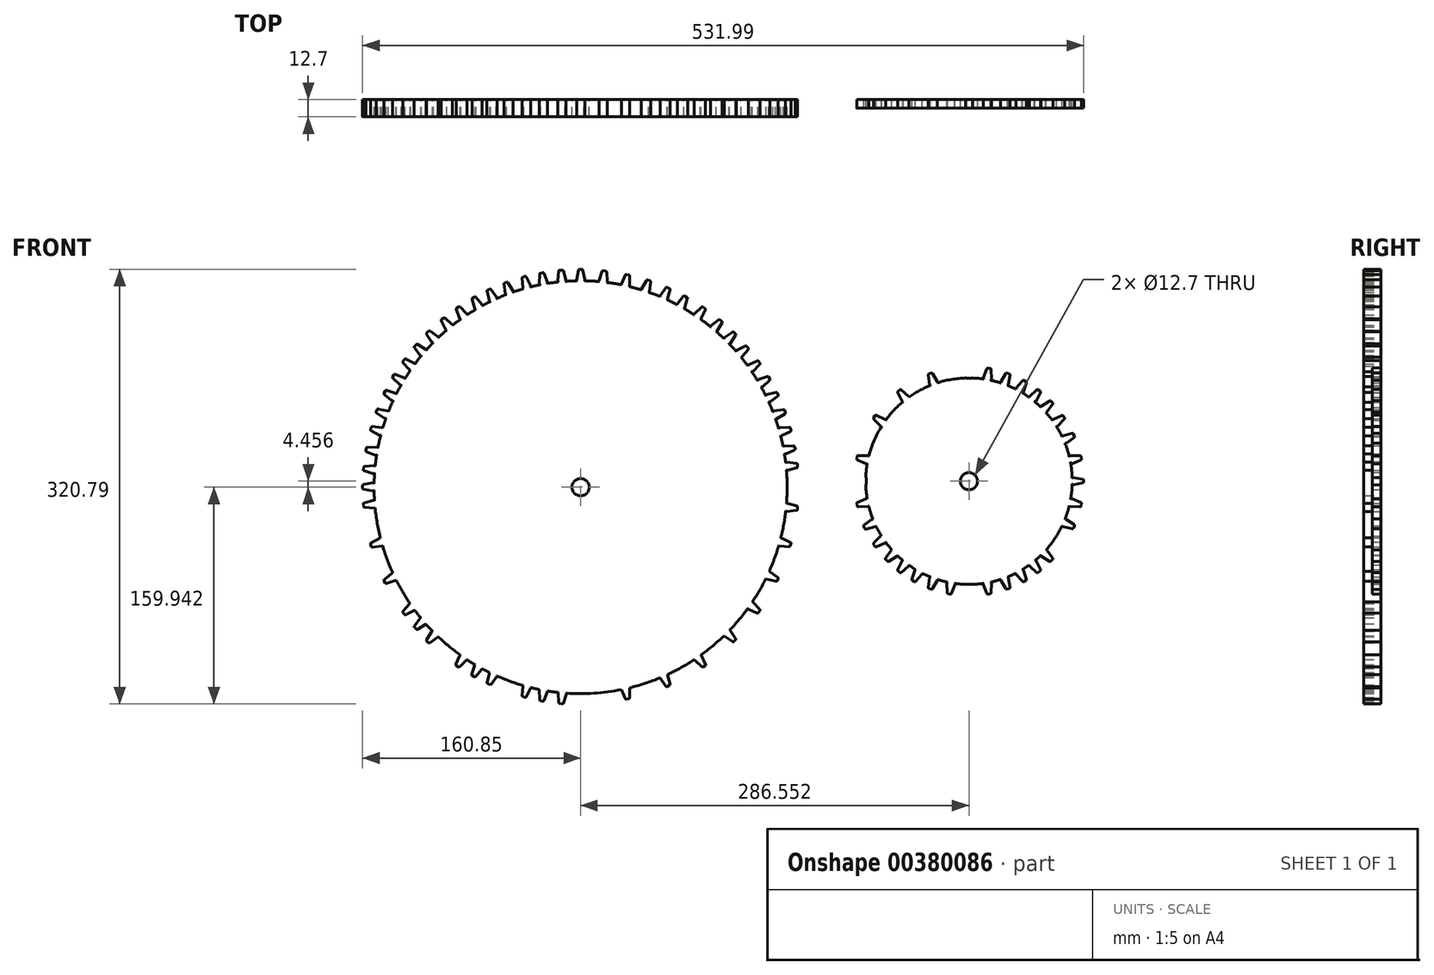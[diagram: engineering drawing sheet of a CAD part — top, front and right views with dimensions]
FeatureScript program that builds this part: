
annotation { "Feature Type Name" : "Feature", "Feature Type Description" : "" }
export const myFeature = defineFeature(function(context is Context, id is Id, definition is map)
    precondition{}
    {
        {
            var Q0;
            Q0=qCreatedBy(makeId("Front.planeOp"),FACE);
            var sketch = newSketch(context, id + "F0", { "sketchPlane" : qUnion([Q0])});
            skCircle(sketch, "E0", {"center": v(-69.44, 32.26) * mm, "radius": 152.4 * mm});
            skCircle(sketch, "E1", {"center": v(217.11, 36.72) * mm, "radius": 76.2 * mm});
            skCircle(sketch, "E2", {"center": v(-69.44, 32.26) * mm, "radius": 6.35 * mm});
            skCircle(sketch, "E3", {"center": v(217.11, 36.72) * mm, "radius": 6.35 * mm});
            skLineSegment(sketch, "E4", {"start": v(-71.67, 184.63) * mm, "end": v(-67.16, 184.63) * mm});
            skLineSegment(sketch, "E5", {"start": v(-66.42, 185.54) * mm, "end": v(-67.77, 192.49) * mm});
            skLineSegment(sketch, "E6", {"start": v(-68.52, 193.1) * mm, "end": v(-70.31, 193.1) * mm});
            skLineSegment(sketch, "E7", {"start": v(-71.06, 192.49) * mm, "end": v(-72.41, 185.54) * mm});
            skPoint(sketch, "E8.visualSharp", {"position": v(-70.94, 193.1) * mm});
            skArc(sketch, "E8.filletArc", {"start": v(-70.31, 193.1) * mm, "mid": v(-70.8, 192.93) * mm, "end": v(-71.06, 192.49) * mm});
            skPoint(sketch, "E9.visualSharp", {"position": v(-67.9, 193.1) * mm});
            skArc(sketch, "E9.filletArc", {"start": v(-67.77, 192.49) * mm, "mid": v(-68.03, 192.93) * mm, "end": v(-68.52, 193.1) * mm});
            skPoint(sketch, "E10.visualSharp", {"position": v(-72.6, 184.63) * mm});
            skArc(sketch, "E10.filletArc", {"start": v(-72.41, 185.54) * mm, "mid": v(-72.25, 184.9) * mm, "end": v(-71.67, 184.63) * mm});
            skPoint(sketch, "E11.visualSharp", {"position": v(-66.24, 184.63) * mm});
            skArc(sketch, "E11.filletArc", {"start": v(-67.16, 184.63) * mm, "mid": v(-66.58, 184.9) * mm, "end": v(-66.42, 185.54) * mm});
            skLineSegment(sketch, "E12", {"start": v(-55.07, 183.9) * mm, "end": v(-50.6, 183.35) * mm});
            skLineSegment(sketch, "E13", {"start": v(-49.75, 184.16) * mm, "end": v(-50.26, 191.23) * mm});
            skLineSegment(sketch, "E14", {"start": v(-50.92, 191.93) * mm, "end": v(-52.7, 192.14) * mm});
            skLineSegment(sketch, "E15", {"start": v(-53.52, 191.62) * mm, "end": v(-55.7, 184.88) * mm});
            skPoint(sketch, "E16.visualSharp", {"position": v(-53.33, 192.22) * mm});
            skArc(sketch, "E16.filletArc", {"start": v(-52.7, 192.14) * mm, "mid": v(-53.2, 192.03) * mm, "end": v(-53.52, 191.62) * mm});
            skPoint(sketch, "E17.visualSharp", {"position": v(-50.3, 191.85) * mm});
            skArc(sketch, "E17.filletArc", {"start": v(-50.26, 191.23) * mm, "mid": v(-50.46, 191.7) * mm, "end": v(-50.92, 191.93) * mm});
            skPoint(sketch, "E18.visualSharp", {"position": v(-55.98, 184) * mm});
            skArc(sketch, "E18.filletArc", {"start": v(-55.7, 184.88) * mm, "mid": v(-55.62, 184.24) * mm, "end": v(-55.07, 183.9) * mm});
            skPoint(sketch, "E19.visualSharp", {"position": v(-49.68, 183.24) * mm});
            skArc(sketch, "E19.filletArc", {"start": v(-50.6, 183.35) * mm, "mid": v(-49.98, 183.55) * mm, "end": v(-49.75, 184.16) * mm});
            skLineSegment(sketch, "E20", {"start": v(-38.66, 181.2) * mm, "end": v(-34.24, 180.34) * mm});
            skLineSegment(sketch, "E21", {"start": v(-33.34, 181.08) * mm, "end": v(-33.33, 188.17) * mm});
            skLineSegment(sketch, "E22", {"start": v(-33.94, 188.92) * mm, "end": v(-35.7, 189.26) * mm});
            skLineSegment(sketch, "E23", {"start": v(-36.55, 188.8) * mm, "end": v(-39.22, 182.24) * mm});
            skPoint(sketch, "E24.visualSharp", {"position": v(-36.32, 189.38) * mm});
            skArc(sketch, "E24.filletArc", {"start": v(-35.7, 189.26) * mm, "mid": v(-36.2, 189.18) * mm, "end": v(-36.55, 188.8) * mm});
            skPoint(sketch, "E25.visualSharp", {"position": v(-33.33, 188.8) * mm});
            skArc(sketch, "E25.filletArc", {"start": v(-33.33, 188.17) * mm, "mid": v(-33.5, 188.65) * mm, "end": v(-33.94, 188.92) * mm});
            skPoint(sketch, "E26.visualSharp", {"position": v(-39.57, 181.38) * mm});
            skArc(sketch, "E26.filletArc", {"start": v(-39.22, 182.24) * mm, "mid": v(-39.18, 181.59) * mm, "end": v(-38.66, 181.2) * mm});
            skPoint(sketch, "E27.visualSharp", {"position": v(-33.34, 180.16) * mm});
            skArc(sketch, "E27.filletArc", {"start": v(-34.24, 180.34) * mm, "mid": v(-33.61, 180.5) * mm, "end": v(-33.34, 181.08) * mm});
            skLineSegment(sketch, "E28", {"start": v(-24.04, 177.66) * mm, "end": v(-19.78, 176.2) * mm});
            skLineSegment(sketch, "E29", {"start": v(-18.78, 176.81) * mm, "end": v(-17.8, 183.83) * mm});
            skLineSegment(sketch, "E30", {"start": v(-18.3, 184.65) * mm, "end": v(-20, 185.24) * mm});
            skLineSegment(sketch, "E31", {"start": v(-20.9, 184.9) * mm, "end": v(-24.45, 178.76) * mm});
            skPoint(sketch, "E32.visualSharp", {"position": v(-20.6, 185.44) * mm});
            skArc(sketch, "E32.filletArc", {"start": v(-20, 185.24) * mm, "mid": v(-20.51, 185.23) * mm, "end": v(-20.9, 184.9) * mm});
            skPoint(sketch, "E33.visualSharp", {"position": v(-17.7, 184.45) * mm});
            skArc(sketch, "E33.filletArc", {"start": v(-17.8, 183.83) * mm, "mid": v(-17.9, 184.33) * mm, "end": v(-18.3, 184.65) * mm});
            skPoint(sketch, "E34.visualSharp", {"position": v(-24.91, 177.96) * mm});
            skArc(sketch, "E34.filletArc", {"start": v(-24.45, 178.76) * mm, "mid": v(-24.5, 178.12) * mm, "end": v(-24.04, 177.66) * mm});
            skPoint(sketch, "E35.visualSharp", {"position": v(-18.9, 175.9) * mm});
            skArc(sketch, "E35.filletArc", {"start": v(-19.78, 176.2) * mm, "mid": v(-19.13, 176.27) * mm, "end": v(-18.78, 176.81) * mm});
            skLineSegment(sketch, "E36", {"start": v(-10.35, 172.62) * mm, "end": v(-6.24, 170.78) * mm});
            skLineSegment(sketch, "E37", {"start": v(-5.2, 171.3) * mm, "end": v(-3.58, 178.2) * mm});
            skLineSegment(sketch, "E38", {"start": v(-4, 179.07) * mm, "end": v(-5.64, 179.8) * mm});
            skLineSegment(sketch, "E39", {"start": v(-6.58, 179.55) * mm, "end": v(-10.66, 173.76) * mm});
            skPoint(sketch, "E40.visualSharp", {"position": v(-6.22, 180.06) * mm});
            skArc(sketch, "E40.filletArc", {"start": v(-5.64, 179.8) * mm, "mid": v(-6.16, 179.84) * mm, "end": v(-6.58, 179.55) * mm});
            skPoint(sketch, "E41.visualSharp", {"position": v(-3.43, 178.8) * mm});
            skArc(sketch, "E41.filletArc", {"start": v(-3.58, 178.2) * mm, "mid": v(-3.64, 178.7) * mm, "end": v(-4, 179.07) * mm});
            skPoint(sketch, "E42.visualSharp", {"position": v(-11.2, 173) * mm});
            skArc(sketch, "E42.filletArc", {"start": v(-10.66, 173.76) * mm, "mid": v(-10.77, 173.12) * mm, "end": v(-10.35, 172.62) * mm});
            skPoint(sketch, "E43.visualSharp", {"position": v(-5.4, 170.4) * mm});
            skArc(sketch, "E43.filletArc", {"start": v(-6.24, 170.78) * mm, "mid": v(-5.6, 170.8) * mm, "end": v(-5.2, 171.3) * mm});
            skLineSegment(sketch, "E44", {"start": v(2.22, 166.6) * mm, "end": v(6.17, 164.44) * mm});
            skLineSegment(sketch, "E45", {"start": v(7.26, 164.87) * mm, "end": v(9.41, 171.62) * mm});
            skLineSegment(sketch, "E46", {"start": v(9.05, 172.52) * mm, "end": v(7.48, 173.38) * mm});
            skLineSegment(sketch, "E47", {"start": v(6.53, 173.2) * mm, "end": v(2, 167.75) * mm});
            skPoint(sketch, "E48.visualSharp", {"position": v(6.93, 173.68) * mm});
            skArc(sketch, "E48.filletArc", {"start": v(7.48, 173.38) * mm, "mid": v(6.97, 173.46) * mm, "end": v(6.53, 173.2) * mm});
            skPoint(sketch, "E49.visualSharp", {"position": v(9.6, 172.22) * mm});
            skArc(sketch, "E49.filletArc", {"start": v(9.41, 171.62) * mm, "mid": v(9.4, 172.14) * mm, "end": v(9.05, 172.52) * mm});
            skPoint(sketch, "E50.visualSharp", {"position": v(1.41, 167.04) * mm});
            skArc(sketch, "E50.filletArc", {"start": v(2, 167.75) * mm, "mid": v(1.84, 167.12) * mm, "end": v(2.22, 166.6) * mm});
            skPoint(sketch, "E51.visualSharp", {"position": v(6.98, 164) * mm});
            skArc(sketch, "E51.filletArc", {"start": v(6.17, 164.44) * mm, "mid": v(6.82, 164.4) * mm, "end": v(7.26, 164.87) * mm});
            skLineSegment(sketch, "E52", {"start": v(14.73, 159.25) * mm, "end": v(18.37, 156.6) * mm});
            skLineSegment(sketch, "E53", {"start": v(19.51, 156.9) * mm, "end": v(22.51, 163.32) * mm});
            skLineSegment(sketch, "E54", {"start": v(22.27, 164.25) * mm, "end": v(20.82, 165.3) * mm});
            skLineSegment(sketch, "E55", {"start": v(19.85, 165.25) * mm, "end": v(14.66, 160.43) * mm});
            skPoint(sketch, "E56.visualSharp", {"position": v(20.31, 165.68) * mm});
            skArc(sketch, "E56.filletArc", {"start": v(20.82, 165.3) * mm, "mid": v(20.33, 165.45) * mm, "end": v(19.85, 165.25) * mm});
            skPoint(sketch, "E57.visualSharp", {"position": v(22.78, 163.88) * mm});
            skArc(sketch, "E57.filletArc", {"start": v(22.51, 163.32) * mm, "mid": v(22.56, 163.83) * mm, "end": v(22.27, 164.25) * mm});
            skPoint(sketch, "E58.visualSharp", {"position": v(13.99, 159.8) * mm});
            skArc(sketch, "E58.filletArc", {"start": v(14.66, 160.43) * mm, "mid": v(14.42, 159.82) * mm, "end": v(14.73, 159.25) * mm});
            skPoint(sketch, "E59.visualSharp", {"position": v(19.12, 156.06) * mm});
            skArc(sketch, "E59.filletArc", {"start": v(18.37, 156.6) * mm, "mid": v(19.01, 156.48) * mm, "end": v(19.51, 156.9) * mm});
            skLineSegment(sketch, "E60", {"start": v(26.76, 150.4) * mm, "end": v(30.12, 147.41) * mm});
            skLineSegment(sketch, "E61", {"start": v(31.28, 147.6) * mm, "end": v(34.9, 153.69) * mm});
            skLineSegment(sketch, "E62", {"start": v(34.75, 154.65) * mm, "end": v(33.4, 155.84) * mm});
            skLineSegment(sketch, "E63", {"start": v(32.44, 155.88) * mm, "end": v(26.8, 151.58) * mm});
            skPoint(sketch, "E64.visualSharp", {"position": v(32.94, 156.26) * mm});
            skArc(sketch, "E64.filletArc", {"start": v(33.4, 155.84) * mm, "mid": v(32.93, 156.03) * mm, "end": v(32.44, 155.88) * mm});
            skPoint(sketch, "E65.visualSharp", {"position": v(35.21, 154.23) * mm});
            skArc(sketch, "E65.filletArc", {"start": v(34.9, 153.69) * mm, "mid": v(35, 154.2) * mm, "end": v(34.75, 154.65) * mm});
            skPoint(sketch, "E66.visualSharp", {"position": v(26.07, 151.02) * mm});
            skArc(sketch, "E66.filletArc", {"start": v(26.8, 151.58) * mm, "mid": v(26.5, 151) * mm, "end": v(26.76, 150.4) * mm});
            skPoint(sketch, "E67.visualSharp", {"position": v(30.81, 146.8) * mm});
            skArc(sketch, "E67.filletArc", {"start": v(30.12, 147.41) * mm, "mid": v(30.75, 147.23) * mm, "end": v(31.28, 147.6) * mm});
            skLineSegment(sketch, "E68", {"start": v(36.65, 141.64) * mm, "end": v(39.84, 138.46) * mm});
            skLineSegment(sketch, "E69", {"start": v(41, 138.58) * mm, "end": v(44.97, 144.45) * mm});
            skLineSegment(sketch, "E70", {"start": v(44.87, 145.41) * mm, "end": v(43.6, 146.68) * mm});
            skLineSegment(sketch, "E71", {"start": v(42.64, 146.77) * mm, "end": v(36.77, 142.82) * mm});
            skPoint(sketch, "E72.visualSharp", {"position": v(43.16, 147.13) * mm});
            skArc(sketch, "E72.filletArc", {"start": v(43.6, 146.68) * mm, "mid": v(43.14, 146.9) * mm, "end": v(42.64, 146.77) * mm});
            skPoint(sketch, "E73.visualSharp", {"position": v(45.32, 144.97) * mm});
            skArc(sketch, "E73.filletArc", {"start": v(44.97, 144.45) * mm, "mid": v(45.1, 144.95) * mm, "end": v(44.87, 145.41) * mm});
            skPoint(sketch, "E74.visualSharp", {"position": v(36, 142.3) * mm});
            skArc(sketch, "E74.filletArc", {"start": v(36.77, 142.82) * mm, "mid": v(36.43, 142.26) * mm, "end": v(36.65, 141.64) * mm});
            skPoint(sketch, "E75.visualSharp", {"position": v(40.5, 137.8) * mm});
            skArc(sketch, "E75.filletArc", {"start": v(39.84, 138.46) * mm, "mid": v(40.45, 138.24) * mm, "end": v(41, 138.58) * mm});
            skLineSegment(sketch, "E76", {"start": v(45.65, 132.08) * mm, "end": v(48.42, 128.53) * mm});
            skLineSegment(sketch, "E77", {"start": v(49.6, 128.5) * mm, "end": v(54.25, 133.85) * mm});
            skLineSegment(sketch, "E78", {"start": v(54.27, 134.82) * mm, "end": v(53.17, 136.23) * mm});
            skLineSegment(sketch, "E79", {"start": v(52.22, 136.44) * mm, "end": v(45.9, 133.23) * mm});
            skPoint(sketch, "E80.visualSharp", {"position": v(52.78, 136.72) * mm});
            skArc(sketch, "E80.filletArc", {"start": v(53.17, 136.23) * mm, "mid": v(52.73, 136.5) * mm, "end": v(52.22, 136.44) * mm});
            skPoint(sketch, "E81.visualSharp", {"position": v(54.66, 134.32) * mm});
            skArc(sketch, "E81.filletArc", {"start": v(54.25, 133.85) * mm, "mid": v(54.43, 134.33) * mm, "end": v(54.27, 134.82) * mm});
            skPoint(sketch, "E82.visualSharp", {"position": v(45.09, 132.8) * mm});
            skArc(sketch, "E82.filletArc", {"start": v(45.9, 133.23) * mm, "mid": v(45.51, 132.71) * mm, "end": v(45.65, 132.08) * mm});
            skPoint(sketch, "E83.visualSharp", {"position": v(49, 127.8) * mm});
            skArc(sketch, "E83.filletArc", {"start": v(48.42, 128.53) * mm, "mid": v(49, 128.24) * mm, "end": v(49.6, 128.5) * mm});
            skLineSegment(sketch, "E84", {"start": v(54.04, 121.56) * mm, "end": v(56.62, 117.87) * mm});
            skLineSegment(sketch, "E85", {"start": v(57.8, 117.78) * mm, "end": v(62.71, 122.88) * mm});
            skLineSegment(sketch, "E86", {"start": v(62.79, 123.84) * mm, "end": v(61.76, 125.31) * mm});
            skLineSegment(sketch, "E87", {"start": v(60.82, 125.57) * mm, "end": v(54.35, 122.7) * mm});
            skPoint(sketch, "E88.visualSharp", {"position": v(61.4, 125.83) * mm});
            skArc(sketch, "E88.filletArc", {"start": v(61.76, 125.31) * mm, "mid": v(61.34, 125.6) * mm, "end": v(60.82, 125.57) * mm});
            skPoint(sketch, "E89.visualSharp", {"position": v(63.15, 123.33) * mm});
            skArc(sketch, "E89.filletArc", {"start": v(62.71, 122.88) * mm, "mid": v(62.92, 123.35) * mm, "end": v(62.79, 123.84) * mm});
            skPoint(sketch, "E90.visualSharp", {"position": v(53.5, 122.32) * mm});
            skArc(sketch, "E90.filletArc", {"start": v(54.35, 122.7) * mm, "mid": v(53.93, 122.2) * mm, "end": v(54.04, 121.56) * mm});
            skPoint(sketch, "E91.visualSharp", {"position": v(57.15, 117.11) * mm});
            skArc(sketch, "E91.filletArc", {"start": v(56.62, 117.87) * mm, "mid": v(57.18, 117.55) * mm, "end": v(57.8, 117.78) * mm});
            skLineSegment(sketch, "E92", {"start": v(61.3, 110.53) * mm, "end": v(63.55, 106.64) * mm});
            skLineSegment(sketch, "E93", {"start": v(64.71, 106.44) * mm, "end": v(70.06, 111.1) * mm});
            skLineSegment(sketch, "E94", {"start": v(70.22, 112.05) * mm, "end": v(69.32, 113.6) * mm});
            skLineSegment(sketch, "E95", {"start": v(68.41, 113.94) * mm, "end": v(61.72, 111.64) * mm});
            skPoint(sketch, "E96.visualSharp", {"position": v(69, 114.14) * mm});
            skArc(sketch, "E96.filletArc", {"start": v(69.32, 113.6) * mm, "mid": v(68.93, 113.93) * mm, "end": v(68.41, 113.94) * mm});
            skPoint(sketch, "E97.visualSharp", {"position": v(70.53, 111.5) * mm});
            skArc(sketch, "E97.filletArc", {"start": v(70.06, 111.1) * mm, "mid": v(70.3, 111.54) * mm, "end": v(70.22, 112.05) * mm});
            skPoint(sketch, "E98.visualSharp", {"position": v(60.84, 111.33) * mm});
            skArc(sketch, "E98.filletArc", {"start": v(61.72, 111.64) * mm, "mid": v(61.25, 111.18) * mm, "end": v(61.3, 110.53) * mm});
            skPoint(sketch, "E99.visualSharp", {"position": v(64.02, 105.84) * mm});
            skArc(sketch, "E99.filletArc", {"start": v(63.55, 106.64) * mm, "mid": v(64.09, 106.27) * mm, "end": v(64.71, 106.44) * mm});
            skLineSegment(sketch, "E100", {"start": v(67.3, 99.5) * mm, "end": v(69.2, 95.41) * mm});
            skLineSegment(sketch, "E101", {"start": v(70.35, 95.12) * mm, "end": v(76.07, 99.28) * mm});
            skLineSegment(sketch, "E102", {"start": v(76.32, 100.22) * mm, "end": v(75.56, 101.85) * mm});
            skLineSegment(sketch, "E103", {"start": v(74.69, 102.26) * mm, "end": v(67.81, 100.55) * mm});
            skPoint(sketch, "E104.visualSharp", {"position": v(75.3, 102.42) * mm});
            skArc(sketch, "E104.filletArc", {"start": v(75.56, 101.85) * mm, "mid": v(75.2, 102.21) * mm, "end": v(74.69, 102.26) * mm});
            skPoint(sketch, "E105.visualSharp", {"position": v(76.58, 99.65) * mm});
            skArc(sketch, "E105.filletArc", {"start": v(76.07, 99.28) * mm, "mid": v(76.36, 99.7) * mm, "end": v(76.32, 100.22) * mm});
            skPoint(sketch, "E106.visualSharp", {"position": v(66.91, 100.33) * mm});
            skArc(sketch, "E106.filletArc", {"start": v(67.81, 100.55) * mm, "mid": v(67.3, 100.14) * mm, "end": v(67.3, 99.5) * mm});
            skPoint(sketch, "E107.visualSharp", {"position": v(69.6, 94.57) * mm});
            skArc(sketch, "E107.filletArc", {"start": v(69.2, 95.41) * mm, "mid": v(69.7, 95) * mm, "end": v(70.35, 95.12) * mm});
            skLineSegment(sketch, "E108", {"start": v(72.59, 87.47) * mm, "end": v(74.13, 83.24) * mm});
            skLineSegment(sketch, "E109", {"start": v(75.23, 82.84) * mm, "end": v(81.3, 86.5) * mm});
            skLineSegment(sketch, "E110", {"start": v(81.63, 87.4) * mm, "end": v(81.01, 89.1) * mm});
            skLineSegment(sketch, "E111", {"start": v(80.18, 89.58) * mm, "end": v(73.18, 88.48) * mm});
            skPoint(sketch, "E112.visualSharp", {"position": v(80.8, 89.68) * mm});
            skArc(sketch, "E112.filletArc", {"start": v(81.01, 89.1) * mm, "mid": v(80.69, 89.49) * mm, "end": v(80.18, 89.58) * mm});
            skPoint(sketch, "E113.visualSharp", {"position": v(81.84, 86.82) * mm});
            skArc(sketch, "E113.filletArc", {"start": v(81.3, 86.5) * mm, "mid": v(81.63, 86.9) * mm, "end": v(81.63, 87.4) * mm});
            skPoint(sketch, "E114.visualSharp", {"position": v(72.27, 88.33) * mm});
            skArc(sketch, "E114.filletArc", {"start": v(73.18, 88.48) * mm, "mid": v(72.65, 88.11) * mm, "end": v(72.59, 87.47) * mm});
            skPoint(sketch, "E115.visualSharp", {"position": v(74.44, 82.37) * mm});
            skArc(sketch, "E115.filletArc", {"start": v(74.13, 83.24) * mm, "mid": v(74.59, 82.78) * mm, "end": v(75.23, 82.84) * mm});
            skLineSegment(sketch, "E116", {"start": v(76.77, 75.17) * mm, "end": v(77.93, 70.82) * mm});
            skLineSegment(sketch, "E117", {"start": v(79, 70.33) * mm, "end": v(85.37, 73.44) * mm});
            skLineSegment(sketch, "E118", {"start": v(85.77, 74.32) * mm, "end": v(85.3, 76.05) * mm});
            skLineSegment(sketch, "E119", {"start": v(84.52, 76.61) * mm, "end": v(77.45, 76.12) * mm});
            skPoint(sketch, "E120.visualSharp", {"position": v(85.15, 76.66) * mm});
            skArc(sketch, "E120.filletArc", {"start": v(85.3, 76.05) * mm, "mid": v(85.02, 76.48) * mm, "end": v(84.52, 76.61) * mm});
            skPoint(sketch, "E121.visualSharp", {"position": v(85.93, 73.71) * mm});
            skArc(sketch, "E121.filletArc", {"start": v(85.37, 73.44) * mm, "mid": v(85.73, 73.8) * mm, "end": v(85.77, 74.32) * mm});
            skPoint(sketch, "E122.visualSharp", {"position": v(76.53, 76.06) * mm});
            skArc(sketch, "E122.filletArc", {"start": v(77.45, 76.12) * mm, "mid": v(76.89, 75.8) * mm, "end": v(76.77, 75.17) * mm});
            skPoint(sketch, "E123.visualSharp", {"position": v(78.17, 69.93) * mm});
            skArc(sketch, "E123.filletArc", {"start": v(77.93, 70.82) * mm, "mid": v(78.36, 70.32) * mm, "end": v(79, 70.33) * mm});
            skLineSegment(sketch, "E124", {"start": v(79.86, 61.76) * mm, "end": v(80.83, 57.37) * mm});
            skLineSegment(sketch, "E125", {"start": v(81.87, 56.83) * mm, "end": v(88.37, 59.65) * mm});
            skLineSegment(sketch, "E126", {"start": v(88.81, 60.52) * mm, "end": v(88.42, 62.27) * mm});
            skLineSegment(sketch, "E127", {"start": v(87.66, 62.86) * mm, "end": v(80.58, 62.69) * mm});
            skPoint(sketch, "E128.visualSharp", {"position": v(88.29, 62.88) * mm});
            skArc(sketch, "E128.filletArc", {"start": v(88.42, 62.27) * mm, "mid": v(88.15, 62.7) * mm, "end": v(87.66, 62.86) * mm});
            skPoint(sketch, "E129.visualSharp", {"position": v(88.95, 59.9) * mm});
            skArc(sketch, "E129.filletArc", {"start": v(88.37, 59.65) * mm, "mid": v(88.75, 60) * mm, "end": v(88.81, 60.52) * mm});
            skPoint(sketch, "E130.visualSharp", {"position": v(79.66, 62.66) * mm});
            skArc(sketch, "E130.filletArc", {"start": v(80.58, 62.69) * mm, "mid": v(80, 62.4) * mm, "end": v(79.86, 61.76) * mm});
            skPoint(sketch, "E131.visualSharp", {"position": v(81.03, 56.46) * mm});
            skArc(sketch, "E131.filletArc", {"start": v(80.83, 57.37) * mm, "mid": v(81.22, 56.85) * mm, "end": v(81.87, 56.83) * mm});
            skLineSegment(sketch, "E132", {"start": v(81.91, 49.85) * mm, "end": v(82.3, 45.37) * mm});
            skLineSegment(sketch, "E133", {"start": v(83.27, 44.7) * mm, "end": v(90.08, 46.66) * mm});
            skLineSegment(sketch, "E134", {"start": v(90.63, 47.46) * mm, "end": v(90.47, 49.24) * mm});
            skLineSegment(sketch, "E135", {"start": v(89.8, 49.93) * mm, "end": v(82.75, 50.68) * mm});
            skPoint(sketch, "E136.visualSharp", {"position": v(90.42, 49.87) * mm});
            skArc(sketch, "E136.filletArc", {"start": v(90.47, 49.24) * mm, "mid": v(90.26, 49.71) * mm, "end": v(89.8, 49.93) * mm});
            skPoint(sketch, "E137.visualSharp", {"position": v(90.69, 46.83) * mm});
            skArc(sketch, "E137.filletArc", {"start": v(90.08, 46.66) * mm, "mid": v(90.5, 46.96) * mm, "end": v(90.63, 47.46) * mm});
            skPoint(sketch, "E138.visualSharp", {"position": v(81.83, 50.78) * mm});
            skArc(sketch, "E138.filletArc", {"start": v(82.75, 50.68) * mm, "mid": v(82.14, 50.46) * mm, "end": v(81.91, 49.85) * mm});
            skPoint(sketch, "E139.visualSharp", {"position": v(82.38, 44.45) * mm});
            skArc(sketch, "E139.filletArc", {"start": v(82.3, 45.37) * mm, "mid": v(82.63, 44.8) * mm, "end": v(83.27, 44.7) * mm});
            skPoint(sketch, "E140.visualSharp", {"position": v(82.66, 35.68) * mm});
            skLineSegment(sketch, "E141", {"start": v(-85.45, 183.8) * mm, "end": v(-80.97, 184.23) * mm});
            skLineSegment(sketch, "E142", {"start": v(-80.3, 185.2) * mm, "end": v(-82.3, 192) * mm});
            skLineSegment(sketch, "E143", {"start": v(-83.1, 192.54) * mm, "end": v(-84.9, 192.37) * mm});
            skLineSegment(sketch, "E144", {"start": v(-85.58, 191.69) * mm, "end": v(-86.28, 184.64) * mm});
            skPoint(sketch, "E145.visualSharp", {"position": v(-85.52, 192.31) * mm});
            skArc(sketch, "E145.filletArc", {"start": v(-84.9, 192.37) * mm, "mid": v(-85.36, 192.15) * mm, "end": v(-85.58, 191.69) * mm});
            skPoint(sketch, "E146.visualSharp", {"position": v(-82.48, 192.6) * mm});
            skArc(sketch, "E146.filletArc", {"start": v(-82.3, 192) * mm, "mid": v(-82.61, 192.41) * mm, "end": v(-83.1, 192.54) * mm});
            skPoint(sketch, "E147.visualSharp", {"position": v(-86.37, 183.72) * mm});
            skArc(sketch, "E147.filletArc", {"start": v(-86.28, 184.64) * mm, "mid": v(-86.06, 184.03) * mm, "end": v(-85.45, 183.8) * mm});
            skPoint(sketch, "E148.visualSharp", {"position": v(-80.05, 184.31) * mm});
            skArc(sketch, "E148.filletArc", {"start": v(-80.97, 184.23) * mm, "mid": v(-80.4, 184.56) * mm, "end": v(-80.3, 185.2) * mm});
            skLineSegment(sketch, "E149", {"start": v(-98.97, 181.75) * mm, "end": v(-94.54, 182.53) * mm});
            skLineSegment(sketch, "E150", {"start": v(-93.96, 183.56) * mm, "end": v(-96.5, 190.17) * mm});
            skLineSegment(sketch, "E151", {"start": v(-97.35, 190.65) * mm, "end": v(-99.11, 190.33) * mm});
            skLineSegment(sketch, "E152", {"start": v(-99.74, 189.6) * mm, "end": v(-99.87, 182.52) * mm});
            skPoint(sketch, "E153.visualSharp", {"position": v(-99.73, 190.23) * mm});
            skArc(sketch, "E153.filletArc", {"start": v(-99.11, 190.33) * mm, "mid": v(-99.56, 190.08) * mm, "end": v(-99.74, 189.6) * mm});
            skPoint(sketch, "E154.visualSharp", {"position": v(-96.73, 190.75) * mm});
            skArc(sketch, "E154.filletArc", {"start": v(-96.5, 190.17) * mm, "mid": v(-96.84, 190.56) * mm, "end": v(-97.35, 190.65) * mm});
            skPoint(sketch, "E155.visualSharp", {"position": v(-99.88, 181.6) * mm});
            skArc(sketch, "E155.filletArc", {"start": v(-99.87, 182.52) * mm, "mid": v(-99.6, 181.92) * mm, "end": v(-98.97, 181.75) * mm});
            skPoint(sketch, "E156.visualSharp", {"position": v(-93.63, 182.7) * mm});
            skArc(sketch, "E156.filletArc", {"start": v(-94.54, 182.53) * mm, "mid": v(-94.01, 182.9) * mm, "end": v(-93.96, 183.56) * mm});
            skLineSegment(sketch, "E157", {"start": v(-111.2, 178.81) * mm, "end": v(-106.85, 179.98) * mm});
            skLineSegment(sketch, "E158", {"start": v(-106.37, 181.05) * mm, "end": v(-109.47, 187.41) * mm});
            skLineSegment(sketch, "E159", {"start": v(-110.36, 187.81) * mm, "end": v(-112.09, 187.35) * mm});
            skLineSegment(sketch, "E160", {"start": v(-112.65, 186.56) * mm, "end": v(-112.16, 179.5) * mm});
            skPoint(sketch, "E161.visualSharp", {"position": v(-112.7, 187.19) * mm});
            skArc(sketch, "E161.filletArc", {"start": v(-112.09, 187.35) * mm, "mid": v(-112.5, 187.06) * mm, "end": v(-112.65, 186.56) * mm});
            skPoint(sketch, "E162.visualSharp", {"position": v(-109.75, 187.98) * mm});
            skArc(sketch, "E162.filletArc", {"start": v(-109.47, 187.41) * mm, "mid": v(-109.84, 187.77) * mm, "end": v(-110.36, 187.81) * mm});
            skPoint(sketch, "E163.visualSharp", {"position": v(-112.1, 178.57) * mm});
            skArc(sketch, "E163.filletArc", {"start": v(-112.16, 179.5) * mm, "mid": v(-111.84, 178.93) * mm, "end": v(-111.2, 178.81) * mm});
            skPoint(sketch, "E164.visualSharp", {"position": v(-105.96, 180.21) * mm});
            skArc(sketch, "E164.filletArc", {"start": v(-106.85, 179.98) * mm, "mid": v(-106.36, 180.4) * mm, "end": v(-106.37, 181.05) * mm});
            skLineSegment(sketch, "E165", {"start": v(-123.97, 174.55) * mm, "end": v(-119.74, 176.1) * mm});
            skLineSegment(sketch, "E166", {"start": v(-119.35, 177.2) * mm, "end": v(-123, 183.27) * mm});
            skLineSegment(sketch, "E167", {"start": v(-123.9, 183.6) * mm, "end": v(-125.6, 182.98) * mm});
            skLineSegment(sketch, "E168", {"start": v(-126.08, 182.15) * mm, "end": v(-124.98, 175.15) * mm});
            skPoint(sketch, "E169.visualSharp", {"position": v(-126.18, 182.77) * mm});
            skArc(sketch, "E169.filletArc", {"start": v(-125.6, 182.98) * mm, "mid": v(-125.99, 182.65) * mm, "end": v(-126.08, 182.15) * mm});
            skPoint(sketch, "E170.visualSharp", {"position": v(-123.32, 183.81) * mm});
            skArc(sketch, "E170.filletArc", {"start": v(-123, 183.27) * mm, "mid": v(-123.4, 183.6) * mm, "end": v(-123.9, 183.6) * mm});
            skPoint(sketch, "E171.visualSharp", {"position": v(-124.84, 174.24) * mm});
            skArc(sketch, "E171.filletArc", {"start": v(-124.98, 175.15) * mm, "mid": v(-124.61, 174.61) * mm, "end": v(-123.97, 174.55) * mm});
            skPoint(sketch, "E172.visualSharp", {"position": v(-118.87, 176.4) * mm});
            skArc(sketch, "E172.filletArc", {"start": v(-119.74, 176.1) * mm, "mid": v(-119.28, 176.55) * mm, "end": v(-119.35, 177.2) * mm});
            skLineSegment(sketch, "E173", {"start": v(-135.74, 169.47) * mm, "end": v(-131.66, 171.37) * mm});
            skLineSegment(sketch, "E174", {"start": v(-131.36, 172.51) * mm, "end": v(-135.53, 178.24) * mm});
            skLineSegment(sketch, "E175", {"start": v(-136.47, 178.48) * mm, "end": v(-138.1, 177.72) * mm});
            skLineSegment(sketch, "E176", {"start": v(-138.5, 176.85) * mm, "end": v(-136.8, 169.98) * mm});
            skPoint(sketch, "E177.visualSharp", {"position": v(-138.66, 177.46) * mm});
            skArc(sketch, "E177.filletArc", {"start": v(-138.1, 177.72) * mm, "mid": v(-138.46, 177.36) * mm, "end": v(-138.5, 176.85) * mm});
            skPoint(sketch, "E178.visualSharp", {"position": v(-135.9, 178.75) * mm});
            skArc(sketch, "E178.filletArc", {"start": v(-135.53, 178.24) * mm, "mid": v(-135.95, 178.53) * mm, "end": v(-136.47, 178.48) * mm});
            skPoint(sketch, "E179.visualSharp", {"position": v(-136.57, 169.08) * mm});
            skArc(sketch, "E179.filletArc", {"start": v(-136.8, 169.98) * mm, "mid": v(-136.39, 169.47) * mm, "end": v(-135.74, 169.47) * mm});
            skPoint(sketch, "E180.visualSharp", {"position": v(-130.82, 171.76) * mm});
            skArc(sketch, "E180.filletArc", {"start": v(-131.66, 171.37) * mm, "mid": v(-131.24, 171.87) * mm, "end": v(-131.36, 172.51) * mm});
            skLineSegment(sketch, "E181", {"start": v(-146.43, 163.73) * mm, "end": v(-142.44, 165.83) * mm});
            skLineSegment(sketch, "E182", {"start": v(-142.2, 166.98) * mm, "end": v(-146.63, 172.5) * mm});
            skLineSegment(sketch, "E183", {"start": v(-147.58, 172.7) * mm, "end": v(-149.17, 171.87) * mm});
            skLineSegment(sketch, "E184", {"start": v(-149.54, 170.98) * mm, "end": v(-147.51, 164.2) * mm});
            skPoint(sketch, "E185.visualSharp", {"position": v(-149.72, 171.58) * mm});
            skArc(sketch, "E185.filletArc", {"start": v(-149.17, 171.87) * mm, "mid": v(-149.52, 171.49) * mm, "end": v(-149.54, 170.98) * mm});
            skPoint(sketch, "E186.visualSharp", {"position": v(-147.02, 173) * mm});
            skArc(sketch, "E186.filletArc", {"start": v(-146.63, 172.5) * mm, "mid": v(-147.07, 172.77) * mm, "end": v(-147.58, 172.7) * mm});
            skPoint(sketch, "E187.visualSharp", {"position": v(-147.25, 163.3) * mm});
            skArc(sketch, "E187.filletArc", {"start": v(-147.51, 164.2) * mm, "mid": v(-147.08, 163.7) * mm, "end": v(-146.43, 163.73) * mm});
            skPoint(sketch, "E188.visualSharp", {"position": v(-141.62, 166.26) * mm});
            skArc(sketch, "E188.filletArc", {"start": v(-142.44, 165.83) * mm, "mid": v(-142.05, 166.34) * mm, "end": v(-142.2, 166.98) * mm});
            skLineSegment(sketch, "E189", {"start": v(-157.47, 156.6) * mm, "end": v(-153.68, 159.03) * mm});
            skLineSegment(sketch, "E190", {"start": v(-153.53, 160.2) * mm, "end": v(-158.41, 165.33) * mm});
            skLineSegment(sketch, "E191", {"start": v(-159.38, 165.45) * mm, "end": v(-160.89, 164.48) * mm});
            skLineSegment(sketch, "E192", {"start": v(-161.19, 163.56) * mm, "end": v(-158.6, 156.97) * mm});
            skPoint(sketch, "E193.visualSharp", {"position": v(-161.42, 164.15) * mm});
            skArc(sketch, "E193.filletArc", {"start": v(-160.89, 164.48) * mm, "mid": v(-161.2, 164.08) * mm, "end": v(-161.19, 163.56) * mm});
            skPoint(sketch, "E194.visualSharp", {"position": v(-158.85, 165.78) * mm});
            skArc(sketch, "E194.filletArc", {"start": v(-158.41, 165.33) * mm, "mid": v(-158.87, 165.56) * mm, "end": v(-159.38, 165.45) * mm});
            skPoint(sketch, "E195.visualSharp", {"position": v(-158.25, 156.1) * mm});
            skArc(sketch, "E195.filletArc", {"start": v(-158.6, 156.97) * mm, "mid": v(-158.12, 156.52) * mm, "end": v(-157.47, 156.6) * mm});
            skPoint(sketch, "E196.visualSharp", {"position": v(-152.9, 159.52) * mm});
            skArc(sketch, "E196.filletArc", {"start": v(-153.68, 159.03) * mm, "mid": v(-153.33, 159.58) * mm, "end": v(-153.53, 160.2) * mm});
            skLineSegment(sketch, "E197", {"start": v(-167.9, 148.52) * mm, "end": v(-164.32, 151.26) * mm});
            skLineSegment(sketch, "E198", {"start": v(-164.28, 152.43) * mm, "end": v(-169.57, 157.13) * mm});
            skLineSegment(sketch, "E199", {"start": v(-170.54, 157.17) * mm, "end": v(-171.97, 156.08) * mm});
            skLineSegment(sketch, "E200", {"start": v(-172.19, 155.14) * mm, "end": v(-169.04, 148.8) * mm});
            skPoint(sketch, "E201.visualSharp", {"position": v(-172.46, 155.7) * mm});
            skArc(sketch, "E201.filletArc", {"start": v(-171.97, 156.08) * mm, "mid": v(-172.25, 155.65) * mm, "end": v(-172.19, 155.14) * mm});
            skPoint(sketch, "E202.visualSharp", {"position": v(-170.04, 157.55) * mm});
            skArc(sketch, "E202.filletArc", {"start": v(-169.57, 157.13) * mm, "mid": v(-170.05, 157.33) * mm, "end": v(-170.54, 157.17) * mm});
            skPoint(sketch, "E203.visualSharp", {"position": v(-168.63, 147.96) * mm});
            skArc(sketch, "E203.filletArc", {"start": v(-169.04, 148.8) * mm, "mid": v(-168.53, 148.39) * mm, "end": v(-167.9, 148.52) * mm});
            skPoint(sketch, "E204.visualSharp", {"position": v(-163.59, 151.82) * mm});
            skArc(sketch, "E204.filletArc", {"start": v(-164.32, 151.26) * mm, "mid": v(-164.02, 151.83) * mm, "end": v(-164.28, 152.43) * mm});
            skLineSegment(sketch, "E205", {"start": v(-178.04, 139.16) * mm, "end": v(-174.82, 142.3) * mm});
            skLineSegment(sketch, "E206", {"start": v(-174.92, 143.47) * mm, "end": v(-180.74, 147.5) * mm});
            skLineSegment(sketch, "E207", {"start": v(-181.7, 147.42) * mm, "end": v(-182.99, 146.17) * mm});
            skLineSegment(sketch, "E208", {"start": v(-183.1, 145.2) * mm, "end": v(-179.2, 139.28) * mm});
            skPoint(sketch, "E209.visualSharp", {"position": v(-183.44, 145.73) * mm});
            skArc(sketch, "E209.filletArc", {"start": v(-182.99, 146.17) * mm, "mid": v(-183.21, 145.7) * mm, "end": v(-183.1, 145.2) * mm});
            skPoint(sketch, "E210.visualSharp", {"position": v(-181.26, 147.86) * mm});
            skArc(sketch, "E210.filletArc", {"start": v(-180.74, 147.5) * mm, "mid": v(-181.24, 147.63) * mm, "end": v(-181.7, 147.42) * mm});
            skPoint(sketch, "E211.visualSharp", {"position": v(-178.7, 138.5) * mm});
            skArc(sketch, "E211.filletArc", {"start": v(-179.2, 139.28) * mm, "mid": v(-178.65, 138.94) * mm, "end": v(-178.04, 139.16) * mm});
            skPoint(sketch, "E212.visualSharp", {"position": v(-174.15, 142.94) * mm});
            skArc(sketch, "E212.filletArc", {"start": v(-174.82, 142.3) * mm, "mid": v(-174.59, 142.9) * mm, "end": v(-174.92, 143.47) * mm});
            skLineSegment(sketch, "E213", {"start": v(-186.7, 129.55) * mm, "end": v(-183.68, 132.9) * mm});
            skLineSegment(sketch, "E214", {"start": v(-183.86, 134.06) * mm, "end": v(-189.93, 137.7) * mm});
            skLineSegment(sketch, "E215", {"start": v(-190.89, 137.56) * mm, "end": v(-192.09, 136.23) * mm});
            skLineSegment(sketch, "E216", {"start": v(-192.13, 135.26) * mm, "end": v(-187.87, 129.6) * mm});
            skPoint(sketch, "E217.visualSharp", {"position": v(-192.5, 135.76) * mm});
            skArc(sketch, "E217.filletArc", {"start": v(-192.09, 136.23) * mm, "mid": v(-192.28, 135.75) * mm, "end": v(-192.13, 135.26) * mm});
            skPoint(sketch, "E218.visualSharp", {"position": v(-190.47, 138.03) * mm});
            skArc(sketch, "E218.filletArc", {"start": v(-189.93, 137.7) * mm, "mid": v(-190.44, 137.8) * mm, "end": v(-190.89, 137.56) * mm});
            skPoint(sketch, "E219.visualSharp", {"position": v(-187.31, 128.86) * mm});
            skArc(sketch, "E219.filletArc", {"start": v(-187.87, 129.6) * mm, "mid": v(-187.3, 129.3) * mm, "end": v(-186.7, 129.55) * mm});
            skPoint(sketch, "E220.visualSharp", {"position": v(-183.07, 133.58) * mm});
            skArc(sketch, "E220.filletArc", {"start": v(-183.68, 132.9) * mm, "mid": v(-183.5, 133.52) * mm, "end": v(-183.86, 134.06) * mm});
            skLineSegment(sketch, "E221", {"start": v(-194.7, 119) * mm, "end": v(-191.94, 122.55) * mm});
            skLineSegment(sketch, "E222", {"start": v(-192.2, 123.7) * mm, "end": v(-198.53, 126.88) * mm});
            skLineSegment(sketch, "E223", {"start": v(-199.48, 126.66) * mm, "end": v(-200.57, 125.25) * mm});
            skLineSegment(sketch, "E224", {"start": v(-200.54, 124.28) * mm, "end": v(-195.87, 118.96) * mm});
            skPoint(sketch, "E225.visualSharp", {"position": v(-200.96, 124.75) * mm});
            skArc(sketch, "E225.filletArc", {"start": v(-200.57, 125.25) * mm, "mid": v(-200.73, 124.76) * mm, "end": v(-200.54, 124.28) * mm});
            skPoint(sketch, "E226.visualSharp", {"position": v(-199.1, 127.16) * mm});
            skArc(sketch, "E226.filletArc", {"start": v(-198.53, 126.88) * mm, "mid": v(-199.04, 126.94) * mm, "end": v(-199.48, 126.66) * mm});
            skPoint(sketch, "E227.visualSharp", {"position": v(-195.26, 118.26) * mm});
            skArc(sketch, "E227.filletArc", {"start": v(-195.87, 118.96) * mm, "mid": v(-195.27, 118.7) * mm, "end": v(-194.7, 119) * mm});
            skPoint(sketch, "E228.visualSharp", {"position": v(-191.38, 123.29) * mm});
            skArc(sketch, "E228.filletArc", {"start": v(-191.94, 122.55) * mm, "mid": v(-191.8, 123.19) * mm, "end": v(-192.2, 123.7) * mm});
            skLineSegment(sketch, "E229", {"start": v(-201.62, 108.04) * mm, "end": v(-199.23, 111.85) * mm});
            skLineSegment(sketch, "E230", {"start": v(-199.6, 112.97) * mm, "end": v(-206.2, 115.52) * mm});
            skLineSegment(sketch, "E231", {"start": v(-207.13, 115.21) * mm, "end": v(-208.08, 113.7) * mm});
            skLineSegment(sketch, "E232", {"start": v(-207.95, 112.73) * mm, "end": v(-202.79, 107.89) * mm});
            skPoint(sketch, "E233.visualSharp", {"position": v(-208.41, 113.16) * mm});
            skArc(sketch, "E233.filletArc", {"start": v(-208.08, 113.7) * mm, "mid": v(-208.19, 113.19) * mm, "end": v(-207.95, 112.73) * mm});
            skPoint(sketch, "E234.visualSharp", {"position": v(-206.8, 115.74) * mm});
            skArc(sketch, "E234.filletArc", {"start": v(-206.2, 115.52) * mm, "mid": v(-206.72, 115.53) * mm, "end": v(-207.13, 115.21) * mm});
            skPoint(sketch, "E235.visualSharp", {"position": v(-202.11, 107.26) * mm});
            skArc(sketch, "E235.filletArc", {"start": v(-202.79, 107.89) * mm, "mid": v(-202.17, 107.69) * mm, "end": v(-201.62, 108.04) * mm});
            skPoint(sketch, "E236.visualSharp", {"position": v(-198.74, 112.63) * mm});
            skArc(sketch, "E236.filletArc", {"start": v(-199.23, 111.85) * mm, "mid": v(-199.15, 112.5) * mm, "end": v(-199.6, 112.97) * mm});
            skLineSegment(sketch, "E237", {"start": v(-207.55, 96.57) * mm, "end": v(-205.44, 100.54) * mm});
            skLineSegment(sketch, "E238", {"start": v(-205.9, 101.63) * mm, "end": v(-212.67, 103.7) * mm});
            skLineSegment(sketch, "E239", {"start": v(-213.57, 103.32) * mm, "end": v(-214.4, 101.74) * mm});
            skLineSegment(sketch, "E240", {"start": v(-214.21, 100.79) * mm, "end": v(-208.7, 96.33) * mm});
            skPoint(sketch, "E241.visualSharp", {"position": v(-214.7, 101.18) * mm});
            skArc(sketch, "E241.filletArc", {"start": v(-214.4, 101.74) * mm, "mid": v(-214.48, 101.23) * mm, "end": v(-214.21, 100.79) * mm});
            skPoint(sketch, "E242.visualSharp", {"position": v(-213.27, 103.87) * mm});
            skArc(sketch, "E242.filletArc", {"start": v(-212.67, 103.7) * mm, "mid": v(-213.19, 103.67) * mm, "end": v(-213.57, 103.32) * mm});
            skPoint(sketch, "E243.visualSharp", {"position": v(-207.99, 95.75) * mm});
            skArc(sketch, "E243.filletArc", {"start": v(-208.7, 96.33) * mm, "mid": v(-208.07, 96.18) * mm, "end": v(-207.55, 96.57) * mm});
            skPoint(sketch, "E244.visualSharp", {"position": v(-205.01, 101.36) * mm});
            skArc(sketch, "E244.filletArc", {"start": v(-205.44, 100.54) * mm, "mid": v(-205.41, 101.2) * mm, "end": v(-205.9, 101.63) * mm});
            skLineSegment(sketch, "E245", {"start": v(-212.95, 83.42) * mm, "end": v(-211.24, 87.58) * mm});
            skLineSegment(sketch, "E246", {"start": v(-211.8, 88.62) * mm, "end": v(-218.75, 90) * mm});
            skLineSegment(sketch, "E247", {"start": v(-219.6, 89.54) * mm, "end": v(-220.28, 87.88) * mm});
            skLineSegment(sketch, "E248", {"start": v(-220, 86.96) * mm, "end": v(-214.07, 83.07) * mm});
            skPoint(sketch, "E249.visualSharp", {"position": v(-220.52, 87.3) * mm});
            skArc(sketch, "E249.filletArc", {"start": v(-220.28, 87.88) * mm, "mid": v(-220.3, 87.37) * mm, "end": v(-220, 86.96) * mm});
            skPoint(sketch, "E250.visualSharp", {"position": v(-219.36, 90.12) * mm});
            skArc(sketch, "E250.filletArc", {"start": v(-218.75, 90) * mm, "mid": v(-219.26, 89.92) * mm, "end": v(-219.6, 89.54) * mm});
            skPoint(sketch, "E251.visualSharp", {"position": v(-213.3, 82.56) * mm});
            skArc(sketch, "E251.filletArc", {"start": v(-214.07, 83.07) * mm, "mid": v(-213.43, 82.98) * mm, "end": v(-212.95, 83.42) * mm});
            skPoint(sketch, "E252.visualSharp", {"position": v(-210.9, 88.44) * mm});
            skArc(sketch, "E252.filletArc", {"start": v(-211.24, 87.58) * mm, "mid": v(-211.28, 88.23) * mm, "end": v(-211.8, 88.62) * mm});
            skLineSegment(sketch, "E253", {"start": v(-216.8, 70.96) * mm, "end": v(-215.46, 75.26) * mm});
            skLineSegment(sketch, "E254", {"start": v(-216.1, 76.24) * mm, "end": v(-223.15, 77.01) * mm});
            skLineSegment(sketch, "E255", {"start": v(-223.96, 76.48) * mm, "end": v(-224.5, 74.77) * mm});
            skLineSegment(sketch, "E256", {"start": v(-224.13, 73.87) * mm, "end": v(-217.89, 70.52) * mm});
            skPoint(sketch, "E257.visualSharp", {"position": v(-224.68, 74.17) * mm});
            skArc(sketch, "E257.filletArc", {"start": v(-224.5, 74.77) * mm, "mid": v(-224.47, 74.26) * mm, "end": v(-224.13, 73.87) * mm});
            skPoint(sketch, "E258.visualSharp", {"position": v(-223.77, 77.08) * mm});
            skArc(sketch, "E258.filletArc", {"start": v(-223.15, 77.01) * mm, "mid": v(-223.65, 76.9) * mm, "end": v(-223.96, 76.48) * mm});
            skPoint(sketch, "E259.visualSharp", {"position": v(-217.07, 70.08) * mm});
            skArc(sketch, "E259.filletArc", {"start": v(-217.89, 70.52) * mm, "mid": v(-217.24, 70.48) * mm, "end": v(-216.8, 70.96) * mm});
            skPoint(sketch, "E260.visualSharp", {"position": v(-215.19, 76.14) * mm});
            skArc(sketch, "E260.filletArc", {"start": v(-215.46, 75.26) * mm, "mid": v(-215.55, 75.9) * mm, "end": v(-216.1, 76.24) * mm});
            skLineSegment(sketch, "E261", {"start": v(-219.88, 56.53) * mm, "end": v(-219.1, 60.97) * mm});
            skLineSegment(sketch, "E262", {"start": v(-219.86, 61.86) * mm, "end": v(-226.94, 61.73) * mm});
            skLineSegment(sketch, "E263", {"start": v(-227.68, 61.1) * mm, "end": v(-228, 59.34) * mm});
            skLineSegment(sketch, "E264", {"start": v(-227.51, 58.5) * mm, "end": v(-220.9, 55.95) * mm});
            skPoint(sketch, "E265.visualSharp", {"position": v(-228.1, 58.72) * mm});
            skArc(sketch, "E265.filletArc", {"start": v(-228, 59.34) * mm, "mid": v(-227.9, 58.83) * mm, "end": v(-227.51, 58.5) * mm});
            skPoint(sketch, "E266.visualSharp", {"position": v(-227.57, 61.72) * mm});
            skArc(sketch, "E266.filletArc", {"start": v(-226.94, 61.73) * mm, "mid": v(-227.42, 61.55) * mm, "end": v(-227.68, 61.1) * mm});
            skPoint(sketch, "E267.visualSharp", {"position": v(-220.04, 55.62) * mm});
            skArc(sketch, "E267.filletArc", {"start": v(-220.9, 55.95) * mm, "mid": v(-220.25, 56) * mm, "end": v(-219.88, 56.53) * mm});
            skPoint(sketch, "E268.visualSharp", {"position": v(-218.94, 61.88) * mm});
            skArc(sketch, "E268.filletArc", {"start": v(-219.1, 60.97) * mm, "mid": v(-219.27, 61.6) * mm, "end": v(-219.86, 61.86) * mm});
            skLineSegment(sketch, "E269", {"start": v(-221.43, 42.99) * mm, "end": v(-221, 47.47) * mm});
            skLineSegment(sketch, "E270", {"start": v(-221.82, 48.3) * mm, "end": v(-228.88, 47.63) * mm});
            skLineSegment(sketch, "E271", {"start": v(-229.56, 46.95) * mm, "end": v(-229.74, 45.17) * mm});
            skLineSegment(sketch, "E272", {"start": v(-229.2, 44.36) * mm, "end": v(-222.41, 42.33) * mm});
            skPoint(sketch, "E273.visualSharp", {"position": v(-229.8, 44.54) * mm});
            skArc(sketch, "E273.filletArc", {"start": v(-229.74, 45.17) * mm, "mid": v(-229.61, 44.67) * mm, "end": v(-229.2, 44.36) * mm});
            skPoint(sketch, "E274.visualSharp", {"position": v(-229.5, 47.57) * mm});
            skArc(sketch, "E274.filletArc", {"start": v(-228.88, 47.63) * mm, "mid": v(-229.34, 47.41) * mm, "end": v(-229.56, 46.95) * mm});
            skPoint(sketch, "E275.visualSharp", {"position": v(-221.52, 42.07) * mm});
            skArc(sketch, "E275.filletArc", {"start": v(-222.41, 42.33) * mm, "mid": v(-221.77, 42.43) * mm, "end": v(-221.43, 42.99) * mm});
            skPoint(sketch, "E276.visualSharp", {"position": v(-220.9, 48.39) * mm});
            skArc(sketch, "E276.filletArc", {"start": v(-221, 47.47) * mm, "mid": v(-221.21, 48.08) * mm, "end": v(-221.82, 48.3) * mm});
            skLineSegment(sketch, "E277", {"start": v(-221.81, 30.28) * mm, "end": v(-221.81, 34.78) * mm});
            skLineSegment(sketch, "E278", {"start": v(-222.72, 35.53) * mm, "end": v(-229.67, 34.18) * mm});
            skLineSegment(sketch, "E279", {"start": v(-230.29, 33.43) * mm, "end": v(-230.29, 31.64) * mm});
            skLineSegment(sketch, "E280", {"start": v(-229.67, 30.89) * mm, "end": v(-222.72, 29.53) * mm});
            skPoint(sketch, "E281.visualSharp", {"position": v(-230.29, 31) * mm});
            skArc(sketch, "E281.filletArc", {"start": v(-230.29, 31.64) * mm, "mid": v(-230.12, 31.15) * mm, "end": v(-229.67, 30.89) * mm});
            skPoint(sketch, "E282.visualSharp", {"position": v(-230.29, 34.06) * mm});
            skArc(sketch, "E282.filletArc", {"start": v(-229.67, 34.18) * mm, "mid": v(-230.12, 33.91) * mm, "end": v(-230.29, 33.43) * mm});
            skPoint(sketch, "E283.visualSharp", {"position": v(-221.81, 29.36) * mm});
            skArc(sketch, "E283.filletArc", {"start": v(-222.72, 29.53) * mm, "mid": v(-222.1, 29.7) * mm, "end": v(-221.81, 30.28) * mm});
            skPoint(sketch, "E284.visualSharp", {"position": v(-221.81, 35.7) * mm});
            skArc(sketch, "E284.filletArc", {"start": v(-221.81, 34.78) * mm, "mid": v(-222.1, 35.37) * mm, "end": v(-222.72, 35.53) * mm});
            skLineSegment(sketch, "E285.MirrorCS", {"start": v(-97.35, -125.62) * mm, "end": v(-99.11, -125.3) * mm});
            skLineSegment(sketch, "E286.MirrorCS", {"start": v(-190.89, -72.53) * mm, "end": v(-192.09, -71.2) * mm});
            skArc(sketch, "E287.MirrorCS", {"start": v(-211.24, -22.56) * mm, "mid": v(-211.28, -23.2) * mm, "end": v(-211.8, -23.6) * mm});
            skArc(sketch, "E288.MirrorCS", {"start": v(-147.55, -99.15) * mm, "mid": v(-147.1, -98.69) * mm, "end": v(-146.45, -98.74) * mm});
            skArc(sketch, "E289.MirrorCS", {"start": v(-99.87, -117.49) * mm, "mid": v(-99.6, -116.9) * mm, "end": v(-98.97, -116.73) * mm});
            skArc(sketch, "E290.MirrorCS", {"start": v(61.72, -46.61) * mm, "mid": v(61.25, -46.16) * mm, "end": v(61.3, -45.5) * mm});
            skArc(sketch, "E291.MirrorCS", {"start": v(-189.93, -72.68) * mm, "mid": v(-190.44, -72.78) * mm, "end": v(-190.89, -72.53) * mm});
            skArc(sketch, "E292.MirrorCS", {"start": v(-96.5, -125.14) * mm, "mid": v(-96.84, -125.53) * mm, "end": v(-97.35, -125.62) * mm});
            skArc(sketch, "E293.MirrorCS", {"start": v(54.25, -68.82) * mm, "mid": v(54.43, -69.3) * mm, "end": v(54.27, -69.8) * mm});
            skArc(sketch, "E294.MirrorCS", {"start": v(-17.8, -118.8) * mm, "mid": v(-17.9, -119.3) * mm, "end": v(-18.3, -119.63) * mm});
            skArc(sketch, "E295.MirrorCS", {"start": v(-192.09, -71.2) * mm, "mid": v(-192.28, -70.73) * mm, "end": v(-192.13, -70.23) * mm});
            skLineSegment(sketch, "E296.MirrorCS", {"start": v(22.48, -99.27) * mm, "end": v(21.03, -100.33) * mm});
            skLineSegment(sketch, "E297.MirrorCS", {"start": v(-33.94, -123.9) * mm, "end": v(-35.7, -124.23) * mm});
            skLineSegment(sketch, "E298.MirrorCS", {"start": v(85.77, -9.3) * mm, "end": v(85.3, -11.03) * mm});
            skLineSegment(sketch, "E299.MirrorCS", {"start": v(-159.78, -100.36) * mm, "end": v(-161.25, -99.33) * mm});
            skLineSegment(sketch, "E300.MirrorCS", {"start": v(-83.1, -127.67) * mm, "end": v(-84.87, -127.43) * mm});
            skLineSegment(sketch, "E301.MirrorCS", {"start": v(54.27, -69.8) * mm, "end": v(53.17, -71.2) * mm});
            skLineSegment(sketch, "E302.MirrorCS", {"start": v(-18.3, -119.63) * mm, "end": v(-20, -120.21) * mm});
            skArc(sketch, "E303.MirrorCS", {"start": v(85.37, -8.41) * mm, "mid": v(85.73, -8.78) * mm, "end": v(85.77, -9.3) * mm});
            skArc(sketch, "E304.MirrorCS", {"start": v(-20, -120.21) * mm, "mid": v(-20.51, -120.2) * mm, "end": v(-20.9, -119.87) * mm});
            skArc(sketch, "E305.MirrorCS", {"start": v(-33.33, -123.14) * mm, "mid": v(-33.5, -123.63) * mm, "end": v(-33.94, -123.9) * mm});
            skArc(sketch, "E306.MirrorCS", {"start": v(-99.11, -125.3) * mm, "mid": v(-99.56, -125.05) * mm, "end": v(-99.74, -124.57) * mm});
            skArc(sketch, "E307.MirrorCS", {"start": v(22.73, -98.34) * mm, "mid": v(22.77, -98.85) * mm, "end": v(22.48, -99.27) * mm});
            skArc(sketch, "E308.MirrorCS", {"start": v(-82.27, -127.16) * mm, "mid": v(-82.6, -127.56) * mm, "end": v(-83.1, -127.67) * mm});
            skArc(sketch, "E309.MirrorCS", {"start": v(53.17, -71.2) * mm, "mid": v(52.73, -71.48) * mm, "end": v(52.22, -71.41) * mm});
            skArc(sketch, "E310.MirrorCS", {"start": v(21.03, -100.33) * mm, "mid": v(20.54, -100.47) * mm, "end": v(20.07, -100.27) * mm});
            skArc(sketch, "E311.MirrorCS", {"start": v(-158.81, -100.29) * mm, "mid": v(-159.28, -100.5) * mm, "end": v(-159.78, -100.36) * mm});
            skArc(sketch, "E312.MirrorCS", {"start": v(-70.31, -128.08) * mm, "mid": v(-70.8, -127.9) * mm, "end": v(-71.06, -127.46) * mm});
            skArc(sketch, "E313.MirrorCS", {"start": v(-35.7, -124.23) * mm, "mid": v(-36.2, -124.16) * mm, "end": v(-36.55, -123.77) * mm});
            skLineSegment(sketch, "E314.MirrorCS", {"start": v(-99.74, -124.57) * mm, "end": v(-99.87, -117.49) * mm});
            skArc(sketch, "E315.MirrorCS", {"start": v(-84.87, -127.43) * mm, "mid": v(-85.33, -127.2) * mm, "end": v(-85.53, -126.73) * mm});
            skArc(sketch, "E316.MirrorCS", {"start": v(-161.25, -99.33) * mm, "mid": v(-161.54, -98.91) * mm, "end": v(-161.5, -98.4) * mm});
            skArc(sketch, "E317.MirrorCS", {"start": v(85.3, -11.03) * mm, "mid": v(85.02, -11.45) * mm, "end": v(84.52, -11.59) * mm});
            skLineSegment(sketch, "E318.MirrorCS", {"start": v(-71.06, -127.46) * mm, "end": v(-72.41, -120.51) * mm});
            skLineSegment(sketch, "E319.MirrorCS", {"start": v(-68.52, -128.08) * mm, "end": v(-70.31, -128.08) * mm});
            skArc(sketch, "E320.MirrorCS", {"start": v(-142.55, -101) * mm, "mid": v(-142.18, -101.53) * mm, "end": v(-142.35, -102.15) * mm});
            skArc(sketch, "E321.MirrorCS", {"start": v(48.42, -63.5) * mm, "mid": v(49, -63.21) * mm, "end": v(49.6, -63.48) * mm});
            skArc(sketch, "E322.MirrorCS", {"start": v(-24.45, -113.74) * mm, "mid": v(-24.5, -113.1) * mm, "end": v(-24.04, -112.64) * mm});
            skArc(sketch, "E323.MirrorCS", {"start": v(-206.2, -50.5) * mm, "mid": v(-206.72, -50.5) * mm, "end": v(-207.13, -50.19) * mm});
            skArc(sketch, "E324.MirrorCS", {"start": v(-208.08, -48.67) * mm, "mid": v(-208.19, -48.16) * mm, "end": v(-207.95, -47.7) * mm});
            skLineSegment(sketch, "E325.MirrorCS", {"start": v(90.63, 17.57) * mm, "end": v(90.47, 15.78) * mm});
            skLineSegment(sketch, "E326.MirrorCS", {"start": v(-110.36, -122.79) * mm, "end": v(-112.09, -122.32) * mm});
            skLineSegment(sketch, "E327.MirrorCS", {"start": v(49.6, -63.48) * mm, "end": v(54.25, -68.82) * mm});
            skLineSegment(sketch, "E328.MirrorCS", {"start": v(-223.96, -11.46) * mm, "end": v(-224.5, -9.75) * mm});
            skLineSegment(sketch, "E329.MirrorCS", {"start": v(-147.96, -107.66) * mm, "end": v(-149.51, -106.76) * mm});
            skLineSegment(sketch, "E330.MirrorCS", {"start": v(-229.56, 18.08) * mm, "end": v(-229.74, 19.86) * mm});
            skLineSegment(sketch, "E331.MirrorCS", {"start": v(-207.13, -50.19) * mm, "end": v(-208.08, -48.67) * mm});
            skArc(sketch, "E332.MirrorCS", {"start": v(-179.2, -74.26) * mm, "mid": v(-178.65, -73.92) * mm, "end": v(-178.04, -74.13) * mm});
            skLineSegment(sketch, "E333.MirrorCS", {"start": v(-146.45, -98.74) * mm, "end": v(-142.55, -101) * mm});
            skArc(sketch, "E334.MirrorCS", {"start": v(90.08, 18.37) * mm, "mid": v(90.5, 18.07) * mm, "end": v(90.63, 17.57) * mm});
            skLineSegment(sketch, "E335.MirrorCS", {"start": v(-24.04, -112.64) * mm, "end": v(-19.78, -111.17) * mm});
            skArc(sketch, "E336.MirrorCS", {"start": v(-67.77, -127.46) * mm, "mid": v(-68.03, -127.9) * mm, "end": v(-68.52, -128.08) * mm});
            skLineSegment(sketch, "E337.MirrorCS", {"start": v(45.65, -67.05) * mm, "end": v(48.42, -63.5) * mm});
            skArc(sketch, "E338.MirrorCS", {"start": v(-228.88, 17.4) * mm, "mid": v(-229.34, 17.61) * mm, "end": v(-229.56, 18.08) * mm});
            skArc(sketch, "E339.MirrorCS", {"start": v(-223.15, -11.99) * mm, "mid": v(-223.65, -11.87) * mm, "end": v(-223.96, -11.46) * mm});
            skArc(sketch, "E340.MirrorCS", {"start": v(-72.41, -120.51) * mm, "mid": v(-72.25, -119.88) * mm, "end": v(-71.67, -119.6) * mm});
            skArc(sketch, "E341.MirrorCS", {"start": v(90.47, 15.78) * mm, "mid": v(90.26, 15.31) * mm, "end": v(89.8, 15.1) * mm});
            skArc(sketch, "E342.MirrorCS", {"start": v(-229.74, 19.86) * mm, "mid": v(-229.61, 20.36) * mm, "end": v(-229.2, 20.67) * mm});
            skLineSegment(sketch, "E343.MirrorCS", {"start": v(-20.9, -119.87) * mm, "end": v(-24.45, -113.74) * mm});
            skArc(sketch, "E344.MirrorCS", {"start": v(-224.5, -9.75) * mm, "mid": v(-224.47, -9.23) * mm, "end": v(-224.13, -8.85) * mm});
            skLineSegment(sketch, "E345.MirrorCS", {"start": v(-71.67, -119.6) * mm, "end": v(-67.16, -119.6) * mm});
            skLineSegment(sketch, "E346.MirrorCS", {"start": v(-66.42, -120.51) * mm, "end": v(-67.77, -127.46) * mm});
            skLineSegment(sketch, "E347.MirrorCS", {"start": v(-221.43, 22.04) * mm, "end": v(-221, 17.56) * mm});
            skLineSegment(sketch, "E348.MirrorCS", {"start": v(-178.04, -74.13) * mm, "end": v(-174.82, -77.27) * mm});
            skLineSegment(sketch, "E349.MirrorCS", {"start": v(-194.7, -53.97) * mm, "end": v(-191.94, -57.53) * mm});
            skLineSegment(sketch, "E350.MirrorCS", {"start": v(-207.55, -31.54) * mm, "end": v(-205.44, -35.52) * mm});
            skLineSegment(sketch, "E351.MirrorCS", {"start": v(81.91, 15.17) * mm, "end": v(82.3, 19.66) * mm});
            skLineSegment(sketch, "E352.MirrorCS", {"start": v(-135.74, -104.44) * mm, "end": v(-131.66, -106.35) * mm});
            skLineSegment(sketch, "E353.MirrorCS", {"start": v(54.04, -56.53) * mm, "end": v(56.62, -52.85) * mm});
            skLineSegment(sketch, "E354.MirrorCS", {"start": v(67.3, -34.47) * mm, "end": v(69.2, -30.39) * mm});
            skLineSegment(sketch, "E355.MirrorCS", {"start": v(-38.66, -116.18) * mm, "end": v(-34.24, -115.31) * mm});
            skLineSegment(sketch, "E356.MirrorCS", {"start": v(14.95, -94.27) * mm, "end": v(18.59, -91.62) * mm});
            skArc(sketch, "E357.MirrorCS", {"start": v(-219.1, 4.06) * mm, "mid": v(-219.27, 3.43) * mm, "end": v(-219.86, 3.17) * mm});
            skArc(sketch, "E358.MirrorCS", {"start": v(-221.81, 30.24) * mm, "mid": v(-222.1, 29.65) * mm, "end": v(-222.72, 29.5) * mm});
            skArc(sketch, "E359.MirrorCS", {"start": v(-164.48, -86.42) * mm, "mid": v(-164.2, -87.01) * mm, "end": v(-164.49, -87.6) * mm});
            skArc(sketch, "E360.MirrorCS", {"start": v(-183.68, -67.87) * mm, "mid": v(-183.5, -68.5) * mm, "end": v(-183.86, -69.03) * mm});
            skArc(sketch, "E361.MirrorCS", {"start": v(-199.23, -46.82) * mm, "mid": v(-199.15, -47.47) * mm, "end": v(-199.6, -47.94) * mm});
            skArc(sketch, "E362.MirrorCS", {"start": v(80.85, 7.7) * mm, "mid": v(81.22, 8.23) * mm, "end": v(81.87, 8.28) * mm});
            skArc(sketch, "E363.MirrorCS", {"start": v(82.9, 34.76) * mm, "mid": v(83.2, 35.34) * mm, "end": v(83.83, 35.47) * mm});
            skArc(sketch, "E364.MirrorCS", {"start": v(-119.74, -111.07) * mm, "mid": v(-119.28, -111.53) * mm, "end": v(-119.35, -112.18) * mm});
            skArc(sketch, "E365.MirrorCS", {"start": v(-94.54, -117.5) * mm, "mid": v(-94.01, -117.88) * mm, "end": v(-93.96, -118.53) * mm});
            skArc(sketch, "E366.MirrorCS", {"start": v(30.12, -82.39) * mm, "mid": v(30.75, -82.2) * mm, "end": v(31.28, -82.57) * mm});
            skArc(sketch, "E367.MirrorCS", {"start": v(63.55, -41.61) * mm, "mid": v(64.09, -41.24) * mm, "end": v(64.71, -41.42) * mm});
            skArc(sketch, "E368.MirrorCS", {"start": v(74.13, -18.21) * mm, "mid": v(74.59, -17.75) * mm, "end": v(75.23, -17.82) * mm});
            skArc(sketch, "E369.MirrorCS", {"start": v(-50.6, -118.32) * mm, "mid": v(-49.98, -118.53) * mm, "end": v(-49.75, -119.13) * mm});
            skArc(sketch, "E370.MirrorCS", {"start": v(-19.78, -111.17) * mm, "mid": v(-19.13, -111.24) * mm, "end": v(-18.78, -111.79) * mm});
            skArc(sketch, "E371.MirrorCS", {"start": v(6.17, -99.41) * mm, "mid": v(6.82, -99.37) * mm, "end": v(7.26, -99.85) * mm});
            skArc(sketch, "E372.MirrorCS", {"start": v(-220.9, 9.07) * mm, "mid": v(-220.25, 9.02) * mm, "end": v(-219.88, 8.5) * mm});
            skArc(sketch, "E373.MirrorCS", {"start": v(-222.72, 35.5) * mm, "mid": v(-222.1, 35.33) * mm, "end": v(-221.81, 34.74) * mm});
            skArc(sketch, "E374.MirrorCS", {"start": v(-169.08, -83.75) * mm, "mid": v(-168.55, -83.37) * mm, "end": v(-167.92, -83.53) * mm});
            skArc(sketch, "E375.MirrorCS", {"start": v(-187.87, -64.57) * mm, "mid": v(-187.3, -64.27) * mm, "end": v(-186.7, -64.52) * mm});
            skArc(sketch, "E376.MirrorCS", {"start": v(80.82, 2.38) * mm, "mid": v(80.23, 2.64) * mm, "end": v(80.06, 3.27) * mm});
            skArc(sketch, "E377.MirrorCS", {"start": v(83.58, 29.48) * mm, "mid": v(82.95, 29.67) * mm, "end": v(82.7, 30.26) * mm});
            skArc(sketch, "E378.MirrorCS", {"start": v(26.8, -86.56) * mm, "mid": v(26.5, -85.98) * mm, "end": v(26.76, -85.38) * mm});
            skArc(sketch, "E379.MirrorCS", {"start": v(45.9, -68.2) * mm, "mid": v(45.51, -67.69) * mm, "end": v(45.65, -67.05) * mm});
            skArc(sketch, "E380.MirrorCS", {"start": v(-55.7, -119.86) * mm, "mid": v(-55.62, -119.21) * mm, "end": v(-55.07, -118.86) * mm});
            skArc(sketch, "E381.MirrorCS", {"start": v(73.18, -23.45) * mm, "mid": v(72.65, -23.09) * mm, "end": v(72.59, -22.44) * mm});
            skArc(sketch, "E382.MirrorCS", {"start": v(2, -102.73) * mm, "mid": v(1.84, -102.1) * mm, "end": v(2.22, -101.57) * mm});
            skArc(sketch, "E383.MirrorCS", {"start": v(-218.75, -24.97) * mm, "mid": v(-219.26, -24.9) * mm, "end": v(-219.6, -24.52) * mm});
            skArc(sketch, "E384.MirrorCS", {"start": v(-229.67, 30.85) * mm, "mid": v(-230.12, 31.11) * mm, "end": v(-230.29, 31.6) * mm});
            skArc(sketch, "E385.MirrorCS", {"start": v(-147, -107.5) * mm, "mid": v(-147.45, -107.75) * mm, "end": v(-147.96, -107.66) * mm});
            skArc(sketch, "E386.MirrorCS", {"start": v(-123, -118.25) * mm, "mid": v(-123.4, -118.57) * mm, "end": v(-123.9, -118.57) * mm});
            skArc(sketch, "E387.MirrorCS", {"start": v(34.9, -88.66) * mm, "mid": v(35, -89.17) * mm, "end": v(34.75, -89.62) * mm});
            skArc(sketch, "E388.MirrorCS", {"start": v(70.06, -46.07) * mm, "mid": v(70.3, -46.52) * mm, "end": v(70.22, -47.02) * mm});
            skArc(sketch, "E389.MirrorCS", {"start": v(81.3, -21.47) * mm, "mid": v(81.63, -21.87) * mm, "end": v(81.63, -22.38) * mm});
            skArc(sketch, "E390.MirrorCS", {"start": v(9.41, -106.6) * mm, "mid": v(9.4, -107.11) * mm, "end": v(9.05, -107.5) * mm});
            skArc(sketch, "E391.MirrorCS", {"start": v(-220.28, -22.86) * mm, "mid": v(-220.3, -22.34) * mm, "end": v(-220, -21.93) * mm});
            skArc(sketch, "E392.MirrorCS", {"start": v(-230.29, 33.39) * mm, "mid": v(-230.12, 33.87) * mm, "end": v(-229.67, 34.14) * mm});
            skArc(sketch, "E393.MirrorCS", {"start": v(-149.51, -106.76) * mm, "mid": v(-149.84, -106.37) * mm, "end": v(-149.85, -105.85) * mm});
            skLineSegment(sketch, "E394.MirrorCS", {"start": v(19.73, -91.92) * mm, "end": v(22.73, -98.34) * mm});
            skLineSegment(sketch, "E395.MirrorCS", {"start": v(-33.34, -116.06) * mm, "end": v(-33.33, -123.14) * mm});
            skLineSegment(sketch, "E396.MirrorCS", {"start": v(83.27, 20.32) * mm, "end": v(90.08, 18.37) * mm});
            skLineSegment(sketch, "E397.MirrorCS", {"start": v(70.35, -30.1) * mm, "end": v(76.07, -34.26) * mm});
            skLineSegment(sketch, "E398.MirrorCS", {"start": v(-131.36, -107.49) * mm, "end": v(-135.53, -113.21) * mm});
            skLineSegment(sketch, "E399.MirrorCS", {"start": v(-80.02, -120.44) * mm, "end": v(-82.27, -127.16) * mm});
            skLineSegment(sketch, "E400.MirrorCS", {"start": v(-192.2, -58.68) * mm, "end": v(-198.53, -61.85) * mm});
            skLineSegment(sketch, "E401.MirrorCS", {"start": v(-174.92, -78.45) * mm, "end": v(-180.74, -82.47) * mm});
            skLineSegment(sketch, "E402.MirrorCS", {"start": v(-221.82, 16.73) * mm, "end": v(-228.88, 17.4) * mm});
            skLineSegment(sketch, "E403.MirrorCS", {"start": v(44.87, -80.39) * mm, "end": v(43.6, -81.66) * mm});
            skLineSegment(sketch, "E404.MirrorCS", {"start": v(-4, -114.04) * mm, "end": v(-5.64, -114.78) * mm});
            skLineSegment(sketch, "E405.MirrorCS", {"start": v(76.32, -35.2) * mm, "end": v(75.56, -36.82) * mm});
            skLineSegment(sketch, "E406.MirrorCS", {"start": v(62.79, -58.82) * mm, "end": v(61.76, -60.29) * mm});
            skLineSegment(sketch, "E407.MirrorCS", {"start": v(-136.47, -113.46) * mm, "end": v(-138.1, -112.7) * mm});
            skLineSegment(sketch, "E408.MirrorCS", {"start": v(31.28, -82.57) * mm, "end": v(34.9, -88.66) * mm});
            skLineSegment(sketch, "E409.MirrorCS", {"start": v(7.26, -99.85) * mm, "end": v(9.41, -106.6) * mm});
            skLineSegment(sketch, "E410.MirrorCS", {"start": v(-18.78, -111.79) * mm, "end": v(-17.8, -118.8) * mm});
            skLineSegment(sketch, "E411.MirrorCS", {"start": v(75.23, -17.82) * mm, "end": v(81.3, -21.47) * mm});
            skLineSegment(sketch, "E412.MirrorCS", {"start": v(64.71, -41.42) * mm, "end": v(70.06, -46.07) * mm});
            skLineSegment(sketch, "E413.MirrorCS", {"start": v(-93.96, -118.53) * mm, "end": v(-96.5, -125.14) * mm});
            skLineSegment(sketch, "E414.MirrorCS", {"start": v(-119.35, -112.18) * mm, "end": v(-123, -118.25) * mm});
            skLineSegment(sketch, "E415.MirrorCS", {"start": v(-211.8, -23.6) * mm, "end": v(-218.75, -24.97) * mm});
            skLineSegment(sketch, "E416.MirrorCS", {"start": v(-199.6, -47.94) * mm, "end": v(-206.2, -50.5) * mm});
            skLineSegment(sketch, "E417.MirrorCS", {"start": v(-183.86, -69.03) * mm, "end": v(-189.93, -72.68) * mm});
            skLineSegment(sketch, "E418.MirrorCS", {"start": v(-213.57, -38.3) * mm, "end": v(-214.4, -36.7) * mm});
            skLineSegment(sketch, "E419.MirrorCS", {"start": v(-222.72, 29.5) * mm, "end": v(-229.67, 30.85) * mm});
            skLineSegment(sketch, "E420.MirrorCS", {"start": v(34.75, -89.62) * mm, "end": v(33.4, -90.81) * mm});
            skLineSegment(sketch, "E421.MirrorCS", {"start": v(9.05, -107.5) * mm, "end": v(7.48, -108.36) * mm});
            skLineSegment(sketch, "E422.MirrorCS", {"start": v(81.63, -22.38) * mm, "end": v(81.01, -24.07) * mm});
            skLineSegment(sketch, "E423.MirrorCS", {"start": v(70.22, -47.02) * mm, "end": v(69.32, -48.57) * mm});
            skLineSegment(sketch, "E424.MirrorCS", {"start": v(-123.9, -118.57) * mm, "end": v(-125.6, -117.96) * mm});
            skLineSegment(sketch, "E425.MirrorCS", {"start": v(-199.48, -61.64) * mm, "end": v(-200.57, -60.22) * mm});
            skLineSegment(sketch, "E426.MirrorCS", {"start": v(-181.7, -82.4) * mm, "end": v(-182.99, -81.14) * mm});
            skLineSegment(sketch, "E427.MirrorCS", {"start": v(-219.6, -24.52) * mm, "end": v(-220.28, -22.86) * mm});
            skLineSegment(sketch, "E428.MirrorCS", {"start": v(20.07, -100.27) * mm, "end": v(14.88, -95.45) * mm});
            skLineSegment(sketch, "E429.MirrorCS", {"start": v(-6.58, -114.52) * mm, "end": v(-10.66, -108.73) * mm});
            skLineSegment(sketch, "E430.MirrorCS", {"start": v(-36.55, -123.77) * mm, "end": v(-39.22, -117.21) * mm});
            skLineSegment(sketch, "E431.MirrorCS", {"start": v(89.8, 15.1) * mm, "end": v(82.75, 14.35) * mm});
            skLineSegment(sketch, "E432.MirrorCS", {"start": v(-230.29, 31.6) * mm, "end": v(-230.29, 33.39) * mm});
            skArc(sketch, "E433.MirrorCS", {"start": v(69.32, -48.57) * mm, "mid": v(68.93, -48.9) * mm, "end": v(68.41, -48.91) * mm});
            skArc(sketch, "E434.MirrorCS", {"start": v(62.71, -57.85) * mm, "mid": v(62.92, -58.32) * mm, "end": v(62.79, -58.82) * mm});
            skArc(sketch, "E435.MirrorCS", {"start": v(76.07, -34.26) * mm, "mid": v(76.36, -34.68) * mm, "end": v(76.32, -35.2) * mm});
            skLineSegment(sketch, "E436.MirrorCS", {"start": v(-123.97, -109.53) * mm, "end": v(-119.74, -111.07) * mm});
            skLineSegment(sketch, "E437.MirrorCS", {"start": v(-167.92, -83.53) * mm, "end": v(-164.48, -86.42) * mm});
            skLineSegment(sketch, "E438.MirrorCS", {"start": v(61.3, -45.5) * mm, "end": v(63.55, -41.61) * mm});
            skLineSegment(sketch, "E439.MirrorCS", {"start": v(-186.7, -64.52) * mm, "end": v(-183.68, -67.87) * mm});
            skArc(sketch, "E440.MirrorCS", {"start": v(-3.58, -113.17) * mm, "mid": v(-3.64, -113.68) * mm, "end": v(-4, -114.04) * mm});
            skLineSegment(sketch, "E441.MirrorCS", {"start": v(-219.88, 8.5) * mm, "end": v(-219.1, 4.06) * mm});
            skArc(sketch, "E442.MirrorCS", {"start": v(-195.87, -53.93) * mm, "mid": v(-195.27, -53.67) * mm, "end": v(-194.7, -53.97) * mm});
            skLineSegment(sketch, "E443.MirrorCS", {"start": v(-98.97, -116.73) * mm, "end": v(-94.54, -117.5) * mm});
            skArc(sketch, "E444.MirrorCS", {"start": v(44.97, -79.42) * mm, "mid": v(45.1, -79.92) * mm, "end": v(44.87, -80.39) * mm});
            skLineSegment(sketch, "E445.MirrorCS", {"start": v(72.59, -22.44) * mm, "end": v(74.13, -18.21) * mm});
            skLineSegment(sketch, "E446.MirrorCS", {"start": v(80.06, 3.27) * mm, "end": v(80.85, 7.7) * mm});
            skLineSegment(sketch, "E447.MirrorCS", {"start": v(2.22, -101.57) * mm, "end": v(6.17, -99.41) * mm});
            skLineSegment(sketch, "E448.MirrorCS", {"start": v(82.7, 30.26) * mm, "end": v(82.9, 34.76) * mm});
            skArc(sketch, "E449.MirrorCS", {"start": v(-208.7, -31.3) * mm, "mid": v(-208.07, -31.15) * mm, "end": v(-207.55, -31.54) * mm});
            skArc(sketch, "E450.MirrorCS", {"start": v(-125.6, -117.96) * mm, "mid": v(-125.99, -117.63) * mm, "end": v(-126.08, -117.12) * mm});
            skArc(sketch, "E451.MirrorCS", {"start": v(-174.82, -77.27) * mm, "mid": v(-174.59, -77.88) * mm, "end": v(-174.92, -78.45) * mm});
            skArc(sketch, "E452.MirrorCS", {"start": v(-191.94, -57.53) * mm, "mid": v(-191.8, -58.16) * mm, "end": v(-192.2, -58.68) * mm});
            skArc(sketch, "E453.MirrorCS", {"start": v(-80.64, -119.44) * mm, "mid": v(-80.1, -119.8) * mm, "end": v(-80.02, -120.44) * mm});
            skArc(sketch, "E454.MirrorCS", {"start": v(-131.66, -106.35) * mm, "mid": v(-131.24, -106.85) * mm, "end": v(-131.36, -107.49) * mm});
            skArc(sketch, "E455.MirrorCS", {"start": v(33.4, -90.81) * mm, "mid": v(32.93, -91) * mm, "end": v(32.44, -90.85) * mm});
            skLineSegment(sketch, "E456.MirrorCS", {"start": v(-55.07, -118.86) * mm, "end": v(-50.6, -118.32) * mm});
            skLineSegment(sketch, "E457.MirrorCS", {"start": v(26.76, -85.38) * mm, "end": v(30.12, -82.39) * mm});
            skArc(sketch, "E458.MirrorCS", {"start": v(69.2, -30.39) * mm, "mid": v(69.7, -29.97) * mm, "end": v(70.35, -30.1) * mm});
            skArc(sketch, "E459.MirrorCS", {"start": v(-34.24, -115.31) * mm, "mid": v(-33.61, -115.47) * mm, "end": v(-33.34, -116.06) * mm});
            skArc(sketch, "E460.MirrorCS", {"start": v(82.3, 19.66) * mm, "mid": v(82.63, 20.22) * mm, "end": v(83.27, 20.32) * mm});
            skArc(sketch, "E461.MirrorCS", {"start": v(-180.74, -82.47) * mm, "mid": v(-181.24, -82.6) * mm, "end": v(-181.7, -82.4) * mm});
            skArc(sketch, "E462.MirrorCS", {"start": v(-212.67, -38.66) * mm, "mid": v(-213.19, -38.64) * mm, "end": v(-213.57, -38.3) * mm});
            skArc(sketch, "E463.MirrorCS", {"start": v(-109.47, -122.39) * mm, "mid": v(-109.84, -122.74) * mm, "end": v(-110.36, -122.79) * mm});
            skArc(sketch, "E464.MirrorCS", {"start": v(-221, 17.56) * mm, "mid": v(-221.21, 16.95) * mm, "end": v(-221.82, 16.73) * mm});
            skArc(sketch, "E465.MirrorCS", {"start": v(-198.53, -61.85) * mm, "mid": v(-199.04, -61.92) * mm, "end": v(-199.48, -61.64) * mm});
            skArc(sketch, "E466.MirrorCS", {"start": v(-6.24, -105.75) * mm, "mid": v(-5.6, -105.77) * mm, "end": v(-5.2, -106.28) * mm});
            skArc(sketch, "E467.MirrorCS", {"start": v(18.59, -91.62) * mm, "mid": v(19.23, -91.5) * mm, "end": v(19.73, -91.92) * mm});
            skArc(sketch, "E468.MirrorCS", {"start": v(-136.8, -104.95) * mm, "mid": v(-136.39, -104.45) * mm, "end": v(-135.74, -104.44) * mm});
            skArc(sketch, "E469.MirrorCS", {"start": v(-67.16, -119.6) * mm, "mid": v(-66.58, -119.88) * mm, "end": v(-66.42, -120.51) * mm});
            skArc(sketch, "E470.MirrorCS", {"start": v(-5.64, -114.78) * mm, "mid": v(-6.16, -114.82) * mm, "end": v(-6.58, -114.52) * mm});
            skArc(sketch, "E471.MirrorCS", {"start": v(-135.53, -113.21) * mm, "mid": v(-135.95, -113.5) * mm, "end": v(-136.47, -113.46) * mm});
            skArc(sketch, "E472.MirrorCS", {"start": v(-10.66, -108.73) * mm, "mid": v(-10.77, -108.1) * mm, "end": v(-10.35, -107.6) * mm});
            skLineSegment(sketch, "E473.MirrorCS", {"start": v(-221.81, 34.74) * mm, "end": v(-221.81, 30.24) * mm});
            skArc(sketch, "E474.MirrorCS", {"start": v(54.35, -57.67) * mm, "mid": v(53.93, -57.17) * mm, "end": v(54.04, -56.53) * mm});
            skLineSegment(sketch, "E475.MirrorCS", {"start": v(-229.2, 20.67) * mm, "end": v(-222.41, 22.7) * mm});
            skLineSegment(sketch, "E476.MirrorCS", {"start": v(80.18, -24.56) * mm, "end": v(73.18, -23.45) * mm});
            skArc(sketch, "E477.MirrorCS", {"start": v(14.88, -95.45) * mm, "mid": v(14.64, -94.84) * mm, "end": v(14.95, -94.27) * mm});
            skArc(sketch, "E478.MirrorCS", {"start": v(-39.22, -117.21) * mm, "mid": v(-39.18, -116.56) * mm, "end": v(-38.66, -116.18) * mm});
            skArc(sketch, "E479.MirrorCS", {"start": v(7.48, -108.36) * mm, "mid": v(6.97, -108.44) * mm, "end": v(6.53, -108.18) * mm});
            skLineSegment(sketch, "E480.MirrorCS", {"start": v(-138.5, -111.82) * mm, "end": v(-136.8, -104.95) * mm});
            skLineSegment(sketch, "E481.MirrorCS", {"start": v(-149.85, -105.85) * mm, "end": v(-147.55, -99.15) * mm});
            skLineSegment(sketch, "E482.MirrorCS", {"start": v(68.41, -48.91) * mm, "end": v(61.72, -46.61) * mm});
            skLineSegment(sketch, "E483.MirrorCS", {"start": v(6.53, -108.18) * mm, "end": v(2, -102.73) * mm});
            skArc(sketch, "E484.MirrorCS", {"start": v(82.75, 14.35) * mm, "mid": v(82.14, 14.56) * mm, "end": v(81.91, 15.17) * mm});
            skArc(sketch, "E485.MirrorCS", {"start": v(43.6, -81.66) * mm, "mid": v(43.14, -81.88) * mm, "end": v(42.64, -81.75) * mm});
            skArc(sketch, "E486.MirrorCS", {"start": v(81.01, -24.07) * mm, "mid": v(80.69, -24.46) * mm, "end": v(80.18, -24.56) * mm});
            skArc(sketch, "E487.MirrorCS", {"start": v(-222.41, 22.7) * mm, "mid": v(-221.77, 22.6) * mm, "end": v(-221.43, 22.04) * mm});
            skArc(sketch, "E488.MirrorCS", {"start": v(-182.99, -81.14) * mm, "mid": v(-183.21, -80.68) * mm, "end": v(-183.1, -80.18) * mm});
            skArc(sketch, "E489.MirrorCS", {"start": v(-214.4, -36.7) * mm, "mid": v(-214.48, -36.2) * mm, "end": v(-214.21, -35.76) * mm});
            skArc(sketch, "E490.MirrorCS", {"start": v(-200.57, -60.22) * mm, "mid": v(-200.73, -59.73) * mm, "end": v(-200.54, -59.25) * mm});
            skArc(sketch, "E491.MirrorCS", {"start": v(75.56, -36.82) * mm, "mid": v(75.2, -37.19) * mm, "end": v(74.69, -37.24) * mm});
            skLineSegment(sketch, "E492.MirrorCS", {"start": v(60.82, -60.54) * mm, "end": v(54.35, -57.67) * mm});
            skArc(sketch, "E493.MirrorCS", {"start": v(-138.1, -112.7) * mm, "mid": v(-138.46, -112.34) * mm, "end": v(-138.5, -111.82) * mm});
            skArc(sketch, "E494.MirrorCS", {"start": v(-112.09, -122.32) * mm, "mid": v(-112.5, -122.03) * mm, "end": v(-112.65, -121.53) * mm});
            skArc(sketch, "E495.MirrorCS", {"start": v(61.76, -60.29) * mm, "mid": v(61.34, -60.58) * mm, "end": v(60.82, -60.54) * mm});
            skLineSegment(sketch, "E496.MirrorCS", {"start": v(-229.67, 34.14) * mm, "end": v(-222.72, 35.5) * mm});
            skLineSegment(sketch, "E497.MirrorCS", {"start": v(-183.1, -80.18) * mm, "end": v(-179.2, -74.26) * mm});
            skLineSegment(sketch, "E498.MirrorCS", {"start": v(-214.21, -35.76) * mm, "end": v(-208.7, -31.3) * mm});
            skLineSegment(sketch, "E499.MirrorCS", {"start": v(52.22, -71.41) * mm, "end": v(45.9, -68.2) * mm});
            skLineSegment(sketch, "E500.MirrorCS", {"start": v(-216.8, -5.94) * mm, "end": v(-215.46, -10.24) * mm});
            skLineSegment(sketch, "E501.MirrorCS", {"start": v(-157.5, -91.61) * mm, "end": v(-153.8, -94.2) * mm});
            skLineSegment(sketch, "E502.MirrorCS", {"start": v(-85.1, -118.85) * mm, "end": v(-80.64, -119.44) * mm});
            skLineSegment(sketch, "E503.MirrorCS", {"start": v(-111.2, -113.79) * mm, "end": v(-106.85, -114.95) * mm});
            skLineSegment(sketch, "E504.MirrorCS", {"start": v(36.65, -76.62) * mm, "end": v(39.84, -73.44) * mm});
            skLineSegment(sketch, "E505.MirrorCS", {"start": v(76.77, -10.14) * mm, "end": v(77.93, -5.8) * mm});
            skLineSegment(sketch, "E506.MirrorCS", {"start": v(-10.35, -107.6) * mm, "end": v(-6.24, -105.75) * mm});
            skArc(sketch, "E507.MirrorCS", {"start": v(-214.07, -18.04) * mm, "mid": v(-213.43, -17.95) * mm, "end": v(-212.95, -18.4) * mm});
            skArc(sketch, "E508.MirrorCS", {"start": v(-202.79, -42.86) * mm, "mid": v(-202.17, -42.66) * mm, "end": v(-201.62, -43.01) * mm});
            skArc(sketch, "E509.MirrorCS", {"start": v(-124.98, -110.13) * mm, "mid": v(-124.61, -109.59) * mm, "end": v(-123.97, -109.53) * mm});
            skArc(sketch, "E510.MirrorCS", {"start": v(-226.94, 3.3) * mm, "mid": v(-227.42, 3.48) * mm, "end": v(-227.68, 3.92) * mm});
            skArc(sketch, "E511.MirrorCS", {"start": v(-170, -92.06) * mm, "mid": v(-170.48, -92.23) * mm, "end": v(-170.96, -92.05) * mm});
            skArc(sketch, "E512.MirrorCS", {"start": v(88.48, 5.73) * mm, "mid": v(88.87, 5.4) * mm, "end": v(88.96, 4.88) * mm});
            skArc(sketch, "E513.MirrorCS", {"start": v(90.72, 33.82) * mm, "mid": v(91.15, 33.54) * mm, "end": v(91.3, 33.05) * mm});
            skArc(sketch, "E514.MirrorCS", {"start": v(-50.26, -126.2) * mm, "mid": v(-50.46, -126.67) * mm, "end": v(-50.92, -126.9) * mm});
            skArc(sketch, "E515.MirrorCS", {"start": v(-228, 5.69) * mm, "mid": v(-227.9, 6.2) * mm, "end": v(-227.51, 6.53) * mm});
            skArc(sketch, "E516.MirrorCS", {"start": v(-172.34, -90.9) * mm, "mid": v(-172.6, -90.45) * mm, "end": v(-172.51, -89.94) * mm});
            skLineSegment(sketch, "E517.MirrorCS", {"start": v(41, -73.55) * mm, "end": v(44.97, -79.42) * mm});
            skLineSegment(sketch, "E518.MirrorCS", {"start": v(-5.2, -106.28) * mm, "end": v(-3.58, -113.17) * mm});
            skLineSegment(sketch, "E519.MirrorCS", {"start": v(79, -5.3) * mm, "end": v(85.37, -8.41) * mm});
            skLineSegment(sketch, "E520.MirrorCS", {"start": v(57.8, -52.75) * mm, "end": v(62.71, -57.85) * mm});
            skLineSegment(sketch, "E521.MirrorCS", {"start": v(-153.72, -95.37) * mm, "end": v(-158.81, -100.29) * mm});
            skLineSegment(sketch, "E522.MirrorCS", {"start": v(-106.37, -116.02) * mm, "end": v(-109.47, -122.39) * mm});
            skLineSegment(sketch, "E523.MirrorCS", {"start": v(-216.1, -11.22) * mm, "end": v(-223.15, -11.99) * mm});
            skLineSegment(sketch, "E524.MirrorCS", {"start": v(-205.9, -36.6) * mm, "end": v(-212.67, -38.66) * mm});
            skArc(sketch, "E525.MirrorCS", {"start": v(88.64, 3.12) * mm, "mid": v(88.39, 2.67) * mm, "end": v(87.9, 2.5) * mm});
            skArc(sketch, "E526.MirrorCS", {"start": v(91.23, 31.26) * mm, "mid": v(91.03, 30.78) * mm, "end": v(90.58, 30.54) * mm});
            skLineSegment(sketch, "E527.MirrorCS", {"start": v(-49.75, -119.13) * mm, "end": v(-50.26, -126.2) * mm});
            skLineSegment(sketch, "E528.MirrorCS", {"start": v(83.83, 35.47) * mm, "end": v(90.72, 33.82) * mm});
            skLineSegment(sketch, "E529.MirrorCS", {"start": v(81.87, 8.28) * mm, "end": v(88.48, 5.73) * mm});
            skLineSegment(sketch, "E530.MirrorCS", {"start": v(-164.49, -87.6) * mm, "end": v(-170, -92.06) * mm});
            skLineSegment(sketch, "E531.MirrorCS", {"start": v(-142.35, -102.15) * mm, "end": v(-147, -107.5) * mm});
            skLineSegment(sketch, "E532.MirrorCS", {"start": v(-219.86, 3.17) * mm, "end": v(-226.94, 3.3) * mm});
            skLineSegment(sketch, "E533.MirrorCS", {"start": v(-50.92, -126.9) * mm, "end": v(-52.7, -127.12) * mm});
            skLineSegment(sketch, "E534.MirrorCS", {"start": v(91.3, 33.05) * mm, "end": v(91.23, 31.26) * mm});
            skLineSegment(sketch, "E535.MirrorCS", {"start": v(88.96, 4.88) * mm, "end": v(88.64, 3.12) * mm});
            skLineSegment(sketch, "E536.MirrorCS", {"start": v(-170.96, -92.05) * mm, "end": v(-172.34, -90.9) * mm});
            skLineSegment(sketch, "E537.MirrorCS", {"start": v(-227.68, 3.92) * mm, "end": v(-228, 5.69) * mm});
            skLineSegment(sketch, "E538.MirrorCS", {"start": v(42.64, -81.75) * mm, "end": v(36.77, -77.79) * mm});
            skArc(sketch, "E539.MirrorCS", {"start": v(-52.7, -127.12) * mm, "mid": v(-53.2, -127) * mm, "end": v(-53.52, -126.6) * mm});
            skLineSegment(sketch, "E540.MirrorCS", {"start": v(-201.62, -43.01) * mm, "end": v(-199.23, -46.82) * mm});
            skLineSegment(sketch, "E541.MirrorCS", {"start": v(-212.95, -18.4) * mm, "end": v(-211.24, -22.56) * mm});
            skArc(sketch, "E542.MirrorCS", {"start": v(-217.89, -5.5) * mm, "mid": v(-217.24, -5.46) * mm, "end": v(-216.8, -5.94) * mm});
            skArc(sketch, "E543.MirrorCS", {"start": v(-205.44, -35.52) * mm, "mid": v(-205.41, -36.17) * mm, "end": v(-205.9, -36.6) * mm});
            skArc(sketch, "E544.MirrorCS", {"start": v(-215.46, -10.24) * mm, "mid": v(-215.55, -10.88) * mm, "end": v(-216.1, -11.22) * mm});
            skArc(sketch, "E545.MirrorCS", {"start": v(-106.85, -114.95) * mm, "mid": v(-106.36, -115.37) * mm, "end": v(-106.37, -116.02) * mm});
            skArc(sketch, "E546.MirrorCS", {"start": v(-153.8, -94.2) * mm, "mid": v(-153.49, -94.76) * mm, "end": v(-153.72, -95.37) * mm});
            skArc(sketch, "E547.MirrorCS", {"start": v(56.62, -52.85) * mm, "mid": v(57.18, -52.52) * mm, "end": v(57.8, -52.75) * mm});
            skArc(sketch, "E548.MirrorCS", {"start": v(77.93, -5.8) * mm, "mid": v(78.36, -5.3) * mm, "end": v(79, -5.3) * mm});
            skArc(sketch, "E549.MirrorCS", {"start": v(39.84, -73.44) * mm, "mid": v(40.45, -73.22) * mm, "end": v(41, -73.55) * mm});
            skArc(sketch, "E550.MirrorCS", {"start": v(-85.96, -119.66) * mm, "mid": v(-85.72, -119.05) * mm, "end": v(-85.1, -118.85) * mm});
            skArc(sketch, "E551.MirrorCS", {"start": v(-112.16, -114.47) * mm, "mid": v(-111.84, -113.9) * mm, "end": v(-111.2, -113.79) * mm});
            skArc(sketch, "E552.MirrorCS", {"start": v(-158.63, -91.93) * mm, "mid": v(-158.14, -91.5) * mm, "end": v(-157.5, -91.61) * mm});
            skArc(sketch, "E553.MirrorCS", {"start": v(67.81, -35.53) * mm, "mid": v(67.3, -35.12) * mm, "end": v(67.3, -34.47) * mm});
            skArc(sketch, "E554.MirrorCS", {"start": v(77.45, -11.1) * mm, "mid": v(76.89, -10.78) * mm, "end": v(76.77, -10.14) * mm});
            skArc(sketch, "E555.MirrorCS", {"start": v(36.77, -77.79) * mm, "mid": v(36.43, -77.23) * mm, "end": v(36.65, -76.62) * mm});
            skLineSegment(sketch, "E556.MirrorCS", {"start": v(87.9, 2.5) * mm, "end": v(80.82, 2.38) * mm});
            skLineSegment(sketch, "E557.MirrorCS", {"start": v(90.58, 30.54) * mm, "end": v(83.58, 29.48) * mm});
            skLineSegment(sketch, "E558.MirrorCS", {"start": v(74.69, -37.24) * mm, "end": v(67.81, -35.53) * mm});
            skLineSegment(sketch, "E559.MirrorCS", {"start": v(-53.52, -126.6) * mm, "end": v(-55.7, -119.86) * mm});
            skLineSegment(sketch, "E560.MirrorCS", {"start": v(-112.65, -121.53) * mm, "end": v(-112.16, -114.47) * mm});
            skLineSegment(sketch, "E561.MirrorCS", {"start": v(-161.5, -98.4) * mm, "end": v(-158.63, -91.93) * mm});
            skLineSegment(sketch, "E562.MirrorCS", {"start": v(84.52, -11.59) * mm, "end": v(77.45, -11.1) * mm});
            skLineSegment(sketch, "E563.MirrorCS", {"start": v(-220, -21.93) * mm, "end": v(-214.07, -18.04) * mm});
            skLineSegment(sketch, "E564.MirrorCS", {"start": v(-200.54, -59.25) * mm, "end": v(-195.87, -53.93) * mm});
            skLineSegment(sketch, "E565.MirrorCS", {"start": v(-207.95, -47.7) * mm, "end": v(-202.79, -42.86) * mm});
            skLineSegment(sketch, "E566.MirrorCS", {"start": v(-85.53, -126.73) * mm, "end": v(-85.96, -119.66) * mm});
            skLineSegment(sketch, "E567.MirrorCS", {"start": v(-227.51, 6.53) * mm, "end": v(-220.9, 9.07) * mm});
            skLineSegment(sketch, "E568.MirrorCS", {"start": v(-172.51, -89.94) * mm, "end": v(-169.08, -83.75) * mm});
            skLineSegment(sketch, "E569.MirrorCS", {"start": v(-192.13, -70.23) * mm, "end": v(-187.87, -64.57) * mm});
            skLineSegment(sketch, "E570.MirrorCS", {"start": v(-126.08, -117.12) * mm, "end": v(-124.98, -110.13) * mm});
            skLineSegment(sketch, "E571.MirrorCS", {"start": v(32.44, -90.85) * mm, "end": v(26.8, -86.56) * mm});
            skLineSegment(sketch, "E572.MirrorCS", {"start": v(-224.13, -8.85) * mm, "end": v(-217.89, -5.5) * mm});
            skPoint(sketch, "E573.MirrorP", {"position": v(-70.94, -128.08) * mm});
            skPoint(sketch, "E574.MirrorP", {"position": v(-72.6, -119.6) * mm});
            skPoint(sketch, "E575.MirrorP", {"position": v(-67.9, -128.08) * mm});
            skPoint(sketch, "E576.MirrorP", {"position": v(-141.75, -101.45) * mm});
            skPoint(sketch, "E577.MirrorP", {"position": v(-163.77, -87.02) * mm});
            skPoint(sketch, "E578.MirrorP", {"position": v(-183.07, -68.55) * mm});
            skPoint(sketch, "E579.MirrorP", {"position": v(81, 8.61) * mm});
            skPoint(sketch, "E580.MirrorP", {"position": v(-93.63, -117.67) * mm});
            skPoint(sketch, "E581.MirrorP", {"position": v(-118.87, -111.38) * mm});
            skPoint(sketch, "E582.MirrorP", {"position": v(30.81, -81.77) * mm});
            skPoint(sketch, "E583.MirrorP", {"position": v(49, -62.78) * mm});
            skPoint(sketch, "E584.MirrorP", {"position": v(64.02, -40.81) * mm});
            skPoint(sketch, "E585.MirrorP", {"position": v(74.44, -17.34) * mm});
            skPoint(sketch, "E586.MirrorP", {"position": v(-49.68, -118.21) * mm});
            skPoint(sketch, "E587.MirrorP", {"position": v(-18.9, -110.87) * mm});
            skPoint(sketch, "E588.MirrorP", {"position": v(6.98, -98.97) * mm});
            skPoint(sketch, "E589.MirrorP", {"position": v(-198.74, -47.6) * mm});
            skPoint(sketch, "E590.MirrorP", {"position": v(-210.9, -23.41) * mm});
            skPoint(sketch, "E591.MirrorP", {"position": v(-218.94, 3.15) * mm});
            skPoint(sketch, "E592.MirrorP", {"position": v(-221.81, 29.32) * mm});
            skPoint(sketch, "E593.MirrorP", {"position": v(-147.25, -98.28) * mm});
            skPoint(sketch, "E594.MirrorP", {"position": v(-168.63, -82.94) * mm});
            skPoint(sketch, "E595.MirrorP", {"position": v(79.9, 2.36) * mm});
            skPoint(sketch, "E596.MirrorP", {"position": v(-187.31, -63.84) * mm});
            skPoint(sketch, "E597.MirrorP", {"position": v(-99.88, -116.56) * mm});
            skPoint(sketch, "E598.MirrorP", {"position": v(82.66, 29.34) * mm});
            skPoint(sketch, "E599.MirrorP", {"position": v(-124.84, -109.21) * mm});
            skPoint(sketch, "E600.MirrorP", {"position": v(26.07, -86) * mm});
            skPoint(sketch, "E601.MirrorP", {"position": v(45.09, -67.78) * mm});
            skPoint(sketch, "E602.MirrorP", {"position": v(60.84, -46.3) * mm});
            skPoint(sketch, "E603.MirrorP", {"position": v(72.27, -23.3) * mm});
            skPoint(sketch, "E604.MirrorP", {"position": v(-55.98, -118.98) * mm});
            skPoint(sketch, "E605.MirrorP", {"position": v(-24.91, -112.94) * mm});
            skPoint(sketch, "E606.MirrorP", {"position": v(1.41, -102.01) * mm});
            skPoint(sketch, "E607.MirrorP", {"position": v(-202.11, -42.23) * mm});
            skPoint(sketch, "E608.MirrorP", {"position": v(-213.3, -17.54) * mm});
            skPoint(sketch, "E609.MirrorP", {"position": v(-220.04, 9.4) * mm});
            skPoint(sketch, "E610.MirrorP", {"position": v(-221.81, 35.67) * mm});
            skPoint(sketch, "E611.MirrorP", {"position": v(-147.41, -107.97) * mm});
            skPoint(sketch, "E612.MirrorP", {"position": v(-170.48, -92.45) * mm});
            skPoint(sketch, "E613.MirrorP", {"position": v(-190.47, -73) * mm});
            skPoint(sketch, "E614.MirrorP", {"position": v(89.07, 5.5) * mm});
            skPoint(sketch, "E615.MirrorP", {"position": v(91.33, 33.68) * mm});
            skPoint(sketch, "E616.MirrorP", {"position": v(-123.32, -118.78) * mm});
            skPoint(sketch, "E617.MirrorP", {"position": v(-96.73, -125.73) * mm});
            skPoint(sketch, "E618.MirrorP", {"position": v(54.66, -69.3) * mm});
            skPoint(sketch, "E619.MirrorP", {"position": v(35.21, -89.2) * mm});
            skPoint(sketch, "E620.MirrorP", {"position": v(70.53, -46.48) * mm});
            skPoint(sketch, "E621.MirrorP", {"position": v(81.84, -21.8) * mm});
            skPoint(sketch, "E622.MirrorP", {"position": v(-50.3, -126.83) * mm});
            skPoint(sketch, "E623.MirrorP", {"position": v(9.6, -107.2) * mm});
            skPoint(sketch, "E624.MirrorP", {"position": v(-17.7, -119.42) * mm});
            skPoint(sketch, "E625.MirrorP", {"position": v(-206.8, -50.72) * mm});
            skPoint(sketch, "E626.MirrorP", {"position": v(-219.36, -25.1) * mm});
            skPoint(sketch, "E627.MirrorP", {"position": v(-227.57, 3.3) * mm});
            skPoint(sketch, "E628.MirrorP", {"position": v(-230.29, 30.97) * mm});
            skPoint(sketch, "E629.MirrorP", {"position": v(-229.8, 20.49) * mm});
            skPoint(sketch, "E630.MirrorP", {"position": v(-214.7, -36.16) * mm});
            skPoint(sketch, "E631.MirrorP", {"position": v(-224.68, -9.15) * mm});
            skPoint(sketch, "E632.MirrorP", {"position": v(-200.96, -59.72) * mm});
            skPoint(sketch, "E633.MirrorP", {"position": v(-183.44, -80.7) * mm});
            skPoint(sketch, "E634.MirrorP", {"position": v(43.16, -82.1) * mm});
            skPoint(sketch, "E635.MirrorP", {"position": v(-220.52, -22.28) * mm});
            skPoint(sketch, "E636.MirrorP", {"position": v(-230.29, 34.02) * mm});
            skPoint(sketch, "E637.MirrorP", {"position": v(-208.41, -48.14) * mm});
            skPoint(sketch, "E638.MirrorP", {"position": v(-228.1, 6.3) * mm});
            skPoint(sketch, "E639.MirrorP", {"position": v(-6.22, -115.03) * mm});
            skPoint(sketch, "E640.MirrorP", {"position": v(20.53, -100.7) * mm});
            skPoint(sketch, "E641.MirrorP", {"position": v(-53.33, -127.2) * mm});
            skPoint(sketch, "E642.MirrorP", {"position": v(-36.32, -124.36) * mm});
            skPoint(sketch, "E643.MirrorP", {"position": v(90.42, 15.16) * mm});
            skPoint(sketch, "E644.MirrorP", {"position": v(75.3, -37.39) * mm});
            skPoint(sketch, "E645.MirrorP", {"position": v(85.15, -11.63) * mm});
            skPoint(sketch, "E646.MirrorP", {"position": v(61.4, -60.8) * mm});
            skPoint(sketch, "E647.MirrorP", {"position": v(32.94, -91.23) * mm});
            skPoint(sketch, "E648.MirrorP", {"position": v(-85.5, -127.35) * mm});
            skPoint(sketch, "E649.MirrorP", {"position": v(-138.66, -112.43) * mm});
            skPoint(sketch, "E650.MirrorP", {"position": v(-161.76, -98.97) * mm});
            skPoint(sketch, "E651.MirrorP", {"position": v(-112.7, -122.16) * mm});
            skPoint(sketch, "E652.MirrorP", {"position": v(52.78, -71.7) * mm});
            skPoint(sketch, "E653.MirrorP", {"position": v(6.93, -108.66) * mm});
            skPoint(sketch, "E654.MirrorP", {"position": v(-20.6, -120.42) * mm});
            skPoint(sketch, "E655.MirrorP", {"position": v(91.2, 30.63) * mm});
            skPoint(sketch, "E656.MirrorP", {"position": v(69, -49.12) * mm});
            skPoint(sketch, "E657.MirrorP", {"position": v(88.53, 2.5) * mm});
            skPoint(sketch, "E658.MirrorP", {"position": v(80.8, -24.66) * mm});
            skPoint(sketch, "E659.MirrorP", {"position": v(-150.05, -106.45) * mm});
            skPoint(sketch, "E660.MirrorP", {"position": v(-172.82, -90.5) * mm});
            skPoint(sketch, "E661.MirrorP", {"position": v(-136.57, -104.05) * mm});
            skPoint(sketch, "E662.MirrorP", {"position": v(69.6, -29.55) * mm});
            skPoint(sketch, "E663.MirrorP", {"position": v(-82.47, -127.75) * mm});
            skPoint(sketch, "E664.MirrorP", {"position": v(-158.25, -91.08) * mm});
            skPoint(sketch, "E665.MirrorP", {"position": v(-159.26, -100.72) * mm});
            skPoint(sketch, "E666.MirrorP", {"position": v(-135.9, -113.72) * mm});
            skPoint(sketch, "E667.MirrorP", {"position": v(66.91, -35.3) * mm});
            skPoint(sketch, "E668.MirrorP", {"position": v(78.17, -4.9) * mm});
            skPoint(sketch, "E669.MirrorP", {"position": v(-109.75, -122.95) * mm});
            skPoint(sketch, "E670.MirrorP", {"position": v(-11.2, -107.98) * mm});
            skPoint(sketch, "E671.MirrorP", {"position": v(-221.52, 22.96) * mm});
            skPoint(sketch, "E672.MirrorP", {"position": v(-207.99, -30.72) * mm});
            skPoint(sketch, "E673.MirrorP", {"position": v(76.53, -11.03) * mm});
            skPoint(sketch, "E674.MirrorP", {"position": v(81.83, 14.25) * mm});
            skPoint(sketch, "E675.MirrorP", {"position": v(82.38, 20.58) * mm});
            skPoint(sketch, "E676.MirrorP", {"position": v(-66.24, -119.6) * mm});
            skPoint(sketch, "E677.MirrorP", {"position": v(-5.4, -105.37) * mm});
            skPoint(sketch, "E678.MirrorP", {"position": v(14.2, -94.82) * mm});
            skPoint(sketch, "E679.MirrorP", {"position": v(19.34, -91.08) * mm});
            skPoint(sketch, "E680.MirrorP", {"position": v(-195.26, -53.23) * mm});
            skPoint(sketch, "E681.MirrorP", {"position": v(40.5, -72.78) * mm});
            skPoint(sketch, "E682.MirrorP", {"position": v(-174.15, -77.92) * mm});
            skPoint(sketch, "E683.MirrorP", {"position": v(-79.72, -119.57) * mm});
            skPoint(sketch, "E684.MirrorP", {"position": v(-153.05, -94.73) * mm});
            skPoint(sketch, "E685.MirrorP", {"position": v(-215.19, -11.12) * mm});
            skPoint(sketch, "E686.MirrorP", {"position": v(-181.26, -82.83) * mm});
            skPoint(sketch, "E687.MirrorP", {"position": v(-105.96, -115.19) * mm});
            skPoint(sketch, "E688.MirrorP", {"position": v(-130.82, -106.74) * mm});
            skPoint(sketch, "E689.MirrorP", {"position": v(-220.9, 16.64) * mm});
            skPoint(sketch, "E690.MirrorP", {"position": v(-205.01, -36.33) * mm});
            skPoint(sketch, "E691.MirrorP", {"position": v(-191.38, -58.26) * mm});
            skPoint(sketch, "E692.MirrorP", {"position": v(-112.1, -113.55) * mm});
            skPoint(sketch, "E693.MirrorP", {"position": v(-86.02, -118.73) * mm});
            skPoint(sketch, "E694.MirrorP", {"position": v(-217.07, -5.05) * mm});
            skPoint(sketch, "E695.MirrorP", {"position": v(-178.7, -73.48) * mm});
            skPoint(sketch, "E696.MirrorP", {"position": v(-33.33, -123.77) * mm});
            skPoint(sketch, "E697.MirrorP", {"position": v(76.58, -34.63) * mm});
            skPoint(sketch, "E698.MirrorP", {"position": v(-39.57, -116.36) * mm});
            skPoint(sketch, "E699.MirrorP", {"position": v(53.5, -57.29) * mm});
            skPoint(sketch, "E700.MirrorP", {"position": v(-223.77, -12.06) * mm});
            skPoint(sketch, "E701.MirrorP", {"position": v(23, -98.9) * mm});
            skPoint(sketch, "E702.MirrorP", {"position": v(63.15, -58.3) * mm});
            skPoint(sketch, "E703.MirrorP", {"position": v(-3.43, -113.78) * mm});
            skPoint(sketch, "E704.MirrorP", {"position": v(-99.73, -125.2) * mm});
            skPoint(sketch, "E705.MirrorP", {"position": v(57.15, -52.09) * mm});
            skPoint(sketch, "E706.MirrorP", {"position": v(36, -77.27) * mm});
            skPoint(sketch, "E707.MirrorP", {"position": v(90.69, 18.2) * mm});
            skPoint(sketch, "E708.MirrorP", {"position": v(45.32, -79.94) * mm});
            skPoint(sketch, "E709.MirrorP", {"position": v(-33.34, -115.13) * mm});
            skPoint(sketch, "E710.MirrorP", {"position": v(85.93, -8.69) * mm});
            skPoint(sketch, "E711.MirrorP", {"position": v(-192.5, -70.74) * mm});
            skPoint(sketch, "E712.MirrorP", {"position": v(-213.27, -38.85) * mm});
            skPoint(sketch, "E713.MirrorP", {"position": v(-229.5, 17.45) * mm});
            skPoint(sketch, "E714.MirrorP", {"position": v(-199.1, -62.14) * mm});
            skPoint(sketch, "E715.MirrorP", {"position": v(-126.18, -117.74) * mm});
            skLineSegment(sketch, "E716", {"start": v(214.96, 112.86) * mm, "end": v(219.46, 112.86) * mm});
            skLineSegment(sketch, "E717", {"start": v(220.2, 113.76) * mm, "end": v(218.85, 120.72) * mm});
            skLineSegment(sketch, "E718", {"start": v(218.1, 121.33) * mm, "end": v(216.31, 121.33) * mm});
            skLineSegment(sketch, "E719", {"start": v(215.56, 120.72) * mm, "end": v(214.2, 113.76) * mm});
            skPoint(sketch, "E720.visualSharp", {"position": v(215.68, 121.33) * mm});
            skArc(sketch, "E720.filletArc", {"start": v(216.31, 121.33) * mm, "mid": v(215.83, 121.16) * mm, "end": v(215.56, 120.72) * mm});
            skPoint(sketch, "E721.visualSharp", {"position": v(218.73, 121.33) * mm});
            skArc(sketch, "E721.filletArc", {"start": v(218.85, 120.72) * mm, "mid": v(218.59, 121.16) * mm, "end": v(218.1, 121.33) * mm});
            skPoint(sketch, "E722.visualSharp", {"position": v(214.03, 112.86) * mm});
            skArc(sketch, "E722.filletArc", {"start": v(214.2, 113.76) * mm, "mid": v(214.37, 113.13) * mm, "end": v(214.96, 112.86) * mm});
            skPoint(sketch, "E723.visualSharp", {"position": v(220.38, 112.86) * mm});
            skArc(sketch, "E723.filletArc", {"start": v(219.46, 112.86) * mm, "mid": v(220.05, 113.13) * mm, "end": v(220.2, 113.76) * mm});
            skLineSegment(sketch, "E724", {"start": v(294.13, 34.12) * mm, "end": v(301.09, 35.48) * mm});
            skPoint(sketch, "E725.visualSharp", {"position": v(301.7, 35.6) * mm});
            skArc(sketch, "E725.filletArc", {"start": v(301.09, 35.48) * mm, "mid": v(301.53, 35.74) * mm, "end": v(301.7, 36.23) * mm});
            skPoint(sketch, "E726.visualSharp", {"position": v(293.23, 33.95) * mm});
            skArc(sketch, "E726.filletArc", {"start": v(293.23, 34.87) * mm, "mid": v(293.5, 34.28) * mm, "end": v(294.13, 34.12) * mm});
            skLineSegment(sketch, "E727", {"start": v(141.24, 34.52) * mm, "end": v(141.24, 39.02) * mm});
            skLineSegment(sketch, "E728", {"start": v(140.33, 39.77) * mm, "end": v(133.38, 38.41) * mm});
            skLineSegment(sketch, "E729", {"start": v(132.76, 37.66) * mm, "end": v(132.76, 35.87) * mm});
            skLineSegment(sketch, "E730", {"start": v(133.38, 35.12) * mm, "end": v(140.33, 33.77) * mm});
            skPoint(sketch, "E731.visualSharp", {"position": v(132.76, 35.24) * mm});
            skArc(sketch, "E731.filletArc", {"start": v(132.76, 35.87) * mm, "mid": v(132.93, 35.39) * mm, "end": v(133.38, 35.12) * mm});
            skPoint(sketch, "E732.visualSharp", {"position": v(132.76, 38.3) * mm});
            skArc(sketch, "E732.filletArc", {"start": v(133.38, 38.41) * mm, "mid": v(132.93, 38.15) * mm, "end": v(132.76, 37.66) * mm});
            skPoint(sketch, "E733.visualSharp", {"position": v(141.24, 33.6) * mm});
            skArc(sketch, "E733.filletArc", {"start": v(140.33, 33.77) * mm, "mid": v(140.96, 33.93) * mm, "end": v(141.24, 34.52) * mm});
            skPoint(sketch, "E734.visualSharp", {"position": v(141.24, 39.94) * mm});
            skArc(sketch, "E734.filletArc", {"start": v(141.24, 39.02) * mm, "mid": v(140.96, 39.6) * mm, "end": v(140.33, 39.77) * mm});
            skLineSegment(sketch, "E735", {"start": v(228.3, 112.06) * mm, "end": v(232.74, 111.28) * mm});
            skLineSegment(sketch, "E736", {"start": v(233.63, 112.04) * mm, "end": v(233.5, 119.13) * mm});
            skLineSegment(sketch, "E737", {"start": v(232.87, 119.86) * mm, "end": v(231.1, 120.17) * mm});
            skLineSegment(sketch, "E738", {"start": v(230.27, 119.7) * mm, "end": v(227.72, 113.08) * mm});
            skPoint(sketch, "E739.visualSharp", {"position": v(230.5, 120.28) * mm});
            skArc(sketch, "E739.filletArc", {"start": v(231.1, 120.17) * mm, "mid": v(230.6, 120.09) * mm, "end": v(230.27, 119.7) * mm});
            skPoint(sketch, "E740.visualSharp", {"position": v(233.5, 119.75) * mm});
            skArc(sketch, "E740.filletArc", {"start": v(233.5, 119.13) * mm, "mid": v(233.32, 119.6) * mm, "end": v(232.87, 119.86) * mm});
            skPoint(sketch, "E741.visualSharp", {"position": v(227.4, 112.22) * mm});
            skArc(sketch, "E741.filletArc", {"start": v(227.72, 113.08) * mm, "mid": v(227.77, 112.44) * mm, "end": v(228.3, 112.06) * mm});
            skPoint(sketch, "E742.visualSharp", {"position": v(233.65, 111.12) * mm});
            skArc(sketch, "E742.filletArc", {"start": v(232.74, 111.28) * mm, "mid": v(233.36, 111.45) * mm, "end": v(233.63, 112.04) * mm});
            skLineSegment(sketch, "E743", {"start": v(241.03, 109.03) * mm, "end": v(245.26, 107.5) * mm});
            skLineSegment(sketch, "E744", {"start": v(246.27, 108.09) * mm, "end": v(247.38, 115.09) * mm});
            skLineSegment(sketch, "E745", {"start": v(246.89, 115.92) * mm, "end": v(245.2, 116.53) * mm});
            skLineSegment(sketch, "E746", {"start": v(244.29, 116.21) * mm, "end": v(240.64, 110.14) * mm});
            skPoint(sketch, "E747.visualSharp", {"position": v(244.61, 116.75) * mm});
            skArc(sketch, "E747.filletArc", {"start": v(245.2, 116.53) * mm, "mid": v(244.69, 116.54) * mm, "end": v(244.29, 116.21) * mm});
            skPoint(sketch, "E748.visualSharp", {"position": v(247.48, 115.7) * mm});
            skArc(sketch, "E748.filletArc", {"start": v(247.38, 115.09) * mm, "mid": v(247.28, 115.6) * mm, "end": v(246.89, 115.92) * mm});
            skPoint(sketch, "E749.visualSharp", {"position": v(240.16, 109.35) * mm});
            skArc(sketch, "E749.filletArc", {"start": v(240.64, 110.14) * mm, "mid": v(240.57, 109.5) * mm, "end": v(241.03, 109.03) * mm});
            skPoint(sketch, "E750.visualSharp", {"position": v(246.13, 107.18) * mm});
            skArc(sketch, "E750.filletArc", {"start": v(245.26, 107.5) * mm, "mid": v(245.9, 107.55) * mm, "end": v(246.27, 108.09) * mm});
            skLineSegment(sketch, "E751", {"start": v(252.15, 104.33) * mm, "end": v(256.05, 102.08) * mm});
            skLineSegment(sketch, "E752", {"start": v(257.15, 102.5) * mm, "end": v(259.45, 109.2) * mm});
            skLineSegment(sketch, "E753", {"start": v(259.11, 110.1) * mm, "end": v(257.56, 111) * mm});
            skLineSegment(sketch, "E754", {"start": v(256.6, 110.83) * mm, "end": v(251.96, 105.5) * mm});
            skPoint(sketch, "E755.visualSharp", {"position": v(257.02, 111.3) * mm});
            skArc(sketch, "E755.filletArc", {"start": v(257.56, 111) * mm, "mid": v(257.06, 111.09) * mm, "end": v(256.6, 110.83) * mm});
            skPoint(sketch, "E756.visualSharp", {"position": v(259.66, 109.78) * mm});
            skArc(sketch, "E756.filletArc", {"start": v(259.45, 109.2) * mm, "mid": v(259.45, 109.7) * mm, "end": v(259.11, 110.1) * mm});
            skPoint(sketch, "E757.visualSharp", {"position": v(251.35, 104.8) * mm});
            skArc(sketch, "E757.filletArc", {"start": v(251.96, 105.5) * mm, "mid": v(251.78, 104.86) * mm, "end": v(252.15, 104.33) * mm});
            skPoint(sketch, "E758.visualSharp", {"position": v(256.85, 101.62) * mm});
            skArc(sketch, "E758.filletArc", {"start": v(256.05, 102.08) * mm, "mid": v(256.7, 102.03) * mm, "end": v(257.15, 102.5) * mm});
            skLineSegment(sketch, "E759", {"start": v(261.96, 98.29) * mm, "end": v(265.54, 95.56) * mm});
            skLineSegment(sketch, "E760", {"start": v(266.69, 95.83) * mm, "end": v(269.82, 102.18) * mm});
            skLineSegment(sketch, "E761", {"start": v(269.6, 103.12) * mm, "end": v(268.18, 104.2) * mm});
            skLineSegment(sketch, "E762", {"start": v(267.2, 104.17) * mm, "end": v(261.92, 99.46) * mm});
            skPoint(sketch, "E763.visualSharp", {"position": v(267.68, 104.59) * mm});
            skArc(sketch, "E763.filletArc", {"start": v(268.18, 104.2) * mm, "mid": v(267.69, 104.36) * mm, "end": v(267.2, 104.17) * mm});
            skPoint(sketch, "E764.visualSharp", {"position": v(270.1, 102.74) * mm});
            skArc(sketch, "E764.filletArc", {"start": v(269.82, 102.18) * mm, "mid": v(269.88, 102.7) * mm, "end": v(269.6, 103.12) * mm});
            skPoint(sketch, "E765.visualSharp", {"position": v(261.23, 98.85) * mm});
            skArc(sketch, "E765.filletArc", {"start": v(261.92, 99.46) * mm, "mid": v(261.66, 98.87) * mm, "end": v(261.96, 98.29) * mm});
            skPoint(sketch, "E766.visualSharp", {"position": v(266.28, 95) * mm});
            skArc(sketch, "E766.filletArc", {"start": v(265.54, 95.56) * mm, "mid": v(266.18, 95.42) * mm, "end": v(266.69, 95.83) * mm});
            skLineSegment(sketch, "E767", {"start": v(270.45, 91.06) * mm, "end": v(273.5, 87.75) * mm});
            skLineSegment(sketch, "E768", {"start": v(274.68, 87.82) * mm, "end": v(278.87, 93.52) * mm});
            skLineSegment(sketch, "E769", {"start": v(278.82, 94.5) * mm, "end": v(277.6, 95.8) * mm});
            skLineSegment(sketch, "E770", {"start": v(276.65, 95.94) * mm, "end": v(270.61, 92.23) * mm});
            skPoint(sketch, "E771.visualSharp", {"position": v(277.18, 96.27) * mm});
            skArc(sketch, "E771.filletArc", {"start": v(277.6, 95.8) * mm, "mid": v(277.15, 96.05) * mm, "end": v(276.65, 95.94) * mm});
            skPoint(sketch, "E772.visualSharp", {"position": v(279.24, 94.03) * mm});
            skArc(sketch, "E772.filletArc", {"start": v(278.87, 93.52) * mm, "mid": v(279.02, 94.02) * mm, "end": v(278.82, 94.5) * mm});
            skPoint(sketch, "E773.visualSharp", {"position": v(269.83, 91.74) * mm});
            skArc(sketch, "E773.filletArc", {"start": v(270.61, 92.23) * mm, "mid": v(270.26, 91.68) * mm, "end": v(270.45, 91.06) * mm});
            skPoint(sketch, "E774.visualSharp", {"position": v(274.13, 87.07) * mm});
            skArc(sketch, "E774.filletArc", {"start": v(273.5, 87.75) * mm, "mid": v(274.1, 87.5) * mm, "end": v(274.68, 87.82) * mm});
            skLineSegment(sketch, "E775", {"start": v(278.84, 81.22) * mm, "end": v(281.41, 77.53) * mm});
            skLineSegment(sketch, "E776", {"start": v(282.58, 77.43) * mm, "end": v(287.52, 82.5) * mm});
            skLineSegment(sketch, "E777", {"start": v(287.6, 83.47) * mm, "end": v(286.58, 84.94) * mm});
            skLineSegment(sketch, "E778", {"start": v(285.65, 85.2) * mm, "end": v(279.16, 82.36) * mm});
            skPoint(sketch, "E779.visualSharp", {"position": v(286.22, 85.46) * mm});
            skArc(sketch, "E779.filletArc", {"start": v(286.58, 84.94) * mm, "mid": v(286.16, 85.24) * mm, "end": v(285.65, 85.2) * mm});
            skPoint(sketch, "E780.visualSharp", {"position": v(287.96, 82.96) * mm});
            skArc(sketch, "E780.filletArc", {"start": v(287.52, 82.5) * mm, "mid": v(287.74, 82.98) * mm, "end": v(287.6, 83.47) * mm});
            skPoint(sketch, "E781.visualSharp", {"position": v(278.32, 81.98) * mm});
            skArc(sketch, "E781.filletArc", {"start": v(279.16, 82.36) * mm, "mid": v(278.74, 81.87) * mm, "end": v(278.84, 81.22) * mm});
            skPoint(sketch, "E782.visualSharp", {"position": v(281.94, 76.77) * mm});
            skArc(sketch, "E782.filletArc", {"start": v(281.41, 77.53) * mm, "mid": v(281.97, 77.2) * mm, "end": v(282.58, 77.43) * mm});
            skLineSegment(sketch, "E783", {"start": v(285.87, 69.17) * mm, "end": v(287.77, 65.1) * mm});
            skLineSegment(sketch, "E784", {"start": v(288.91, 64.8) * mm, "end": v(294.64, 68.96) * mm});
            skLineSegment(sketch, "E785", {"start": v(294.88, 69.9) * mm, "end": v(294.12, 71.52) * mm});
            skLineSegment(sketch, "E786", {"start": v(293.25, 71.94) * mm, "end": v(286.38, 70.23) * mm});
            skPoint(sketch, "E787.visualSharp", {"position": v(293.86, 72.1) * mm});
            skArc(sketch, "E787.filletArc", {"start": v(294.12, 71.52) * mm, "mid": v(293.76, 71.9) * mm, "end": v(293.25, 71.94) * mm});
            skPoint(sketch, "E788.visualSharp", {"position": v(295.15, 69.33) * mm});
            skArc(sketch, "E788.filletArc", {"start": v(294.64, 68.96) * mm, "mid": v(294.93, 69.39) * mm, "end": v(294.88, 69.9) * mm});
            skPoint(sketch, "E789.visualSharp", {"position": v(285.48, 70) * mm});
            skArc(sketch, "E789.filletArc", {"start": v(286.38, 70.23) * mm, "mid": v(285.87, 69.82) * mm, "end": v(285.87, 69.17) * mm});
            skPoint(sketch, "E790.visualSharp", {"position": v(288.16, 64.25) * mm});
            skArc(sketch, "E790.filletArc", {"start": v(287.77, 65.1) * mm, "mid": v(288.27, 64.67) * mm, "end": v(288.91, 64.8) * mm});
            skLineSegment(sketch, "E791", {"start": v(291.16, 54.59) * mm, "end": v(292.14, 50.2) * mm});
            skLineSegment(sketch, "E792", {"start": v(293.19, 49.66) * mm, "end": v(299.68, 52.5) * mm});
            skLineSegment(sketch, "E793", {"start": v(300.12, 53.36) * mm, "end": v(299.73, 55.1) * mm});
            skLineSegment(sketch, "E794", {"start": v(298.97, 55.7) * mm, "end": v(291.89, 55.51) * mm});
            skPoint(sketch, "E795.visualSharp", {"position": v(299.6, 55.72) * mm});
            skArc(sketch, "E795.filletArc", {"start": v(299.73, 55.1) * mm, "mid": v(299.46, 55.54) * mm, "end": v(298.97, 55.7) * mm});
            skPoint(sketch, "E796.visualSharp", {"position": v(300.26, 52.74) * mm});
            skArc(sketch, "E796.filletArc", {"start": v(299.68, 52.5) * mm, "mid": v(300.06, 52.85) * mm, "end": v(300.12, 53.36) * mm});
            skPoint(sketch, "E797.visualSharp", {"position": v(290.96, 55.5) * mm});
            skArc(sketch, "E797.filletArc", {"start": v(291.89, 55.51) * mm, "mid": v(291.3, 55.22) * mm, "end": v(291.16, 54.59) * mm});
            skPoint(sketch, "E798.visualSharp", {"position": v(292.34, 49.3) * mm});
            skArc(sketch, "E798.filletArc", {"start": v(292.14, 50.2) * mm, "mid": v(292.54, 49.68) * mm, "end": v(293.19, 49.66) * mm});
            skArc(sketch, "E799.MirrorCS", {"start": v(139.72, 69.21) * mm, "mid": v(139.43, 69.64) * mm, "end": v(139.48, 70.15) * mm});
            skLineSegment(sketch, "E800.MirrorCS", {"start": v(139.48, 70.15) * mm, "end": v(140.24, 71.77) * mm});
            skArc(sketch, "E801.MirrorCS", {"start": v(163.8, 92.23) * mm, "mid": v(164.16, 91.68) * mm, "end": v(163.96, 91.06) * mm});
            skLineSegment(sketch, "E802.MirrorCS", {"start": v(172.45, 98.29) * mm, "end": v(168.87, 95.56) * mm});
            skLineSegment(sketch, "E803.MirrorCS", {"start": v(155.5, 81.25) * mm, "end": v(152.91, 77.57) * mm});
            skLineSegment(sketch, "E804.MirrorCS", {"start": v(216.31, 121.33) * mm, "end": v(218.1, 121.33) * mm});
            skLineSegment(sketch, "E805.MirrorCS", {"start": v(164.81, 103.12) * mm, "end": v(166.24, 104.2) * mm});
            skLineSegment(sketch, "E806.MirrorCS", {"start": v(187.53, 115.92) * mm, "end": v(189.21, 116.53) * mm});
            skLineSegment(sketch, "E807.MirrorCS", {"start": v(134.3, 53.36) * mm, "end": v(134.68, 55.1) * mm});
            skLineSegment(sketch, "E808.MirrorCS", {"start": v(146.75, 83.54) * mm, "end": v(147.77, 85) * mm});
            skArc(sketch, "E809.MirrorCS", {"start": v(218.1, 121.33) * mm, "mid": v(218.59, 121.16) * mm, "end": v(218.85, 120.72) * mm});
            skArc(sketch, "E810.MirrorCS", {"start": v(166.24, 104.2) * mm, "mid": v(166.73, 104.36) * mm, "end": v(167.2, 104.17) * mm});
            skArc(sketch, "E811.MirrorCS", {"start": v(189.21, 116.53) * mm, "mid": v(189.73, 116.54) * mm, "end": v(190.13, 116.21) * mm});
            skArc(sketch, "E812.MirrorCS", {"start": v(215.56, 120.72) * mm, "mid": v(215.83, 121.16) * mm, "end": v(216.31, 121.33) * mm});
            skArc(sketch, "E813.MirrorCS", {"start": v(134.68, 55.1) * mm, "mid": v(134.96, 55.54) * mm, "end": v(135.45, 55.7) * mm});
            skArc(sketch, "E814.MirrorCS", {"start": v(147.77, 85) * mm, "mid": v(148.2, 85.3) * mm, "end": v(148.7, 85.27) * mm});
            skArc(sketch, "E815.MirrorCS", {"start": v(220.2, 113.76) * mm, "mid": v(220.05, 113.13) * mm, "end": v(219.46, 112.86) * mm});
            skArc(sketch, "E816.MirrorCS", {"start": v(164.6, 102.18) * mm, "mid": v(164.53, 102.7) * mm, "end": v(164.81, 103.12) * mm});
            skArc(sketch, "E817.MirrorCS", {"start": v(187.04, 115.09) * mm, "mid": v(187.13, 115.6) * mm, "end": v(187.53, 115.92) * mm});
            skArc(sketch, "E818.MirrorCS", {"start": v(134.73, 52.5) * mm, "mid": v(134.36, 52.85) * mm, "end": v(134.3, 53.36) * mm});
            skArc(sketch, "E819.MirrorCS", {"start": v(146.82, 82.57) * mm, "mid": v(146.61, 83.04) * mm, "end": v(146.75, 83.54) * mm});
            skArc(sketch, "E820.MirrorCS", {"start": v(172.5, 99.46) * mm, "mid": v(172.75, 98.87) * mm, "end": v(172.45, 98.29) * mm});
            skArc(sketch, "E821.MirrorCS", {"start": v(193.78, 110.14) * mm, "mid": v(193.84, 109.5) * mm, "end": v(193.38, 109.03) * mm});
            skArc(sketch, "E822.MirrorCS", {"start": v(214.96, 112.86) * mm, "mid": v(214.37, 113.13) * mm, "end": v(214.2, 113.76) * mm});
            skArc(sketch, "E823.MirrorCS", {"start": v(142.53, 55.51) * mm, "mid": v(143.1, 55.22) * mm, "end": v(143.25, 54.59) * mm});
            skArc(sketch, "E824.MirrorCS", {"start": v(155.18, 82.39) * mm, "mid": v(155.6, 81.9) * mm, "end": v(155.5, 81.25) * mm});
            skArc(sketch, "E825.MirrorCS", {"start": v(168.87, 95.56) * mm, "mid": v(168.24, 95.42) * mm, "end": v(167.73, 95.83) * mm});
            skArc(sketch, "E826.MirrorCS", {"start": v(189.15, 107.5) * mm, "mid": v(188.5, 107.55) * mm, "end": v(188.14, 108.09) * mm});
            skArc(sketch, "E827.MirrorCS", {"start": v(152.91, 77.57) * mm, "mid": v(152.35, 77.24) * mm, "end": v(151.74, 77.47) * mm});
            skArc(sketch, "E828.MirrorCS", {"start": v(142.27, 50.2) * mm, "mid": v(141.88, 49.68) * mm, "end": v(141.23, 49.66) * mm});
            skLineSegment(sketch, "E829.MirrorCS", {"start": v(163.96, 91.06) * mm, "end": v(160.91, 87.75) * mm});
            skArc(sketch, "E830.MirrorCS", {"start": v(178.37, 102.08) * mm, "mid": v(177.72, 102.03) * mm, "end": v(177.26, 102.5) * mm});
            skArc(sketch, "E831.MirrorCS", {"start": v(160.91, 87.75) * mm, "mid": v(160.3, 87.5) * mm, "end": v(159.74, 87.82) * mm});
            skArc(sketch, "E832.MirrorCS", {"start": v(146.59, 65.34) * mm, "mid": v(146.09, 64.92) * mm, "end": v(145.45, 65.04) * mm});
            skArc(sketch, "E833.MirrorCS", {"start": v(201.68, 111.28) * mm, "mid": v(201.05, 111.45) * mm, "end": v(200.79, 112.04) * mm});
            skArc(sketch, "E834.MirrorCS", {"start": v(200.91, 119.13) * mm, "mid": v(201.1, 119.6) * mm, "end": v(201.54, 119.86) * mm});
            skArc(sketch, "E835.MirrorCS", {"start": v(155.54, 93.52) * mm, "mid": v(155.4, 94.02) * mm, "end": v(155.6, 94.5) * mm});
            skArc(sketch, "E836.MirrorCS", {"start": v(174.96, 109.2) * mm, "mid": v(174.97, 109.7) * mm, "end": v(175.3, 110.1) * mm});
            skLineSegment(sketch, "E837.MirrorCS", {"start": v(201.54, 119.86) * mm, "end": v(203.3, 120.17) * mm});
            skLineSegment(sketch, "E838.MirrorCS", {"start": v(175.3, 110.1) * mm, "end": v(176.85, 111) * mm});
            skLineSegment(sketch, "E839.MirrorCS", {"start": v(155.6, 94.5) * mm, "end": v(156.8, 95.8) * mm});
            skArc(sketch, "E840.MirrorCS", {"start": v(176.85, 111) * mm, "mid": v(177.36, 111.09) * mm, "end": v(177.8, 110.83) * mm});
            skArc(sketch, "E841.MirrorCS", {"start": v(140.24, 71.77) * mm, "mid": v(140.6, 72.14) * mm, "end": v(141.1, 72.2) * mm});
            skArc(sketch, "E842.MirrorCS", {"start": v(203.3, 120.17) * mm, "mid": v(203.81, 120.09) * mm, "end": v(204.15, 119.7) * mm});
            skArc(sketch, "E843.MirrorCS", {"start": v(156.8, 95.8) * mm, "mid": v(157.27, 96.05) * mm, "end": v(157.77, 95.94) * mm});
            skArc(sketch, "E844.MirrorCS", {"start": v(147.98, 70.48) * mm, "mid": v(148.49, 70.07) * mm, "end": v(148.5, 69.42) * mm});
            skArc(sketch, "E845.MirrorCS", {"start": v(182.46, 105.5) * mm, "mid": v(182.63, 104.86) * mm, "end": v(182.26, 104.33) * mm});
            skArc(sketch, "E846.MirrorCS", {"start": v(206.7, 113.08) * mm, "mid": v(206.64, 112.44) * mm, "end": v(206.11, 112.06) * mm});
            skLineSegment(sketch, "E847.MirrorCS", {"start": v(193.38, 109.03) * mm, "end": v(189.15, 107.5) * mm});
            skLineSegment(sketch, "E848.MirrorCS", {"start": v(143.25, 54.59) * mm, "end": v(142.27, 50.2) * mm});
            skLineSegment(sketch, "E849.MirrorCS", {"start": v(182.26, 104.33) * mm, "end": v(178.37, 102.08) * mm});
            skLineSegment(sketch, "E850.MirrorCS", {"start": v(148.5, 69.42) * mm, "end": v(146.59, 65.34) * mm});
            skLineSegment(sketch, "E851.MirrorCS", {"start": v(219.46, 112.86) * mm, "end": v(214.96, 112.86) * mm});
            skPoint(sketch, "E852.MirrorP", {"position": v(148.13, 85.52) * mm});
            skPoint(sketch, "E853.MirrorP", {"position": v(134.82, 55.72) * mm});
            skPoint(sketch, "E854.MirrorP", {"position": v(160.29, 87.07) * mm});
            skPoint(sketch, "E855.MirrorP", {"position": v(146.2, 64.5) * mm});
            skPoint(sketch, "E856.MirrorP", {"position": v(194.25, 109.35) * mm});
            skLineSegment(sketch, "E857.MirrorCS", {"start": v(214.2, 113.76) * mm, "end": v(215.56, 120.72) * mm});
            skPoint(sketch, "E858.MirrorP", {"position": v(143.45, 55.5) * mm});
            skPoint(sketch, "E859.MirrorP", {"position": v(200.77, 111.12) * mm});
            skLineSegment(sketch, "E860.MirrorCS", {"start": v(167.73, 95.83) * mm, "end": v(164.6, 102.18) * mm});
            skLineSegment(sketch, "E861.MirrorCS", {"start": v(188.14, 108.09) * mm, "end": v(187.04, 115.09) * mm});
            skLineSegment(sketch, "E862.MirrorCS", {"start": v(141.23, 49.66) * mm, "end": v(134.73, 52.5) * mm});
            skLineSegment(sketch, "E863.MirrorCS", {"start": v(151.74, 77.47) * mm, "end": v(146.82, 82.57) * mm});
            skPoint(sketch, "E864.MirrorP", {"position": v(173.19, 98.85) * mm});
            skPoint(sketch, "E865.MirrorP", {"position": v(156.03, 82.01) * mm});
            skLineSegment(sketch, "E866.MirrorCS", {"start": v(218.85, 120.72) * mm, "end": v(220.2, 113.76) * mm});
            skPoint(sketch, "E867.MirrorP", {"position": v(186.94, 115.7) * mm});
            skPoint(sketch, "E868.MirrorP", {"position": v(134.16, 52.74) * mm});
            skLineSegment(sketch, "E869.MirrorCS", {"start": v(167.2, 104.17) * mm, "end": v(172.5, 99.46) * mm});
            skLineSegment(sketch, "E870.MirrorCS", {"start": v(190.13, 116.21) * mm, "end": v(193.78, 110.14) * mm});
            skLineSegment(sketch, "E871.MirrorCS", {"start": v(135.45, 55.7) * mm, "end": v(142.53, 55.51) * mm});
            skLineSegment(sketch, "E872.MirrorCS", {"start": v(148.7, 85.27) * mm, "end": v(155.18, 82.39) * mm});
            skPoint(sketch, "E873.MirrorP", {"position": v(164.31, 102.74) * mm});
            skPoint(sketch, "E874.MirrorP", {"position": v(146.39, 83.02) * mm});
            skPoint(sketch, "E875.MirrorP", {"position": v(189.8, 116.75) * mm});
            skPoint(sketch, "E876.MirrorP", {"position": v(177.57, 101.62) * mm});
            skPoint(sketch, "E877.MirrorP", {"position": v(203.92, 120.28) * mm});
            skLineSegment(sketch, "E878.MirrorCS", {"start": v(206.11, 112.06) * mm, "end": v(201.68, 111.28) * mm});
            skLineSegment(sketch, "E879.MirrorCS", {"start": v(159.74, 87.82) * mm, "end": v(155.54, 93.52) * mm});
            skLineSegment(sketch, "E880.MirrorCS", {"start": v(177.26, 102.5) * mm, "end": v(174.96, 109.2) * mm});
            skLineSegment(sketch, "E881.MirrorCS", {"start": v(200.79, 112.04) * mm, "end": v(200.91, 119.13) * mm});
            skLineSegment(sketch, "E882.MirrorCS", {"start": v(145.45, 65.04) * mm, "end": v(139.72, 69.21) * mm});
            skPoint(sketch, "E883.MirrorP", {"position": v(174.76, 109.78) * mm});
            skPoint(sketch, "E884.MirrorP", {"position": v(200.92, 119.75) * mm});
            skPoint(sketch, "E885.MirrorP", {"position": v(164.59, 91.74) * mm});
            skPoint(sketch, "E886.MirrorP", {"position": v(183.06, 104.8) * mm});
            skPoint(sketch, "E887.MirrorP", {"position": v(148.88, 70.26) * mm});
            skPoint(sketch, "E888.MirrorP", {"position": v(152.38, 76.8) * mm});
            skPoint(sketch, "E889.MirrorP", {"position": v(139.21, 69.58) * mm});
            skPoint(sketch, "E890.MirrorP", {"position": v(168.14, 95) * mm});
            skPoint(sketch, "E891.MirrorP", {"position": v(207.02, 112.22) * mm});
            skPoint(sketch, "E892.MirrorP", {"position": v(142.07, 49.3) * mm});
            skPoint(sketch, "E893.MirrorP", {"position": v(188.29, 107.18) * mm});
            skPoint(sketch, "E894.MirrorP", {"position": v(157.24, 96.27) * mm});
            skPoint(sketch, "E895.MirrorP", {"position": v(177.4, 111.3) * mm});
            skPoint(sketch, "E896.MirrorP", {"position": v(155.17, 94.03) * mm});
            skPoint(sketch, "E897.MirrorP", {"position": v(140.5, 72.34) * mm});
            skLineSegment(sketch, "E898.MirrorCS", {"start": v(204.15, 119.7) * mm, "end": v(206.7, 113.08) * mm});
            skLineSegment(sketch, "E899.MirrorCS", {"start": v(177.8, 110.83) * mm, "end": v(182.46, 105.5) * mm});
            skPoint(sketch, "E900.MirrorP", {"position": v(166.74, 104.59) * mm});
            skLineSegment(sketch, "E901.MirrorCS", {"start": v(157.77, 95.94) * mm, "end": v(163.8, 92.23) * mm});
            skLineSegment(sketch, "E902.MirrorCS", {"start": v(141.1, 72.2) * mm, "end": v(147.98, 70.48) * mm});
            skLineSegment(sketch, "E903.MirrorCS", {"start": v(218.1, -47.8) * mm, "end": v(216.31, -47.8) * mm});
            skArc(sketch, "E904.MirrorCS", {"start": v(218.1, -47.8) * mm, "mid": v(218.59, -47.62) * mm, "end": v(218.85, -47.18) * mm});
            skArc(sketch, "E905.MirrorCS", {"start": v(216.31, -47.8) * mm, "mid": v(215.83, -47.62) * mm, "end": v(215.56, -47.18) * mm});
            skArc(sketch, "E906.MirrorCS", {"start": v(214.2, -40.23) * mm, "mid": v(214.37, -39.6) * mm, "end": v(214.96, -39.32) * mm});
            skArc(sketch, "E907.MirrorCS", {"start": v(219.46, -39.32) * mm, "mid": v(220.05, -39.6) * mm, "end": v(220.2, -40.23) * mm});
            skArc(sketch, "E908.MirrorCS", {"start": v(218.85, -47.18) * mm, "mid": v(218.59, -47.62) * mm, "end": v(218.1, -47.8) * mm});
            skArc(sketch, "E909.MirrorCS", {"start": v(215.56, -47.18) * mm, "mid": v(215.83, -47.62) * mm, "end": v(216.31, -47.8) * mm});
            skArc(sketch, "E910.MirrorCS", {"start": v(220.2, -40.23) * mm, "mid": v(220.05, -39.6) * mm, "end": v(219.46, -39.32) * mm});
            skArc(sketch, "E911.MirrorCS", {"start": v(214.96, -39.32) * mm, "mid": v(214.37, -39.6) * mm, "end": v(214.2, -40.23) * mm});
            skLineSegment(sketch, "E912.MirrorCS", {"start": v(216.31, -47.8) * mm, "end": v(218.1, -47.8) * mm});
            skLineSegment(sketch, "E913.MirrorCS", {"start": v(219.46, -39.32) * mm, "end": v(214.96, -39.32) * mm});
            skArc(sketch, "E914.MirrorCS", {"start": v(203.3, -46.64) * mm, "mid": v(203.81, -46.55) * mm, "end": v(204.15, -46.16) * mm});
            skArc(sketch, "E915.MirrorCS", {"start": v(152.91, -4.03) * mm, "mid": v(152.35, -3.7) * mm, "end": v(151.74, -3.94) * mm});
            skArc(sketch, "E916.MirrorCS", {"start": v(281.5, -4.03) * mm, "mid": v(282.07, -3.7) * mm, "end": v(282.67, -3.94) * mm});
            skLineSegment(sketch, "E917.MirrorCS", {"start": v(134.3, 20.18) * mm, "end": v(134.68, 18.43) * mm});
            skLineSegment(sketch, "E918.MirrorCS", {"start": v(214.96, -39.32) * mm, "end": v(219.46, -39.32) * mm});
            skLineSegment(sketch, "E919.MirrorCS", {"start": v(201.54, -46.33) * mm, "end": v(203.3, -46.64) * mm});
            skArc(sketch, "E920.MirrorCS", {"start": v(134.73, 21.04) * mm, "mid": v(134.36, 20.7) * mm, "end": v(134.3, 20.18) * mm});
            skLineSegment(sketch, "E921.MirrorCS", {"start": v(261.96, -24.75) * mm, "end": v(265.54, -22.02) * mm});
            skLineSegment(sketch, "E922.MirrorCS", {"start": v(132.76, 35.87) * mm, "end": v(132.76, 37.66) * mm});
            skArc(sketch, "E923.MirrorCS", {"start": v(155.18, -8.85) * mm, "mid": v(155.6, -8.36) * mm, "end": v(155.5, -7.72) * mm});
            skLineSegment(sketch, "E924.MirrorCS", {"start": v(146.75, -10) * mm, "end": v(147.77, -11.47) * mm});
            skArc(sketch, "E925.MirrorCS", {"start": v(176.85, -37.46) * mm, "mid": v(177.36, -37.55) * mm, "end": v(177.8, -37.3) * mm});
            skLineSegment(sketch, "E926.MirrorCS", {"start": v(269.6, -29.59) * mm, "end": v(268.18, -30.67) * mm});
            skLineSegment(sketch, "E927.MirrorCS", {"start": v(246.89, -42.39) * mm, "end": v(245.2, -43) * mm});
            skArc(sketch, "E928.MirrorCS", {"start": v(168.87, -22.02) * mm, "mid": v(168.24, -21.89) * mm, "end": v(167.73, -22.3) * mm});
            skLineSegment(sketch, "E929.MirrorCS", {"start": v(300.12, 20.18) * mm, "end": v(299.73, 18.43) * mm});
            skLineSegment(sketch, "E930.MirrorCS", {"start": v(287.67, -10) * mm, "end": v(286.64, -11.47) * mm});
            skArc(sketch, "E931.MirrorCS", {"start": v(140.24, 1.76) * mm, "mid": v(140.6, 1.4) * mm, "end": v(141.1, 1.35) * mm});
            skArc(sketch, "E932.MirrorCS", {"start": v(132.76, 37.66) * mm, "mid": v(132.93, 38.15) * mm, "end": v(133.38, 38.41) * mm});
            skArc(sketch, "E933.MirrorCS", {"start": v(189.15, -33.96) * mm, "mid": v(188.5, -34.02) * mm, "end": v(188.14, -34.55) * mm});
            skArc(sketch, "E934.MirrorCS", {"start": v(166.24, -30.67) * mm, "mid": v(166.73, -30.83) * mm, "end": v(167.2, -30.64) * mm});
            skArc(sketch, "E935.MirrorCS", {"start": v(245.2, -43) * mm, "mid": v(244.69, -43) * mm, "end": v(244.29, -42.67) * mm});
            skArc(sketch, "E936.MirrorCS", {"start": v(268.18, -30.67) * mm, "mid": v(267.69, -30.83) * mm, "end": v(267.2, -30.64) * mm});
            skArc(sketch, "E937.MirrorCS", {"start": v(133.38, 35.12) * mm, "mid": v(132.93, 35.39) * mm, "end": v(132.76, 35.87) * mm});
            skArc(sketch, "E938.MirrorCS", {"start": v(189.21, -43) * mm, "mid": v(189.73, -43) * mm, "end": v(190.13, -42.67) * mm});
            skArc(sketch, "E939.MirrorCS", {"start": v(299.73, 18.43) * mm, "mid": v(299.46, 18) * mm, "end": v(298.97, 17.83) * mm});
            skArc(sketch, "E940.MirrorCS", {"start": v(286.64, -11.47) * mm, "mid": v(286.22, -11.77) * mm, "end": v(285.7, -11.73) * mm});
            skArc(sketch, "E941.MirrorCS", {"start": v(156.8, -22.27) * mm, "mid": v(157.27, -22.51) * mm, "end": v(157.77, -22.4) * mm});
            skArc(sketch, "E942.MirrorCS", {"start": v(247.38, -41.55) * mm, "mid": v(247.28, -42.06) * mm, "end": v(246.89, -42.39) * mm});
            skArc(sketch, "E943.MirrorCS", {"start": v(269.82, -28.64) * mm, "mid": v(269.88, -29.15) * mm, "end": v(269.6, -29.59) * mm});
            skArc(sketch, "E944.MirrorCS", {"start": v(140.33, 39.77) * mm, "mid": v(140.96, 39.6) * mm, "end": v(141.24, 39.02) * mm});
            skArc(sketch, "E945.MirrorCS", {"start": v(142.27, 23.34) * mm, "mid": v(141.88, 23.86) * mm, "end": v(141.23, 23.87) * mm});
            skArc(sketch, "E946.MirrorCS", {"start": v(287.6, -9.04) * mm, "mid": v(287.8, -9.5) * mm, "end": v(287.67, -10) * mm});
            skArc(sketch, "E947.MirrorCS", {"start": v(299.68, 21.04) * mm, "mid": v(300.06, 20.7) * mm, "end": v(300.12, 20.18) * mm});
            skArc(sketch, "E948.MirrorCS", {"start": v(147.98, 3.06) * mm, "mid": v(148.49, 3.47) * mm, "end": v(148.5, 4.12) * mm});
            skArc(sketch, "E949.MirrorCS", {"start": v(141.24, 34.52) * mm, "mid": v(140.96, 33.93) * mm, "end": v(140.33, 33.77) * mm});
            skArc(sketch, "E950.MirrorCS", {"start": v(240.64, -36.6) * mm, "mid": v(240.57, -35.96) * mm, "end": v(241.03, -35.5) * mm});
            skArc(sketch, "E951.MirrorCS", {"start": v(261.92, -25.93) * mm, "mid": v(261.66, -25.33) * mm, "end": v(261.96, -24.75) * mm});
            skLineSegment(sketch, "E952.MirrorCS", {"start": v(163.96, -17.53) * mm, "end": v(160.91, -14.22) * mm});
            skArc(sketch, "E953.MirrorCS", {"start": v(291.89, 18.02) * mm, "mid": v(291.3, 18.31) * mm, "end": v(291.16, 18.95) * mm});
            skArc(sketch, "E954.MirrorCS", {"start": v(134.68, 18.43) * mm, "mid": v(134.96, 18) * mm, "end": v(135.45, 17.83) * mm});
            skArc(sketch, "E955.MirrorCS", {"start": v(279.23, -8.85) * mm, "mid": v(278.8, -8.36) * mm, "end": v(278.92, -7.72) * mm});
            skArc(sketch, "E956.MirrorCS", {"start": v(182.46, -31.95) * mm, "mid": v(182.63, -31.33) * mm, "end": v(182.26, -30.8) * mm});
            skArc(sketch, "E957.MirrorCS", {"start": v(265.54, -22.02) * mm, "mid": v(266.18, -21.89) * mm, "end": v(266.69, -22.3) * mm});
            skArc(sketch, "E958.MirrorCS", {"start": v(245.26, -33.96) * mm, "mid": v(245.9, -34.02) * mm, "end": v(246.27, -34.55) * mm});
            skArc(sketch, "E959.MirrorCS", {"start": v(292.14, 23.34) * mm, "mid": v(292.54, 23.86) * mm, "end": v(293.19, 23.87) * mm});
            skArc(sketch, "E960.MirrorCS", {"start": v(178.37, -28.54) * mm, "mid": v(177.72, -28.5) * mm, "end": v(177.26, -28.96) * mm});
            skArc(sketch, "E961.MirrorCS", {"start": v(147.77, -11.47) * mm, "mid": v(148.2, -11.77) * mm, "end": v(148.7, -11.73) * mm});
            skArc(sketch, "E962.MirrorCS", {"start": v(206.7, -39.55) * mm, "mid": v(206.64, -38.9) * mm, "end": v(206.11, -38.52) * mm});
            skLineSegment(sketch, "E963.MirrorCS", {"start": v(270.45, -17.53) * mm, "end": v(273.5, -14.22) * mm});
            skLineSegment(sketch, "E964.MirrorCS", {"start": v(252.15, -30.8) * mm, "end": v(256.05, -28.54) * mm});
            skArc(sketch, "E965.MirrorCS", {"start": v(160.91, -14.22) * mm, "mid": v(160.3, -13.97) * mm, "end": v(159.74, -14.28) * mm});
            skArc(sketch, "E966.MirrorCS", {"start": v(139.72, 4.33) * mm, "mid": v(139.43, 3.9) * mm, "end": v(139.48, 3.39) * mm});
            skArc(sketch, "E967.MirrorCS", {"start": v(146.59, 8.2) * mm, "mid": v(146.09, 8.61) * mm, "end": v(145.45, 8.5) * mm});
            skArc(sketch, "E968.MirrorCS", {"start": v(164.6, -28.64) * mm, "mid": v(164.53, -29.15) * mm, "end": v(164.81, -29.59) * mm});
            skLineSegment(sketch, "E969.MirrorCS", {"start": v(139.48, 3.39) * mm, "end": v(140.24, 1.76) * mm});
            skArc(sketch, "E970.MirrorCS", {"start": v(142.53, 18.02) * mm, "mid": v(143.1, 18.31) * mm, "end": v(143.25, 18.95) * mm});
            skArc(sketch, "E971.MirrorCS", {"start": v(256.05, -28.54) * mm, "mid": v(256.7, -28.5) * mm, "end": v(257.15, -28.96) * mm});
            skLineSegment(sketch, "E972.MirrorCS", {"start": v(175.3, -36.56) * mm, "end": v(176.85, -37.46) * mm});
            skArc(sketch, "E973.MirrorCS", {"start": v(287.6, 8.3) * mm, "mid": v(288.08, 8.73) * mm, "end": v(288.72, 8.64) * mm});
            skLineSegment(sketch, "E974.MirrorCS", {"start": v(187.53, -42.39) * mm, "end": v(189.21, -43) * mm});
            skArc(sketch, "E975.MirrorCS", {"start": v(273.5, -14.22) * mm, "mid": v(274.1, -13.97) * mm, "end": v(274.68, -14.28) * mm});
            skArc(sketch, "E976.MirrorCS", {"start": v(232.74, -37.74) * mm, "mid": v(233.36, -37.91) * mm, "end": v(233.63, -38.5) * mm});
            skLineSegment(sketch, "E977.MirrorCS", {"start": v(232.87, -46.33) * mm, "end": v(231.1, -46.64) * mm});
            skArc(sketch, "E978.MirrorCS", {"start": v(163.8, -18.7) * mm, "mid": v(164.16, -18.15) * mm, "end": v(163.96, -17.53) * mm});
            skLineSegment(sketch, "E979.MirrorCS", {"start": v(278.82, -20.95) * mm, "end": v(277.6, -22.27) * mm});
            skLineSegment(sketch, "E980.MirrorCS", {"start": v(294.92, 3.81) * mm, "end": v(294.24, 2.16) * mm});
            skLineSegment(sketch, "E981.MirrorCS", {"start": v(259.11, -36.56) * mm, "end": v(257.56, -37.46) * mm});
            skArc(sketch, "E982.MirrorCS", {"start": v(201.68, -37.74) * mm, "mid": v(201.05, -37.91) * mm, "end": v(200.79, -38.5) * mm});
            skLineSegment(sketch, "E983.MirrorCS", {"start": v(182.26, -30.8) * mm, "end": v(178.37, -28.54) * mm});
            skArc(sketch, "E984.MirrorCS", {"start": v(187.04, -41.55) * mm, "mid": v(187.13, -42.06) * mm, "end": v(187.53, -42.39) * mm});
            skArc(sketch, "E985.MirrorCS", {"start": v(172.5, -25.93) * mm, "mid": v(172.75, -25.33) * mm, "end": v(172.45, -24.75) * mm});
            skArc(sketch, "E986.MirrorCS", {"start": v(146.82, -9.04) * mm, "mid": v(146.61, -9.5) * mm, "end": v(146.75, -10) * mm});
            skLineSegment(sketch, "E987.MirrorCS", {"start": v(155.6, -20.95) * mm, "end": v(156.8, -22.27) * mm});
            skArc(sketch, "E988.MirrorCS", {"start": v(294.64, 4.74) * mm, "mid": v(294.95, 4.33) * mm, "end": v(294.92, 3.81) * mm});
            skArc(sketch, "E989.MirrorCS", {"start": v(155.54, -19.99) * mm, "mid": v(155.4, -20.48) * mm, "end": v(155.6, -20.95) * mm});
            skArc(sketch, "E990.MirrorCS", {"start": v(257.56, -37.46) * mm, "mid": v(257.06, -37.55) * mm, "end": v(256.6, -37.3) * mm});
            skArc(sketch, "E991.MirrorCS", {"start": v(301.09, 38.06) * mm, "mid": v(301.53, 37.8) * mm, "end": v(301.7, 37.3) * mm});
            skArc(sketch, "E992.MirrorCS", {"start": v(233.5, -45.59) * mm, "mid": v(233.32, -46.07) * mm, "end": v(232.87, -46.33) * mm});
            skArc(sketch, "E993.MirrorCS", {"start": v(277.6, -22.27) * mm, "mid": v(277.15, -22.51) * mm, "end": v(276.65, -22.4) * mm});
            skArc(sketch, "E994.MirrorCS", {"start": v(294.24, 2.16) * mm, "mid": v(293.9, 1.78) * mm, "end": v(293.38, 1.7) * mm});
            skArc(sketch, "E995.MirrorCS", {"start": v(231.1, -46.64) * mm, "mid": v(230.6, -46.55) * mm, "end": v(230.27, -46.16) * mm});
            skArc(sketch, "E996.MirrorCS", {"start": v(278.87, -19.99) * mm, "mid": v(279.02, -20.48) * mm, "end": v(278.82, -20.95) * mm});
            skLineSegment(sketch, "E997.MirrorCS", {"start": v(164.81, -29.59) * mm, "end": v(166.24, -30.67) * mm});
            skArc(sketch, "E998.MirrorCS", {"start": v(251.96, -31.95) * mm, "mid": v(251.78, -31.33) * mm, "end": v(252.15, -30.8) * mm});
            skArc(sketch, "E999.MirrorCS", {"start": v(200.91, -45.59) * mm, "mid": v(201.1, -46.07) * mm, "end": v(201.54, -46.33) * mm});
            skArc(sketch, "E1000.MirrorCS", {"start": v(193.78, -36.6) * mm, "mid": v(193.84, -35.96) * mm, "end": v(193.38, -35.5) * mm});
            skArc(sketch, "E1001.MirrorCS", {"start": v(174.96, -35.65) * mm, "mid": v(174.97, -36.17) * mm, "end": v(175.3, -36.56) * mm});
            skArc(sketch, "E1002.MirrorCS", {"start": v(293.23, 38.66) * mm, "mid": v(293.5, 39.25) * mm, "end": v(294.13, 39.41) * mm});
            skArc(sketch, "E1003.MirrorCS", {"start": v(286.44, 3.1) * mm, "mid": v(285.92, 3.49) * mm, "end": v(285.89, 4.14) * mm});
            skArc(sketch, "E1004.MirrorCS", {"start": v(259.45, -35.65) * mm, "mid": v(259.45, -36.17) * mm, "end": v(259.11, -36.56) * mm});
            skArc(sketch, "E1005.MirrorCS", {"start": v(227.72, -39.55) * mm, "mid": v(227.77, -38.9) * mm, "end": v(228.3, -38.52) * mm});
            skArc(sketch, "E1006.MirrorCS", {"start": v(270.61, -18.7) * mm, "mid": v(270.26, -18.15) * mm, "end": v(270.45, -17.53) * mm});
            skLineSegment(sketch, "E1007.MirrorCS", {"start": v(172.45, -24.75) * mm, "end": v(168.87, -22.02) * mm});
            skLineSegment(sketch, "E1008.MirrorCS", {"start": v(285.89, 4.14) * mm, "end": v(287.6, 8.3) * mm});
            skLineSegment(sketch, "E1009.MirrorCS", {"start": v(278.92, -7.72) * mm, "end": v(281.5, -4.03) * mm});
            skLineSegment(sketch, "E1010.MirrorCS", {"start": v(155.5, -7.72) * mm, "end": v(152.91, -4.03) * mm});
            skLineSegment(sketch, "E1011.MirrorCS", {"start": v(148.5, 4.12) * mm, "end": v(146.59, 8.2) * mm});
            skPoint(sketch, "E1012.MirrorP", {"position": v(218.73, -47.8) * mm});
            skPoint(sketch, "E1013.MirrorP", {"position": v(220.38, -39.32) * mm});
            skPoint(sketch, "E1014.MirrorP", {"position": v(214.03, -39.32) * mm});
            skLineSegment(sketch, "E1015.MirrorCS", {"start": v(215.56, -47.18) * mm, "end": v(214.2, -40.23) * mm});
            skPoint(sketch, "E1016.MirrorP", {"position": v(215.68, -47.8) * mm});
            skLineSegment(sketch, "E1017.MirrorCS", {"start": v(141.24, 39.02) * mm, "end": v(141.24, 34.52) * mm});
            skLineSegment(sketch, "E1018.MirrorCS", {"start": v(220.2, -40.23) * mm, "end": v(218.85, -47.18) * mm});
            skPoint(sketch, "E1019.MirrorP", {"position": v(148.13, -11.98) * mm});
            skPoint(sketch, "E1020.MirrorP", {"position": v(282.03, -3.27) * mm});
            skPoint(sketch, "E1021.MirrorP", {"position": v(177.57, -28.08) * mm});
            skPoint(sketch, "E1022.MirrorP", {"position": v(292.34, 24.24) * mm});
            skPoint(sketch, "E1023.MirrorP", {"position": v(246.13, -33.64) * mm});
            skPoint(sketch, "E1024.MirrorP", {"position": v(266.28, -21.46) * mm});
            skPoint(sketch, "E1025.MirrorP", {"position": v(156.03, -8.47) * mm});
            skPoint(sketch, "E1026.MirrorP", {"position": v(168.14, -21.46) * mm});
            skPoint(sketch, "E1027.MirrorP", {"position": v(140.5, 1.2) * mm});
            skPoint(sketch, "E1028.MirrorP", {"position": v(288.03, -9.49) * mm});
            skPoint(sketch, "E1029.MirrorP", {"position": v(300.26, 20.8) * mm});
            skPoint(sketch, "E1030.MirrorP", {"position": v(134.16, 20.8) * mm});
            skPoint(sketch, "E1031.MirrorP", {"position": v(247.48, -42.17) * mm});
            skPoint(sketch, "E1032.MirrorP", {"position": v(270.1, -29.2) * mm});
            skPoint(sketch, "E1033.MirrorP", {"position": v(160.29, -13.54) * mm});
            skPoint(sketch, "E1034.MirrorP", {"position": v(183.06, -31.26) * mm});
            skPoint(sketch, "E1035.MirrorP", {"position": v(174.76, -36.25) * mm});
            skPoint(sketch, "E1036.MirrorP", {"position": v(188.29, -33.64) * mm});
            skPoint(sketch, "E1037.MirrorP", {"position": v(177.4, -37.77) * mm});
            skPoint(sketch, "E1038.MirrorP", {"position": v(164.59, -18.2) * mm});
            skPoint(sketch, "E1039.MirrorP", {"position": v(152.38, -3.27) * mm});
            skPoint(sketch, "E1040.MirrorP", {"position": v(194.25, -35.81) * mm});
            skPoint(sketch, "E1041.MirrorP", {"position": v(200.77, -37.58) * mm});
            skPoint(sketch, "E1042.MirrorP", {"position": v(261.23, -25.31) * mm});
            skPoint(sketch, "E1043.MirrorP", {"position": v(240.16, -35.81) * mm});
            skPoint(sketch, "E1044.MirrorP", {"position": v(146.39, -9.49) * mm});
            skPoint(sketch, "E1045.MirrorP", {"position": v(290.96, 18.05) * mm});
            skPoint(sketch, "E1046.MirrorP", {"position": v(166.74, -31.05) * mm});
            skPoint(sketch, "E1047.MirrorP", {"position": v(278.39, -8.47) * mm});
            skLineSegment(sketch, "E1048.MirrorCS", {"start": v(241.03, -35.5) * mm, "end": v(245.26, -33.96) * mm});
            skLineSegment(sketch, "E1049.MirrorCS", {"start": v(140.33, 33.77) * mm, "end": v(133.38, 35.12) * mm});
            skPoint(sketch, "E1050.MirrorP", {"position": v(186.94, -42.17) * mm});
            skPoint(sketch, "E1051.MirrorP", {"position": v(207.02, -38.69) * mm});
            skLineSegment(sketch, "E1052.MirrorCS", {"start": v(266.69, -22.3) * mm, "end": v(269.82, -28.64) * mm});
            skLineSegment(sketch, "E1053.MirrorCS", {"start": v(246.27, -34.55) * mm, "end": v(247.38, -41.55) * mm});
            skLineSegment(sketch, "E1054.MirrorCS", {"start": v(293.19, 23.87) * mm, "end": v(299.68, 21.04) * mm});
            skLineSegment(sketch, "E1055.MirrorCS", {"start": v(282.67, -3.94) * mm, "end": v(287.6, -9.04) * mm});
            skLineSegment(sketch, "E1056.MirrorCS", {"start": v(151.74, -3.94) * mm, "end": v(146.82, -9.04) * mm});
            skLineSegment(sketch, "E1057.MirrorCS", {"start": v(133.38, 38.41) * mm, "end": v(140.33, 39.77) * mm});
            skLineSegment(sketch, "E1058.MirrorCS", {"start": v(218.85, -47.18) * mm, "end": v(220.2, -40.23) * mm});
            skPoint(sketch, "E1059.MirrorP", {"position": v(294, 1.58) * mm});
            skPoint(sketch, "E1060.MirrorP", {"position": v(230.5, -46.75) * mm});
            skPoint(sketch, "E1061.MirrorP", {"position": v(277.18, -22.73) * mm});
            skPoint(sketch, "E1062.MirrorP", {"position": v(257.02, -37.77) * mm});
            skLineSegment(sketch, "E1063.MirrorCS", {"start": v(267.2, -30.64) * mm, "end": v(261.92, -25.93) * mm});
            skPoint(sketch, "E1064.MirrorP", {"position": v(142.07, 24.24) * mm});
            skLineSegment(sketch, "E1065.MirrorCS", {"start": v(244.29, -42.67) * mm, "end": v(240.64, -36.6) * mm});
            skLineSegment(sketch, "E1066.MirrorCS", {"start": v(167.2, -30.64) * mm, "end": v(172.5, -25.93) * mm});
            skLineSegment(sketch, "E1067.MirrorCS", {"start": v(298.97, 17.83) * mm, "end": v(291.89, 18.02) * mm});
            skLineSegment(sketch, "E1068.MirrorCS", {"start": v(285.7, -11.73) * mm, "end": v(279.23, -8.85) * mm});
            skPoint(sketch, "E1069.MirrorP", {"position": v(301.7, 37.94) * mm});
            skLineSegment(sketch, "E1070.MirrorCS", {"start": v(190.13, -42.67) * mm, "end": v(193.78, -36.6) * mm});
            skLineSegment(sketch, "E1071.MirrorCS", {"start": v(135.45, 17.83) * mm, "end": v(142.53, 18.02) * mm});
            skLineSegment(sketch, "E1072.MirrorCS", {"start": v(148.7, -11.73) * mm, "end": v(155.18, -8.85) * mm});
            skLineSegment(sketch, "E1073.MirrorCS", {"start": v(206.11, -38.52) * mm, "end": v(201.68, -37.74) * mm});
            skLineSegment(sketch, "E1074.MirrorCS", {"start": v(294.13, 39.41) * mm, "end": v(301.09, 38.06) * mm});
            skLineSegment(sketch, "E1075.MirrorCS", {"start": v(228.3, -38.52) * mm, "end": v(232.74, -37.74) * mm});
            skLineSegment(sketch, "E1076.MirrorCS", {"start": v(193.38, -35.5) * mm, "end": v(189.15, -33.96) * mm});
            skLineSegment(sketch, "E1077.MirrorCS", {"start": v(159.74, -14.28) * mm, "end": v(155.54, -19.99) * mm});
            skLineSegment(sketch, "E1078.MirrorCS", {"start": v(274.68, -14.28) * mm, "end": v(278.87, -19.99) * mm});
            skLineSegment(sketch, "E1079.MirrorCS", {"start": v(233.63, -38.5) * mm, "end": v(233.5, -45.59) * mm});
            skLineSegment(sketch, "E1080.MirrorCS", {"start": v(257.15, -28.96) * mm, "end": v(259.45, -35.65) * mm});
            skLineSegment(sketch, "E1081.MirrorCS", {"start": v(288.72, 8.64) * mm, "end": v(294.64, 4.74) * mm});
            skLineSegment(sketch, "E1082.MirrorCS", {"start": v(143.25, 18.95) * mm, "end": v(142.27, 23.34) * mm});
            skLineSegment(sketch, "E1083.MirrorCS", {"start": v(177.26, -28.96) * mm, "end": v(174.96, -35.65) * mm});
            skLineSegment(sketch, "E1084.MirrorCS", {"start": v(141.23, 23.87) * mm, "end": v(134.73, 21.04) * mm});
            skPoint(sketch, "E1085.MirrorP", {"position": v(173.19, -25.31) * mm});
            skPoint(sketch, "E1086.MirrorP", {"position": v(189.8, -43.21) * mm});
            skPoint(sketch, "E1087.MirrorP", {"position": v(251.35, -31.26) * mm});
            skPoint(sketch, "E1088.MirrorP", {"position": v(157.24, -22.73) * mm});
            skLineSegment(sketch, "E1089.MirrorCS", {"start": v(291.16, 18.95) * mm, "end": v(292.14, 23.34) * mm});
            skPoint(sketch, "E1090.MirrorP", {"position": v(227.4, -38.69) * mm});
            skPoint(sketch, "E1091.MirrorP", {"position": v(285.53, 3.28) * mm});
            skPoint(sketch, "E1092.MirrorP", {"position": v(269.83, -18.2) * mm});
            skPoint(sketch, "E1093.MirrorP", {"position": v(200.92, -46.22) * mm});
            skPoint(sketch, "E1094.MirrorP", {"position": v(148.88, 3.28) * mm});
            skPoint(sketch, "E1095.MirrorP", {"position": v(146.2, 9.04) * mm});
            skPoint(sketch, "E1096.MirrorP", {"position": v(143.45, 18.05) * mm});
            skPoint(sketch, "E1097.MirrorP", {"position": v(203.92, -46.75) * mm});
            skPoint(sketch, "E1098.MirrorP", {"position": v(134.82, 17.82) * mm});
            skPoint(sketch, "E1099.MirrorP", {"position": v(256.85, -28.08) * mm});
            skLineSegment(sketch, "E1100.MirrorCS", {"start": v(188.14, -34.55) * mm, "end": v(187.04, -41.55) * mm});
            skLineSegment(sketch, "E1101.MirrorCS", {"start": v(141.1, 1.35) * mm, "end": v(147.98, 3.06) * mm});
            skPoint(sketch, "E1102.MirrorP", {"position": v(233.65, -37.58) * mm});
            skPoint(sketch, "E1103.MirrorP", {"position": v(287.95, 9.15) * mm});
            skPoint(sketch, "E1104.MirrorP", {"position": v(274.13, -13.54) * mm});
            skPoint(sketch, "E1105.MirrorP", {"position": v(279.24, -20.5) * mm});
            skPoint(sketch, "E1106.MirrorP", {"position": v(155.17, -20.5) * mm});
            skLineSegment(sketch, "E1107.MirrorCS", {"start": v(200.79, -38.5) * mm, "end": v(200.91, -45.59) * mm});
            skPoint(sketch, "E1108.MirrorP", {"position": v(295.16, 4.4) * mm});
            skPoint(sketch, "E1109.MirrorP", {"position": v(267.68, -31.05) * mm});
            skPoint(sketch, "E1110.MirrorP", {"position": v(293.23, 39.59) * mm});
            skPoint(sketch, "E1111.MirrorP", {"position": v(233.5, -46.22) * mm});
            skPoint(sketch, "E1112.MirrorP", {"position": v(259.66, -36.25) * mm});
            skLineSegment(sketch, "E1113.MirrorCS", {"start": v(214.2, -40.23) * mm, "end": v(215.56, -47.18) * mm});
            skPoint(sketch, "E1114.MirrorP", {"position": v(244.61, -43.21) * mm});
            skLineSegment(sketch, "E1115.MirrorCS", {"start": v(204.15, -46.16) * mm, "end": v(206.7, -39.55) * mm});
            skPoint(sketch, "E1116.MirrorP", {"position": v(139.21, 3.96) * mm});
            skPoint(sketch, "E1117.MirrorP", {"position": v(164.31, -29.2) * mm});
            skLineSegment(sketch, "E1118.MirrorCS", {"start": v(230.27, -46.16) * mm, "end": v(227.72, -39.55) * mm});
            skPoint(sketch, "E1119.MirrorP", {"position": v(299.6, 17.82) * mm});
            skPoint(sketch, "E1120.MirrorP", {"position": v(286.28, -11.98) * mm});
            skLineSegment(sketch, "E1121.MirrorCS", {"start": v(167.73, -22.3) * mm, "end": v(164.6, -28.64) * mm});
            skLineSegment(sketch, "E1122.MirrorCS", {"start": v(157.77, -22.4) * mm, "end": v(163.8, -18.7) * mm});
            skLineSegment(sketch, "E1123.MirrorCS", {"start": v(177.8, -37.3) * mm, "end": v(182.46, -31.95) * mm});
            skLineSegment(sketch, "E1124.MirrorCS", {"start": v(293.38, 1.7) * mm, "end": v(286.44, 3.1) * mm});
            skLineSegment(sketch, "E1125.MirrorCS", {"start": v(145.45, 8.5) * mm, "end": v(139.72, 4.33) * mm});
            skLineSegment(sketch, "E1126.MirrorCS", {"start": v(276.65, -22.4) * mm, "end": v(270.61, -18.7) * mm});
            skLineSegment(sketch, "E1127.MirrorCS", {"start": v(256.6, -37.3) * mm, "end": v(251.96, -31.95) * mm});
            skLineSegment(sketch, "E1128", {"start": v(301.7, 37.3) * mm, "end": v(301.7, 36.23) * mm});
            skSolve(sketch);
        }
        {
            var Q0;
            Q0=makeQuery(id+"F0.imprint","IMPRINT",FACE,{"disambiguationData":[TD([[makeQuery(id+"F0.imprint","IMPRINT",EDGE,{"derivedFrom":sQuery(id+"F0.wireOp",EDGE,"E925.MirrorCS")}),1.0]])]});
            var Q1;
            Q1=makeQuery(id+"F0.imprint","IMPRINT",FACE,{"disambiguationData":[TD([[makeQuery(id+"F0.imprint","IMPRINT",EDGE,{"derivedFrom":sQuery(id+"F0.wireOp",EDGE,"E805.MirrorCS")}),-1.0]])]});
            var Q2;
            Q2=makeQuery(id+"F0.imprint","IMPRINT",FACE,{"disambiguationData":[TD([[makeQuery(id+"F0.imprint","IMPRINT",EDGE,{"derivedFrom":sQuery(id+"F0.wireOp",EDGE,"E807.MirrorCS")}),-1.0]])]});
            var Q3;
            {var subQ4=sQuery(id+"F0.wireOp",EDGE,"E916.MirrorCS");Q3=makeQuery(id+"F0.imprint","IMPRINT",FACE,{"disambiguationData":[TD([[makeQuery(id+"F0.imprint","IMPRINT",EDGE,{"derivedFrom":subQ4}),-1.0]])]});}
            var Q4;
            Q4=makeQuery(id+"F0.imprint","IMPRINT",FACE,{"disambiguationData":[TD([[makeQuery(id+"F0.imprint","IMPRINT",EDGE,{"derivedFrom":sQuery(id+"F0.wireOp",EDGE,"E929.MirrorCS")}),-1.0]])]});
            var Q5;
            Q5=makeQuery(id+"F0.imprint","IMPRINT",FACE,{"disambiguationData":[TD([[makeQuery(id+"F0.imprint","IMPRINT",EDGE,{"derivedFrom":sQuery(id+"F0.wireOp",EDGE,"E926.MirrorCS")}),-1.0]])]});
            var Q6;
            Q6=makeQuery(id+"F0.imprint","IMPRINT",FACE,{"disambiguationData":[TD([[makeQuery(id+"F0.imprint","IMPRINT",EDGE,{"derivedFrom":sQuery(id+"F0.wireOp",EDGE,"E981.MirrorCS")}),-1.0]])]});
            var Q7;
            {var subQ1=sQuery(id+"F0.wireOp",EDGE,"E744");Q7=makeQuery(id+"F0.imprint","IMPRINT",FACE,{"disambiguationData":[TD([[makeQuery(id+"F0.imprint","IMPRINT",EDGE,{"derivedFrom":subQ1}),1.0]])]});}
            var Q8;
            {var subQ1=sQuery(id+"F0.wireOp",EDGE,"E736");Q8=makeQuery(id+"F0.imprint","IMPRINT",FACE,{"disambiguationData":[TD([[makeQuery(id+"F0.imprint","IMPRINT",EDGE,{"derivedFrom":subQ1}),1.0]])]});}
            var Q9;
            {var subQ1=sQuery(id+"F0.wireOp",EDGE,"E784");Q9=makeQuery(id+"F0.imprint","IMPRINT",FACE,{"disambiguationData":[TD([[makeQuery(id+"F0.imprint","IMPRINT",EDGE,{"derivedFrom":subQ1}),1.0]])]});}
            var Q10;
            Q10=makeQuery(id+"F0.imprint","IMPRINT",FACE,{"disambiguationData":[TD([[makeQuery(id+"F0.imprint","IMPRINT",EDGE,{"derivedFrom":sQuery(id+"F0.wireOp",EDGE,"E835.MirrorCS")}),-1.0]])]});
            var Q11;
            Q11=makeQuery(id+"F0.imprint","IMPRINT",FACE,{"disambiguationData":[TD([[makeQuery(id+"F0.imprint","IMPRINT",EDGE,{"derivedFrom":sQuery(id+"F0.wireOp",EDGE,"E3")}),-1.0]])]});
            var Q12;
            Q12=makeQuery(id+"F0.imprint","IMPRINT",FACE,{"disambiguationData":[TD([[makeQuery(id+"F0.imprint","IMPRINT",EDGE,{"derivedFrom":sQuery(id+"F0.wireOp",EDGE,"E977.MirrorCS")}),-1.0]])]});
            var Q13;
            Q13=makeQuery(id+"F0.imprint","IMPRINT",FACE,{"disambiguationData":[TD([[makeQuery(id+"F0.imprint","IMPRINT",EDGE,{"derivedFrom":sQuery(id+"F0.wireOp",EDGE,"E931.MirrorCS")}),1.0]])]});
            var Q14;
            Q14=makeQuery(id+"F0.imprint","IMPRINT",FACE,{"disambiguationData":[TD([[makeQuery(id+"F0.imprint","IMPRINT",EDGE,{"derivedFrom":sQuery(id+"F0.wireOp",EDGE,"E760")}),1.0]])]});
            var Q15;
            {var subQ1=sQuery(id+"F0.wireOp",EDGE,"E724");Q15=makeQuery(id+"F0.imprint","IMPRINT",FACE,{"disambiguationData":[TD([[makeQuery(id+"F0.imprint","IMPRINT",EDGE,{"derivedFrom":subQ1}),1.0]])]});}
            var Q16;
            Q16=makeQuery(id+"F0.imprint","IMPRINT",FACE,{"disambiguationData":[TD([[makeQuery(id+"F0.imprint","IMPRINT",EDGE,{"derivedFrom":sQuery(id+"F0.wireOp",EDGE,"E792")}),1.0]])]});
            var Q17;
            Q17=makeQuery(id+"F0.imprint","IMPRINT",FACE,{"disambiguationData":[TD([[makeQuery(id+"F0.imprint","IMPRINT",EDGE,{"derivedFrom":sQuery(id+"F0.wireOp",EDGE,"E922.MirrorCS")}),-1.0]])]});
            var Q18;
            Q18=makeQuery(id+"F0.imprint","IMPRINT",FACE,{"disambiguationData":[TD([[makeQuery(id+"F0.imprint","IMPRINT",EDGE,{"derivedFrom":sQuery(id+"F0.wireOp",EDGE,"E917.MirrorCS")}),1.0]])]});
            var Q19;
            Q19=makeQuery(id+"F0.imprint","IMPRINT",FACE,{"disambiguationData":[TD([[makeQuery(id+"F0.imprint","IMPRINT",EDGE,{"derivedFrom":sQuery(id+"F0.wireOp",EDGE,"E934.MirrorCS")}),1.0]])]});
            var Q20;
            Q20=makeQuery(id+"F0.imprint","IMPRINT",FACE,{"disambiguationData":[TD([[makeQuery(id+"F0.imprint","IMPRINT",EDGE,{"derivedFrom":sQuery(id+"F0.wireOp",EDGE,"E938.MirrorCS")}),1.0]])]});
            var Q21;
            Q21=makeQuery(id+"F0.imprint","IMPRINT",FACE,{"disambiguationData":[TD([[makeQuery(id+"F0.imprint","IMPRINT",EDGE,{"derivedFrom":sQuery(id+"F0.wireOp",EDGE,"E908.MirrorCS")}),-1.0]])]});
            var Q22;
            Q22=makeQuery(id+"F0.imprint","IMPRINT",FACE,{"disambiguationData":[TD([[makeQuery(id+"F0.imprint","IMPRINT",EDGE,{"derivedFrom":sQuery(id+"F0.wireOp",EDGE,"E941.MirrorCS")}),1.0]])]});
            var Q23;
            {var subQ1=sQuery(id+"F0.wireOp",EDGE,"E752");Q23=makeQuery(id+"F0.imprint","IMPRINT",FACE,{"disambiguationData":[TD([[makeQuery(id+"F0.imprint","IMPRINT",EDGE,{"derivedFrom":subQ1}),1.0]])]});}
            var Q24;
            {var subQ0=sQuery(id+"F0.wireOp",EDGE,"E768");Q24=makeQuery(id+"F0.imprint","IMPRINT",FACE,{"disambiguationData":[TD([[makeQuery(id+"F0.imprint","IMPRINT",EDGE,{"derivedFrom":subQ0}),1.0]])]});}
            var Q25;
            Q25=makeQuery(id+"F0.imprint","IMPRINT",FACE,{"disambiguationData":[TD([[makeQuery(id+"F0.imprint","IMPRINT",EDGE,{"derivedFrom":sQuery(id+"F0.wireOp",EDGE,"E979.MirrorCS")}),-1.0]])]});
            var Q26;
            Q26=makeQuery(id+"F0.imprint","IMPRINT",FACE,{"disambiguationData":[TD([[makeQuery(id+"F0.imprint","IMPRINT",EDGE,{"derivedFrom":sQuery(id+"F0.wireOp",EDGE,"E927.MirrorCS")}),-1.0]])]});
            var Q27;
            Q27=makeQuery(id+"F0.imprint","IMPRINT",FACE,{"disambiguationData":[TD([[makeQuery(id+"F0.imprint","IMPRINT",EDGE,{"derivedFrom":sQuery(id+"F0.wireOp",EDGE,"E808.MirrorCS")}),-1.0]])]});
            var Q28;
            Q28=makeQuery(id+"F0.imprint","IMPRINT",FACE,{"disambiguationData":[TD([[makeQuery(id+"F0.imprint","IMPRINT",EDGE,{"derivedFrom":sQuery(id+"F0.wireOp",EDGE,"E836.MirrorCS")}),-1.0]])]});
            var Q29;
            Q29=makeQuery(id+"F0.imprint","IMPRINT",FACE,{"disambiguationData":[TD([[makeQuery(id+"F0.imprint","IMPRINT",EDGE,{"derivedFrom":sQuery(id+"F0.wireOp",EDGE,"E834.MirrorCS")}),-1.0]])]});
            var Q30;
            Q30=makeQuery(id+"F0.imprint","IMPRINT",FACE,{"disambiguationData":[TD([[makeQuery(id+"F0.imprint","IMPRINT",EDGE,{"derivedFrom":sQuery(id+"F0.wireOp",EDGE,"E804.MirrorCS")}),-1.0]])]});
            var Q31;
            Q31=makeQuery(id+"F0.imprint","IMPRINT",FACE,{"disambiguationData":[TD([[makeQuery(id+"F0.imprint","IMPRINT",EDGE,{"derivedFrom":sQuery(id+"F0.wireOp",EDGE,"E806.MirrorCS")}),-1.0]])]});
            var Q32;
            Q32=makeQuery(id+"F0.imprint","IMPRINT",FACE,{"disambiguationData":[TD([[makeQuery(id+"F0.imprint","IMPRINT",EDGE,{"derivedFrom":sQuery(id+"F0.wireOp",EDGE,"E914.MirrorCS")}),1.0]])]});
            var Q33;
            {var subQ6=sQuery(id+"F0.wireOp",EDGE,"E776");Q33=makeQuery(id+"F0.imprint","IMPRINT",FACE,{"disambiguationData":[TD([[makeQuery(id+"F0.imprint","IMPRINT",EDGE,{"derivedFrom":subQ6}),1.0]])]});}
            var Q34;
            Q34=makeQuery(id+"F0.imprint","IMPRINT",FACE,{"disambiguationData":[TD([[makeQuery(id+"F0.imprint","IMPRINT",EDGE,{"derivedFrom":sQuery(id+"F0.wireOp",EDGE,"E924.MirrorCS")}),1.0]])]});
            var Q35;
            Q35=makeQuery(id+"F0.imprint","IMPRINT",FACE,{"disambiguationData":[TD([[makeQuery(id+"F0.imprint","IMPRINT",EDGE,{"derivedFrom":sQuery(id+"F0.wireOp",EDGE,"E980.MirrorCS")}),-1.0]])]});
            var Q36;
            Q36=makeQuery(id+"F0.imprint","IMPRINT",FACE,{"disambiguationData":[TD([[makeQuery(id+"F0.imprint","IMPRINT",EDGE,{"derivedFrom":sQuery(id+"F0.wireOp",EDGE,"E799.MirrorCS")}),-1.0]])]});
            var Q37;
            {var subQ5=sQuery(id+"F0.wireOp",EDGE,"E849.MirrorCS");Q37=makeQuery(id+"F0.imprint","IMPRINT",FACE,{"disambiguationData":[TD([[makeQuery(id+"F0.imprint","IMPRINT",EDGE,{"derivedFrom":subQ5}),-1.0]])]});}
            var Q38;
            {var subQ0=sQuery(id+"F0.wireOp",EDGE,"E953.MirrorCS");var subQ1=sQuery(id+"F0.wireOp",EDGE,"E1");var subQ2=makeQuery(id+"F0.imprint","INTERSECT",VERTEX,{"derivedFrom":[subQ1,subQ0]});Q38=makeQuery(id+"F0.imprint","IMPRINT",FACE,{"disambiguationData":[TD([[makeQuery(id+"F0.imprint","IMPRINT",EDGE,{"disambiguationData":[TD([[subQ2,-1.0]])],"derivedFrom":subQ1}),1.0]])]});}
            var Q39;
            {var subQ5=sQuery(id+"F0.wireOp",EDGE,"E775");Q39=makeQuery(id+"F0.imprint","IMPRINT",FACE,{"disambiguationData":[TD([[makeQuery(id+"F0.imprint","IMPRINT",EDGE,{"derivedFrom":subQ5}),1.0]])]});}
            var Q40;
            {var subQ5=sQuery(id+"F0.wireOp",EDGE,"E983.MirrorCS");Q40=makeQuery(id+"F0.imprint","IMPRINT",FACE,{"disambiguationData":[TD([[makeQuery(id+"F0.imprint","IMPRINT",EDGE,{"derivedFrom":subQ5}),1.0]])]});}
            var Q41;
            {var subQ5=sQuery(id+"F0.wireOp",EDGE,"E767");Q41=makeQuery(id+"F0.imprint","IMPRINT",FACE,{"disambiguationData":[TD([[makeQuery(id+"F0.imprint","IMPRINT",EDGE,{"derivedFrom":subQ5}),1.0]])]});}
            var Q42;
            {var subQ5=sQuery(id+"F0.wireOp",EDGE,"E1007.MirrorCS");Q42=makeQuery(id+"F0.imprint","IMPRINT",FACE,{"disambiguationData":[TD([[makeQuery(id+"F0.imprint","IMPRINT",EDGE,{"derivedFrom":subQ5}),1.0]])]});}
            var Q43;
            {var subQ5=sQuery(id+"F0.wireOp",EDGE,"E952.MirrorCS");Q43=makeQuery(id+"F0.imprint","IMPRINT",FACE,{"disambiguationData":[TD([[makeQuery(id+"F0.imprint","IMPRINT",EDGE,{"derivedFrom":subQ5}),1.0]])]});}
            var Q44;
            {var subQ5=sQuery(id+"F0.wireOp",EDGE,"E751");Q44=makeQuery(id+"F0.imprint","IMPRINT",FACE,{"disambiguationData":[TD([[makeQuery(id+"F0.imprint","IMPRINT",EDGE,{"derivedFrom":subQ5}),1.0]])]});}
            var Q45;
            {var subQ5=sQuery(id+"F0.wireOp",EDGE,"E1010.MirrorCS");Q45=makeQuery(id+"F0.imprint","IMPRINT",FACE,{"disambiguationData":[TD([[makeQuery(id+"F0.imprint","IMPRINT",EDGE,{"derivedFrom":subQ5}),1.0]])]});}
            var Q46;
            {var subQ5=sQuery(id+"F0.wireOp",EDGE,"E1073.MirrorCS");Q46=makeQuery(id+"F0.imprint","IMPRINT",FACE,{"disambiguationData":[TD([[makeQuery(id+"F0.imprint","IMPRINT",EDGE,{"derivedFrom":subQ5}),1.0]])]});}
            var Q47;
            {var subQ5=sQuery(id+"F0.wireOp",EDGE,"E735");Q47=makeQuery(id+"F0.imprint","IMPRINT",FACE,{"disambiguationData":[TD([[makeQuery(id+"F0.imprint","IMPRINT",EDGE,{"derivedFrom":subQ5}),1.0]])]});}
            var Q48;
            {var subQ5=sQuery(id+"F0.wireOp",EDGE,"E1076.MirrorCS");Q48=makeQuery(id+"F0.imprint","IMPRINT",FACE,{"disambiguationData":[TD([[makeQuery(id+"F0.imprint","IMPRINT",EDGE,{"derivedFrom":subQ5}),1.0]])]});}
            var Q49;
            {var subQ5=sQuery(id+"F0.wireOp",EDGE,"E847.MirrorCS");Q49=makeQuery(id+"F0.imprint","IMPRINT",FACE,{"disambiguationData":[TD([[makeQuery(id+"F0.imprint","IMPRINT",EDGE,{"derivedFrom":subQ5}),-1.0]])]});}
            var Q50;
            {var subQ5=sQuery(id+"F0.wireOp",EDGE,"E1082.MirrorCS");Q50=makeQuery(id+"F0.imprint","IMPRINT",FACE,{"disambiguationData":[TD([[makeQuery(id+"F0.imprint","IMPRINT",EDGE,{"derivedFrom":subQ5}),1.0]])]});}
            var Q51;
            {var subQ5=sQuery(id+"F0.wireOp",EDGE,"E803.MirrorCS");Q51=makeQuery(id+"F0.imprint","IMPRINT",FACE,{"disambiguationData":[TD([[makeQuery(id+"F0.imprint","IMPRINT",EDGE,{"derivedFrom":subQ5}),-1.0]])]});}
            var Q52;
            {var subQ5=sQuery(id+"F0.wireOp",EDGE,"E1008.MirrorCS");Q52=makeQuery(id+"F0.imprint","IMPRINT",FACE,{"disambiguationData":[TD([[makeQuery(id+"F0.imprint","IMPRINT",EDGE,{"derivedFrom":subQ5}),-1.0]])]});}
            var Q53;
            {var subQ5=sQuery(id+"F0.wireOp",EDGE,"E850.MirrorCS");Q53=makeQuery(id+"F0.imprint","IMPRINT",FACE,{"disambiguationData":[TD([[makeQuery(id+"F0.imprint","IMPRINT",EDGE,{"derivedFrom":subQ5}),-1.0]])]});}
            var Q54;
            {var subQ5=sQuery(id+"F0.wireOp",EDGE,"E743");Q54=makeQuery(id+"F0.imprint","IMPRINT",FACE,{"disambiguationData":[TD([[makeQuery(id+"F0.imprint","IMPRINT",EDGE,{"derivedFrom":subQ5}),1.0]])]});}
            var Q55;
            {var subQ5=sQuery(id+"F0.wireOp",EDGE,"E783");Q55=makeQuery(id+"F0.imprint","IMPRINT",FACE,{"disambiguationData":[TD([[makeQuery(id+"F0.imprint","IMPRINT",EDGE,{"derivedFrom":subQ5}),1.0]])]});}
            var Q56;
            {var subQ5=sQuery(id+"F0.wireOp",EDGE,"E829.MirrorCS");Q56=makeQuery(id+"F0.imprint","IMPRINT",FACE,{"disambiguationData":[TD([[makeQuery(id+"F0.imprint","IMPRINT",EDGE,{"derivedFrom":subQ5}),-1.0]])]});}
            var Q57;
            {var subQ5=sQuery(id+"F0.wireOp",EDGE,"E802.MirrorCS");Q57=makeQuery(id+"F0.imprint","IMPRINT",FACE,{"disambiguationData":[TD([[makeQuery(id+"F0.imprint","IMPRINT",EDGE,{"derivedFrom":subQ5}),-1.0]])]});}
            var Q58;
            {var subQ5=sQuery(id+"F0.wireOp",EDGE,"E1075.MirrorCS");Q58=makeQuery(id+"F0.imprint","IMPRINT",FACE,{"disambiguationData":[TD([[makeQuery(id+"F0.imprint","IMPRINT",EDGE,{"derivedFrom":subQ5}),-1.0]])]});}
            var Q59;
            {var subQ5=sQuery(id+"F0.wireOp",EDGE,"E1048.MirrorCS");Q59=makeQuery(id+"F0.imprint","IMPRINT",FACE,{"disambiguationData":[TD([[makeQuery(id+"F0.imprint","IMPRINT",EDGE,{"derivedFrom":subQ5}),-1.0]])]});}
            var Q60;
            {var subQ0=sQuery(id+"F0.wireOp",EDGE,"E955.MirrorCS");var subQ1=sQuery(id+"F0.wireOp",EDGE,"E1");var subQ2=makeQuery(id+"F0.imprint","INTERSECT",VERTEX,{"derivedFrom":[subQ1,subQ0]});Q60=makeQuery(id+"F0.imprint","IMPRINT",FACE,{"disambiguationData":[TD([[makeQuery(id+"F0.imprint","IMPRINT",EDGE,{"disambiguationData":[TD([[subQ2,-1.0]])],"derivedFrom":subQ1}),1.0]])]});}
            var Q61;
            {var subQ5=sQuery(id+"F0.wireOp",EDGE,"E1011.MirrorCS");Q61=makeQuery(id+"F0.imprint","IMPRINT",FACE,{"disambiguationData":[TD([[makeQuery(id+"F0.imprint","IMPRINT",EDGE,{"derivedFrom":subQ5}),1.0]])]});}
            var Q62;
            {var subQ5=sQuery(id+"F0.wireOp",EDGE,"E878.MirrorCS");Q62=makeQuery(id+"F0.imprint","IMPRINT",FACE,{"disambiguationData":[TD([[makeQuery(id+"F0.imprint","IMPRINT",EDGE,{"derivedFrom":subQ5}),-1.0]])]});}
            var Q63;
            {var subQ0=sQuery(id+"F0.wireOp",EDGE,"E759");var subQ1=sQuery(id+"F0.wireOp",EDGE,"E1");var subQ2=makeQuery(id+"F0.imprint","INTERSECT",VERTEX,{"derivedFrom":[subQ1,subQ0]});Q63=makeQuery(id+"F0.imprint","IMPRINT",FACE,{"disambiguationData":[TD([[makeQuery(id+"F0.imprint","IMPRINT",EDGE,{"disambiguationData":[TD([[subQ2,-1.0]])],"derivedFrom":subQ1}),1.0]])]});}
            var Q64;
            {var subQ5=sQuery(id+"F0.wireOp",EDGE,"E963.MirrorCS");Q64=makeQuery(id+"F0.imprint","IMPRINT",FACE,{"disambiguationData":[TD([[makeQuery(id+"F0.imprint","IMPRINT",EDGE,{"derivedFrom":subQ5}),-1.0]])]});}
            var Q65;
            {var subQ5=sQuery(id+"F0.wireOp",EDGE,"E921.MirrorCS");Q65=makeQuery(id+"F0.imprint","IMPRINT",FACE,{"disambiguationData":[TD([[makeQuery(id+"F0.imprint","IMPRINT",EDGE,{"derivedFrom":subQ5}),-1.0]])]});}
            var Q66;
            {var subQ0=sQuery(id+"F0.wireOp",EDGE,"E791");var subQ1=sQuery(id+"F0.wireOp",EDGE,"E1");var subQ2=makeQuery(id+"F0.imprint","INTERSECT",VERTEX,{"derivedFrom":[subQ1,subQ0]});Q66=makeQuery(id+"F0.imprint","IMPRINT",FACE,{"disambiguationData":[TD([[makeQuery(id+"F0.imprint","IMPRINT",EDGE,{"disambiguationData":[TD([[subQ2,-1.0]])],"derivedFrom":subQ1}),1.0]])]});}
            var Q67;
            {var subQ5=sQuery(id+"F0.wireOp",EDGE,"E848.MirrorCS");Q67=makeQuery(id+"F0.imprint","IMPRINT",FACE,{"disambiguationData":[TD([[makeQuery(id+"F0.imprint","IMPRINT",EDGE,{"derivedFrom":subQ5}),-1.0]])]});}
            var Q68;
            {var subQ5=sQuery(id+"F0.wireOp",EDGE,"E964.MirrorCS");Q68=makeQuery(id+"F0.imprint","IMPRINT",FACE,{"disambiguationData":[TD([[makeQuery(id+"F0.imprint","IMPRINT",EDGE,{"derivedFrom":subQ5}),-1.0]])]});}
            var Q69;
            {var subQ5=sQuery(id+"F0.wireOp",EDGE,"E918.MirrorCS");Q69=makeQuery(id+"F0.imprint","IMPRINT",FACE,{"disambiguationData":[TD([[makeQuery(id+"F0.imprint","IMPRINT",EDGE,{"derivedFrom":subQ5}),-1.0]])]});}
            var Q70;
            {var subQ5=sQuery(id+"F0.wireOp",EDGE,"E851.MirrorCS");Q70=makeQuery(id+"F0.imprint","IMPRINT",FACE,{"disambiguationData":[TD([[makeQuery(id+"F0.imprint","IMPRINT",EDGE,{"derivedFrom":subQ5}),-1.0]])]});}
            var Q71;
            {var subQ5=sQuery(id+"F0.wireOp",EDGE,"E1017.MirrorCS");Q71=makeQuery(id+"F0.imprint","IMPRINT",FACE,{"disambiguationData":[TD([[makeQuery(id+"F0.imprint","IMPRINT",EDGE,{"derivedFrom":subQ5}),-1.0]])]});}
            extrude(context, id + "F1", {"entities" : qUnion([Q0, Q1, Q2, Q3, Q4, Q5, Q6, Q7, Q8, Q9, Q10, Q11, Q12, Q13, Q14, Q15, Q16, Q17, Q18, Q19, Q20, Q21, Q22, Q23, Q24, Q25, Q26, Q27, Q28, Q29, Q30, Q31, Q32, Q33, Q34, Q35, Q36, Q37, Q38, Q39, Q40, Q41, Q42, Q43, Q44, Q45, Q46, Q47, Q48, Q49, Q50, Q51, Q52, Q53, Q54, Q55, Q56, Q57, Q58, Q59, Q60, Q61, Q62, Q63, Q64, Q65, Q66, Q67, Q68, Q69, Q70, Q71]), "depth" : 6.35 * mm});
        }
        {
            var Q0;
            Q0=makeQuery(id+"F0.imprint","IMPRINT",FACE,{"disambiguationData":[TD([[makeQuery(id+"F0.imprint","IMPRINT",EDGE,{"derivedFrom":sQuery(id+"F0.wireOp",EDGE,"E2")}),-1.0]])]});
            var Q1;
            {var subQ6=sQuery(id+"F0.wireOp",EDGE,"E13");Q1=makeQuery(id+"F0.imprint","IMPRINT",FACE,{"disambiguationData":[TD([[makeQuery(id+"F0.imprint","IMPRINT",EDGE,{"derivedFrom":subQ6}),1.0]])]});}
            var Q2;
            {var subQ1=sQuery(id+"F0.wireOp",EDGE,"E182");Q2=makeQuery(id+"F0.imprint","IMPRINT",FACE,{"disambiguationData":[TD([[makeQuery(id+"F0.imprint","IMPRINT",EDGE,{"derivedFrom":subQ1}),1.0]])]});}
            var Q3;
            {var subQ0=sQuery(id+"F0.wireOp",EDGE,"E61");Q3=makeQuery(id+"F0.imprint","IMPRINT",FACE,{"disambiguationData":[TD([[makeQuery(id+"F0.imprint","IMPRINT",EDGE,{"derivedFrom":subQ0}),1.0]])]});}
            var Q4;
            Q4=makeQuery(id+"F0.imprint","IMPRINT",FACE,{"disambiguationData":[TD([[makeQuery(id+"F0.imprint","IMPRINT",EDGE,{"derivedFrom":sQuery(id+"F0.wireOp",EDGE,"E390.MirrorCS")}),-1.0]])]});
            var Q5;
            Q5=makeQuery(id+"F0.imprint","IMPRINT",FACE,{"disambiguationData":[TD([[makeQuery(id+"F0.imprint","IMPRINT",EDGE,{"derivedFrom":sQuery(id+"F0.wireOp",EDGE,"E513.MirrorCS")}),-1.0]])]});
            var Q6;
            {var subQ1=sQuery(id+"F0.wireOp",EDGE,"E150");Q6=makeQuery(id+"F0.imprint","IMPRINT",FACE,{"disambiguationData":[TD([[makeQuery(id+"F0.imprint","IMPRINT",EDGE,{"derivedFrom":subQ1}),1.0]])]});}
            var Q7;
            Q7=makeQuery(id+"F0.imprint","IMPRINT",FACE,{"disambiguationData":[TD([[makeQuery(id+"F0.imprint","IMPRINT",EDGE,{"derivedFrom":sQuery(id+"F0.wireOp",EDGE,"E329.MirrorCS")}),-1.0]])]});
            var Q8;
            {var subQ6=sQuery(id+"F0.wireOp",EDGE,"E109");Q8=makeQuery(id+"F0.imprint","IMPRINT",FACE,{"disambiguationData":[TD([[makeQuery(id+"F0.imprint","IMPRINT",EDGE,{"derivedFrom":subQ6}),1.0]])]});}
            var Q9;
            {var subQ5=sQuery(id+"F0.wireOp",EDGE,"E333.MirrorCS");Q9=makeQuery(id+"F0.imprint","IMPRINT",FACE,{"disambiguationData":[TD([[makeQuery(id+"F0.imprint","IMPRINT",EDGE,{"derivedFrom":subQ5}),-1.0]])]});}
            var Q10;
            {var subQ5=sQuery(id+"F0.wireOp",EDGE,"E44");Q10=makeQuery(id+"F0.imprint","IMPRINT",FACE,{"disambiguationData":[TD([[makeQuery(id+"F0.imprint","IMPRINT",EDGE,{"derivedFrom":subQ5}),1.0]])]});}
            var Q11;
            {var subQ0=sQuery(id+"F0.wireOp",EDGE,"E238");Q11=makeQuery(id+"F0.imprint","IMPRINT",FACE,{"disambiguationData":[TD([[makeQuery(id+"F0.imprint","IMPRINT",EDGE,{"derivedFrom":subQ0}),1.0]])]});}
            var Q12;
            Q12=makeQuery(id+"F0.imprint","IMPRINT",FACE,{"disambiguationData":[TD([[makeQuery(id+"F0.imprint","IMPRINT",EDGE,{"derivedFrom":sQuery(id+"F0.wireOp",EDGE,"E296.MirrorCS")}),-1.0]])]});
            var Q13;
            Q13=makeQuery(id+"F0.imprint","IMPRINT",FACE,{"disambiguationData":[TD([[makeQuery(id+"F0.imprint","IMPRINT",EDGE,{"derivedFrom":sQuery(id+"F0.wireOp",EDGE,"E386.MirrorCS")}),-1.0]])]});
            var Q14;
            {var subQ1=sQuery(id+"F0.wireOp",EDGE,"E37");Q14=makeQuery(id+"F0.imprint","IMPRINT",FACE,{"disambiguationData":[TD([[makeQuery(id+"F0.imprint","IMPRINT",EDGE,{"derivedFrom":subQ1}),1.0]])]});}
            var Q15;
            {var subQ1=sQuery(id+"F0.wireOp",EDGE,"E222");Q15=makeQuery(id+"F0.imprint","IMPRINT",FACE,{"disambiguationData":[TD([[makeQuery(id+"F0.imprint","IMPRINT",EDGE,{"derivedFrom":subQ1}),1.0]])]});}
            var Q16;
            {var subQ0=sQuery(id+"F0.wireOp",EDGE,"E397.MirrorCS");Q16=makeQuery(id+"F0.imprint","IMPRINT",FACE,{"disambiguationData":[TD([[makeQuery(id+"F0.imprint","IMPRINT",EDGE,{"derivedFrom":subQ0}),-1.0]])]});}
            var Q17;
            Q17=makeQuery(id+"F0.imprint","IMPRINT",FACE,{"disambiguationData":[TD([[makeQuery(id+"F0.imprint","IMPRINT",EDGE,{"derivedFrom":sQuery(id+"F0.wireOp",EDGE,"E406.MirrorCS")}),-1.0]])]});
            var Q18;
            Q18=makeQuery(id+"F0.imprint","IMPRINT",FACE,{"disambiguationData":[TD([[makeQuery(id+"F0.imprint","IMPRINT",EDGE,{"derivedFrom":sQuery(id+"F0.wireOp",EDGE,"E387.MirrorCS")}),-1.0]])]});
            var Q19;
            {var subQ1=sQuery(id+"F0.wireOp",EDGE,"E190");Q19=makeQuery(id+"F0.imprint","IMPRINT",FACE,{"disambiguationData":[TD([[makeQuery(id+"F0.imprint","IMPRINT",EDGE,{"derivedFrom":subQ1}),1.0]])]});}
            var Q20;
            {var subQ0=sQuery(id+"F0.wireOp",EDGE,"E101");Q20=makeQuery(id+"F0.imprint","IMPRINT",FACE,{"disambiguationData":[TD([[makeQuery(id+"F0.imprint","IMPRINT",EDGE,{"derivedFrom":subQ0}),1.0]])]});}
            var Q21;
            {var subQ1=sQuery(id+"F0.wireOp",EDGE,"E5");Q21=makeQuery(id+"F0.imprint","IMPRINT",FACE,{"disambiguationData":[TD([[makeQuery(id+"F0.imprint","IMPRINT",EDGE,{"derivedFrom":subQ1}),1.0]])]});}
            var Q22;
            {var subQ1=sQuery(id+"F0.wireOp",EDGE,"E45");Q22=makeQuery(id+"F0.imprint","IMPRINT",FACE,{"disambiguationData":[TD([[makeQuery(id+"F0.imprint","IMPRINT",EDGE,{"derivedFrom":subQ1}),1.0]])]});}
            var Q23;
            {var subQ5=sQuery(id+"F0.wireOp",EDGE,"E149");Q23=makeQuery(id+"F0.imprint","IMPRINT",FACE,{"disambiguationData":[TD([[makeQuery(id+"F0.imprint","IMPRINT",EDGE,{"derivedFrom":subQ5}),1.0]])]});}
            var Q24;
            {var subQ1=sQuery(id+"F0.wireOp",EDGE,"E166");Q24=makeQuery(id+"F0.imprint","IMPRINT",FACE,{"disambiguationData":[TD([[makeQuery(id+"F0.imprint","IMPRINT",EDGE,{"derivedFrom":subQ1}),1.0]])]});}
            var Q25;
            {var subQ1=sQuery(id+"F0.wireOp",EDGE,"E246");Q25=makeQuery(id+"F0.imprint","IMPRINT",FACE,{"disambiguationData":[TD([[makeQuery(id+"F0.imprint","IMPRINT",EDGE,{"derivedFrom":subQ1}),1.0]])]});}
            var Q26;
            Q26=makeQuery(id+"F0.imprint","IMPRINT",FACE,{"disambiguationData":[TD([[makeQuery(id+"F0.imprint","IMPRINT",EDGE,{"derivedFrom":sQuery(id+"F0.wireOp",EDGE,"E388.MirrorCS")}),-1.0]])]});
            var Q27;
            {var subQ0=sQuery(id+"F0.wireOp",EDGE,"E398.MirrorCS");Q27=makeQuery(id+"F0.imprint","IMPRINT",FACE,{"disambiguationData":[TD([[makeQuery(id+"F0.imprint","IMPRINT",EDGE,{"derivedFrom":subQ0}),-1.0]])]});}
            var Q28;
            {var subQ5=sQuery(id+"F0.wireOp",EDGE,"E108");Q28=makeQuery(id+"F0.imprint","IMPRINT",FACE,{"disambiguationData":[TD([[makeQuery(id+"F0.imprint","IMPRINT",EDGE,{"derivedFrom":subQ5}),1.0]])]});}
            var Q29;
            Q29=makeQuery(id+"F0.imprint","IMPRINT",FACE,{"disambiguationData":[TD([[makeQuery(id+"F0.imprint","IMPRINT",EDGE,{"derivedFrom":sQuery(id+"F0.wireOp",EDGE,"E389.MirrorCS")}),-1.0]])]});
            var Q30;
            {var subQ5=sQuery(id+"F0.wireOp",EDGE,"E337.MirrorCS");Q30=makeQuery(id+"F0.imprint","IMPRINT",FACE,{"disambiguationData":[TD([[makeQuery(id+"F0.imprint","IMPRINT",EDGE,{"derivedFrom":subQ5}),-1.0]])]});}
            var Q31;
            {var subQ1=sQuery(id+"F0.wireOp",EDGE,"E77");Q31=makeQuery(id+"F0.imprint","IMPRINT",FACE,{"disambiguationData":[TD([[makeQuery(id+"F0.imprint","IMPRINT",EDGE,{"derivedFrom":subQ1}),1.0]])]});}
            var Q32;
            {var subQ5=sQuery(id+"F0.wireOp",EDGE,"E457.MirrorCS");Q32=makeQuery(id+"F0.imprint","IMPRINT",FACE,{"disambiguationData":[TD([[makeQuery(id+"F0.imprint","IMPRINT",EDGE,{"derivedFrom":subQ5}),-1.0]])]});}
            var Q33;
            Q33=makeQuery(id+"F0.imprint","IMPRINT",FACE,{"disambiguationData":[TD([[makeQuery(id+"F0.imprint","IMPRINT",EDGE,{"derivedFrom":sQuery(id+"F0.wireOp",EDGE,"E514.MirrorCS")}),-1.0]])]});
            var Q34;
            {var subQ1=sQuery(id+"F0.wireOp",EDGE,"E85");Q34=makeQuery(id+"F0.imprint","IMPRINT",FACE,{"disambiguationData":[TD([[makeQuery(id+"F0.imprint","IMPRINT",EDGE,{"derivedFrom":subQ1}),1.0]])]});}
            var Q35;
            Q35=makeQuery(id+"F0.imprint","IMPRINT",FACE,{"disambiguationData":[TD([[makeQuery(id+"F0.imprint","IMPRINT",EDGE,{"derivedFrom":sQuery(id+"F0.wireOp",EDGE,"E323.MirrorCS")}),-1.0]])]});
            var Q36;
            {var subQ5=sQuery(id+"F0.wireOp",EDGE,"E448.MirrorCS");Q36=makeQuery(id+"F0.imprint","IMPRINT",FACE,{"disambiguationData":[TD([[makeQuery(id+"F0.imprint","IMPRINT",EDGE,{"derivedFrom":subQ5}),-1.0]])]});}
            var Q37;
            Q37=makeQuery(id+"F0.imprint","IMPRINT",FACE,{"disambiguationData":[TD([[makeQuery(id+"F0.imprint","IMPRINT",EDGE,{"derivedFrom":sQuery(id+"F0.wireOp",EDGE,"E299.MirrorCS")}),-1.0]])]});
            var Q38;
            {var subQ5=sQuery(id+"F0.wireOp",EDGE,"E356.MirrorCS");Q38=makeQuery(id+"F0.imprint","IMPRINT",FACE,{"disambiguationData":[TD([[makeQuery(id+"F0.imprint","IMPRINT",EDGE,{"derivedFrom":subQ5}),-1.0]])]});}
            var Q39;
            Q39=makeQuery(id+"F0.imprint","IMPRINT",FACE,{"disambiguationData":[TD([[makeQuery(id+"F0.imprint","IMPRINT",EDGE,{"derivedFrom":sQuery(id+"F0.wireOp",EDGE,"E511.MirrorCS")}),-1.0]])]});
            var Q40;
            Q40=makeQuery(id+"F0.imprint","IMPRINT",FACE,{"disambiguationData":[TD([[makeQuery(id+"F0.imprint","IMPRINT",EDGE,{"derivedFrom":sQuery(id+"F0.wireOp",EDGE,"E330.MirrorCS")}),-1.0]])]});
            var Q41;
            Q41=makeQuery(id+"F0.imprint","IMPRINT",FACE,{"disambiguationData":[TD([[makeQuery(id+"F0.imprint","IMPRINT",EDGE,{"derivedFrom":sQuery(id+"F0.wireOp",EDGE,"E512.MirrorCS")}),-1.0]])]});
            var Q42;
            Q42=makeQuery(id+"F0.imprint","IMPRINT",FACE,{"disambiguationData":[TD([[makeQuery(id+"F0.imprint","IMPRINT",EDGE,{"derivedFrom":sQuery(id+"F0.wireOp",EDGE,"E403.MirrorCS")}),-1.0]])]});
            var Q43;
            Q43=makeQuery(id+"F0.imprint","IMPRINT",FACE,{"disambiguationData":[TD([[makeQuery(id+"F0.imprint","IMPRINT",EDGE,{"derivedFrom":sQuery(id+"F0.wireOp",EDGE,"E300.MirrorCS")}),-1.0]])]});
            var Q44;
            {var subQ5=sQuery(id+"F0.wireOp",EDGE,"E354.MirrorCS");Q44=makeQuery(id+"F0.imprint","IMPRINT",FACE,{"disambiguationData":[TD([[makeQuery(id+"F0.imprint","IMPRINT",EDGE,{"derivedFrom":subQ5}),-1.0]])]});}
            var Q45;
            {var subQ5=sQuery(id+"F0.wireOp",EDGE,"E12");Q45=makeQuery(id+"F0.imprint","IMPRINT",FACE,{"disambiguationData":[TD([[makeQuery(id+"F0.imprint","IMPRINT",EDGE,{"derivedFrom":subQ5}),1.0]])]});}
            var Q46;
            {var subQ5=sQuery(id+"F0.wireOp",EDGE,"E352.MirrorCS");Q46=makeQuery(id+"F0.imprint","IMPRINT",FACE,{"disambiguationData":[TD([[makeQuery(id+"F0.imprint","IMPRINT",EDGE,{"derivedFrom":subQ5}),-1.0]])]});}
            var Q47;
            {var subQ5=sQuery(id+"F0.wireOp",EDGE,"E436.MirrorCS");Q47=makeQuery(id+"F0.imprint","IMPRINT",FACE,{"disambiguationData":[TD([[makeQuery(id+"F0.imprint","IMPRINT",EDGE,{"derivedFrom":subQ5}),-1.0]])]});}
            var Q48;
            {var subQ5=sQuery(id+"F0.wireOp",EDGE,"E353.MirrorCS");Q48=makeQuery(id+"F0.imprint","IMPRINT",FACE,{"disambiguationData":[TD([[makeQuery(id+"F0.imprint","IMPRINT",EDGE,{"derivedFrom":subQ5}),-1.0]])]});}
            var Q49;
            Q49=makeQuery(id+"F0.imprint","IMPRINT",FACE,{"disambiguationData":[TD([[makeQuery(id+"F0.imprint","IMPRINT",EDGE,{"derivedFrom":sQuery(id+"F0.wireOp",EDGE,"E328.MirrorCS")}),-1.0]])]});
            var Q50;
            {var subQ5=sQuery(id+"F0.wireOp",EDGE,"E447.MirrorCS");Q50=makeQuery(id+"F0.imprint","IMPRINT",FACE,{"disambiguationData":[TD([[makeQuery(id+"F0.imprint","IMPRINT",EDGE,{"derivedFrom":subQ5}),-1.0]])]});}
            var Q51;
            {var subQ5=sQuery(id+"F0.wireOp",EDGE,"E500.MirrorCS");Q51=makeQuery(id+"F0.imprint","IMPRINT",FACE,{"disambiguationData":[TD([[makeQuery(id+"F0.imprint","IMPRINT",EDGE,{"derivedFrom":subQ5}),-1.0]])]});}
            var Q52;
            Q52=makeQuery(id+"F0.imprint","IMPRINT",FACE,{"disambiguationData":[TD([[makeQuery(id+"F0.imprint","IMPRINT",EDGE,{"derivedFrom":sQuery(id+"F0.wireOp",EDGE,"E293.MirrorCS")}),-1.0]])]});
            var Q53;
            {var subQ5=sQuery(id+"F0.wireOp",EDGE,"E540.MirrorCS");Q53=makeQuery(id+"F0.imprint","IMPRINT",FACE,{"disambiguationData":[TD([[makeQuery(id+"F0.imprint","IMPRINT",EDGE,{"derivedFrom":subQ5}),-1.0]])]});}
            var Q54;
            {var subQ1=sQuery(id+"F0.wireOp",EDGE,"E133");Q54=makeQuery(id+"F0.imprint","IMPRINT",FACE,{"disambiguationData":[TD([[makeQuery(id+"F0.imprint","IMPRINT",EDGE,{"derivedFrom":subQ1}),1.0]])]});}
            var Q55;
            {var subQ1=sQuery(id+"F0.wireOp",EDGE,"E230");Q55=makeQuery(id+"F0.imprint","IMPRINT",FACE,{"disambiguationData":[TD([[makeQuery(id+"F0.imprint","IMPRINT",EDGE,{"derivedFrom":subQ1}),1.0]])]});}
            var Q56;
            {var subQ4=sQuery(id+"F0.wireOp",EDGE,"E400.MirrorCS");Q56=makeQuery(id+"F0.imprint","IMPRINT",FACE,{"disambiguationData":[TD([[makeQuery(id+"F0.imprint","IMPRINT",EDGE,{"derivedFrom":subQ4}),-1.0]])]});}
            var Q57;
            {var subQ5=sQuery(id+"F0.wireOp",EDGE,"E21");Q57=makeQuery(id+"F0.imprint","IMPRINT",FACE,{"disambiguationData":[TD([[makeQuery(id+"F0.imprint","IMPRINT",EDGE,{"derivedFrom":subQ5}),1.0]])]});}
            var Q58;
            Q58=makeQuery(id+"F0.imprint","IMPRINT",FACE,{"disambiguationData":[TD([[makeQuery(id+"F0.imprint","IMPRINT",EDGE,{"derivedFrom":sQuery(id+"F0.wireOp",EDGE,"E325.MirrorCS")}),-1.0]])]});
            var Q59;
            {var subQ1=sQuery(id+"F0.wireOp",EDGE,"E270");Q59=makeQuery(id+"F0.imprint","IMPRINT",FACE,{"disambiguationData":[TD([[makeQuery(id+"F0.imprint","IMPRINT",EDGE,{"derivedFrom":subQ1}),1.0]])]});}
            var Q60;
            {var subQ5=sQuery(id+"F0.wireOp",EDGE,"E181");Q60=makeQuery(id+"F0.imprint","IMPRINT",FACE,{"disambiguationData":[TD([[makeQuery(id+"F0.imprint","IMPRINT",EDGE,{"derivedFrom":subQ5}),1.0]])]});}
            var Q61;
            Q61=makeQuery(id+"F0.imprint","IMPRINT",FACE,{"disambiguationData":[TD([[makeQuery(id+"F0.imprint","IMPRINT",EDGE,{"derivedFrom":sQuery(id+"F0.wireOp",EDGE,"E285.MirrorCS")}),-1.0]])]});
            var Q62;
            {var subQ1=sQuery(id+"F0.wireOp",EDGE,"E117");Q62=makeQuery(id+"F0.imprint","IMPRINT",FACE,{"disambiguationData":[TD([[makeQuery(id+"F0.imprint","IMPRINT",EDGE,{"derivedFrom":subQ1}),1.0]])]});}
            var Q63;
            {var subQ5=sQuery(id+"F0.wireOp",EDGE,"E237");Q63=makeQuery(id+"F0.imprint","IMPRINT",FACE,{"disambiguationData":[TD([[makeQuery(id+"F0.imprint","IMPRINT",EDGE,{"derivedFrom":subQ5}),1.0]])]});}
            var Q64;
            Q64=makeQuery(id+"F0.imprint","IMPRINT",FACE,{"disambiguationData":[TD([[makeQuery(id+"F0.imprint","IMPRINT",EDGE,{"derivedFrom":sQuery(id+"F0.wireOp",EDGE,"E312.MirrorCS")}),-1.0]])]});
            var Q65;
            Q65=makeQuery(id+"F0.imprint","IMPRINT",FACE,{"disambiguationData":[TD([[makeQuery(id+"F0.imprint","IMPRINT",EDGE,{"derivedFrom":sQuery(id+"F0.wireOp",EDGE,"E418.MirrorCS")}),-1.0]])]});
            var Q66;
            {var subQ5=sQuery(id+"F0.wireOp",EDGE,"E100");Q66=makeQuery(id+"F0.imprint","IMPRINT",FACE,{"disambiguationData":[TD([[makeQuery(id+"F0.imprint","IMPRINT",EDGE,{"derivedFrom":subQ5}),1.0]])]});}
            var Q67;
            {var subQ5=sQuery(id+"F0.wireOp",EDGE,"E60");Q67=makeQuery(id+"F0.imprint","IMPRINT",FACE,{"disambiguationData":[TD([[makeQuery(id+"F0.imprint","IMPRINT",EDGE,{"derivedFrom":subQ5}),1.0]])]});}
            var Q68;
            {var subQ1=sQuery(id+"F0.wireOp",EDGE,"E174");Q68=makeQuery(id+"F0.imprint","IMPRINT",FACE,{"disambiguationData":[TD([[makeQuery(id+"F0.imprint","IMPRINT",EDGE,{"derivedFrom":subQ1}),1.0]])]});}
            var Q69;
            {var subQ1=sQuery(id+"F0.wireOp",EDGE,"E69");Q69=makeQuery(id+"F0.imprint","IMPRINT",FACE,{"disambiguationData":[TD([[makeQuery(id+"F0.imprint","IMPRINT",EDGE,{"derivedFrom":subQ1}),1.0]])]});}
            var Q70;
            {var subQ6=sQuery(id+"F0.wireOp",EDGE,"E262");Q70=makeQuery(id+"F0.imprint","IMPRINT",FACE,{"disambiguationData":[TD([[makeQuery(id+"F0.imprint","IMPRINT",EDGE,{"derivedFrom":subQ6}),1.0]])]});}
            var Q71;
            {var subQ5=sQuery(id+"F0.wireOp",EDGE,"E36");Q71=makeQuery(id+"F0.imprint","IMPRINT",FACE,{"disambiguationData":[TD([[makeQuery(id+"F0.imprint","IMPRINT",EDGE,{"derivedFrom":subQ5}),1.0]])]});}
            var Q72;
            {var subQ1=sQuery(id+"F0.wireOp",EDGE,"E214");Q72=makeQuery(id+"F0.imprint","IMPRINT",FACE,{"disambiguationData":[TD([[makeQuery(id+"F0.imprint","IMPRINT",EDGE,{"derivedFrom":subQ1}),1.0]])]});}
            var Q73;
            {var subQ5=sQuery(id+"F0.wireOp",EDGE,"E221");Q73=makeQuery(id+"F0.imprint","IMPRINT",FACE,{"disambiguationData":[TD([[makeQuery(id+"F0.imprint","IMPRINT",EDGE,{"derivedFrom":subQ5}),1.0]])]});}
            var Q74;
            {var subQ5=sQuery(id+"F0.wireOp",EDGE,"E189");Q74=makeQuery(id+"F0.imprint","IMPRINT",FACE,{"disambiguationData":[TD([[makeQuery(id+"F0.imprint","IMPRINT",EDGE,{"derivedFrom":subQ5}),1.0]])]});}
            var Q75;
            {var subQ0=sQuery(id+"F0.wireOp",EDGE,"E158");Q75=makeQuery(id+"F0.imprint","IMPRINT",FACE,{"disambiguationData":[TD([[makeQuery(id+"F0.imprint","IMPRINT",EDGE,{"derivedFrom":subQ0}),1.0]])]});}
            var Q76;
            Q76=makeQuery(id+"F0.imprint","IMPRINT",FACE,{"disambiguationData":[TD([[makeQuery(id+"F0.imprint","IMPRINT",EDGE,{"derivedFrom":sQuery(id+"F0.wireOp",EDGE,"E142")}),1.0]])]});
            var Q77;
            {var subQ5=sQuery(id+"F0.wireOp",EDGE,"E443.MirrorCS");Q77=makeQuery(id+"F0.imprint","IMPRINT",FACE,{"disambiguationData":[TD([[makeQuery(id+"F0.imprint","IMPRINT",EDGE,{"derivedFrom":subQ5}),-1.0]])]});}
            var Q78;
            {var subQ5=sQuery(id+"F0.wireOp",EDGE,"E350.MirrorCS");Q78=makeQuery(id+"F0.imprint","IMPRINT",FACE,{"disambiguationData":[TD([[makeQuery(id+"F0.imprint","IMPRINT",EDGE,{"derivedFrom":subQ5}),-1.0]])]});}
            var Q79;
            {var subQ5=sQuery(id+"F0.wireOp",EDGE,"E20");Q79=makeQuery(id+"F0.imprint","IMPRINT",FACE,{"disambiguationData":[TD([[makeQuery(id+"F0.imprint","IMPRINT",EDGE,{"derivedFrom":subQ5}),1.0]])]});}
            var Q80;
            {var subQ5=sQuery(id+"F0.wireOp",EDGE,"E351.MirrorCS");Q80=makeQuery(id+"F0.imprint","IMPRINT",FACE,{"disambiguationData":[TD([[makeQuery(id+"F0.imprint","IMPRINT",EDGE,{"derivedFrom":subQ5}),-1.0]])]});}
            var Q81;
            {var subQ1=sQuery(id+"F0.wireOp",EDGE,"E29");Q81=makeQuery(id+"F0.imprint","IMPRINT",FACE,{"disambiguationData":[TD([[makeQuery(id+"F0.imprint","IMPRINT",EDGE,{"derivedFrom":subQ1}),1.0]])]});}
            var Q82;
            {var subQ1=sQuery(id+"F0.wireOp",EDGE,"E53");Q82=makeQuery(id+"F0.imprint","IMPRINT",FACE,{"disambiguationData":[TD([[makeQuery(id+"F0.imprint","IMPRINT",EDGE,{"derivedFrom":subQ1}),1.0]])]});}
            var Q83;
            Q83=makeQuery(id+"F0.imprint","IMPRINT",FACE,{"disambiguationData":[TD([[makeQuery(id+"F0.imprint","IMPRINT",EDGE,{"derivedFrom":sQuery(id+"F0.wireOp",EDGE,"E404.MirrorCS")}),-1.0]])]});
            var Q84;
            {var subQ5=sQuery(id+"F0.wireOp",EDGE,"E506.MirrorCS");Q84=makeQuery(id+"F0.imprint","IMPRINT",FACE,{"disambiguationData":[TD([[makeQuery(id+"F0.imprint","IMPRINT",EDGE,{"derivedFrom":subQ5}),-1.0]])]});}
            var Q85;
            Q85=makeQuery(id+"F0.imprint","IMPRINT",FACE,{"disambiguationData":[TD([[makeQuery(id+"F0.imprint","IMPRINT",EDGE,{"derivedFrom":sQuery(id+"F0.wireOp",EDGE,"E294.MirrorCS")}),-1.0]])]});
            var Q86;
            {var subQ5=sQuery(id+"F0.wireOp",EDGE,"E501.MirrorCS");Q86=makeQuery(id+"F0.imprint","IMPRINT",FACE,{"disambiguationData":[TD([[makeQuery(id+"F0.imprint","IMPRINT",EDGE,{"derivedFrom":subQ5}),-1.0]])]});}
            var Q87;
            Q87=makeQuery(id+"F0.imprint","IMPRINT",FACE,{"disambiguationData":[TD([[makeQuery(id+"F0.imprint","IMPRINT",EDGE,{"derivedFrom":sQuery(id+"F0.wireOp",EDGE,"E383.MirrorCS")}),-1.0]])]});
            var Q88;
            {var subQ1=sQuery(id+"F0.wireOp",EDGE,"E254");Q88=makeQuery(id+"F0.imprint","IMPRINT",FACE,{"disambiguationData":[TD([[makeQuery(id+"F0.imprint","IMPRINT",EDGE,{"derivedFrom":subQ1}),1.0]])]});}
            var Q89;
            {var subQ0=sQuery(id+"F0.wireOp",EDGE,"E141");var subQ1=sQuery(id+"F0.wireOp",EDGE,"E0");var subQ2=makeQuery(id+"F0.imprint","INTERSECT",VERTEX,{"derivedFrom":[subQ1,subQ0]});Q89=makeQuery(id+"F0.imprint","IMPRINT",FACE,{"disambiguationData":[TD([[makeQuery(id+"F0.imprint","IMPRINT",EDGE,{"disambiguationData":[TD([[subQ2,-1.0]])],"derivedFrom":subQ1}),1.0]])]});}
            var Q90;
            {var subQ5=sQuery(id+"F0.wireOp",EDGE,"E165");Q90=makeQuery(id+"F0.imprint","IMPRINT",FACE,{"disambiguationData":[TD([[makeQuery(id+"F0.imprint","IMPRINT",EDGE,{"derivedFrom":subQ5}),1.0]])]});}
            var Q91;
            {var subQ5=sQuery(id+"F0.wireOp",EDGE,"E173");Q91=makeQuery(id+"F0.imprint","IMPRINT",FACE,{"disambiguationData":[TD([[makeQuery(id+"F0.imprint","IMPRINT",EDGE,{"derivedFrom":subQ5}),1.0]])]});}
            var Q92;
            {var subQ6=sQuery(id+"F0.wireOp",EDGE,"E206");Q92=makeQuery(id+"F0.imprint","IMPRINT",FACE,{"disambiguationData":[TD([[makeQuery(id+"F0.imprint","IMPRINT",EDGE,{"derivedFrom":subQ6}),1.0]])]});}
            var Q93;
            {var subQ5=sQuery(id+"F0.wireOp",EDGE,"E261");Q93=makeQuery(id+"F0.imprint","IMPRINT",FACE,{"disambiguationData":[TD([[makeQuery(id+"F0.imprint","IMPRINT",EDGE,{"derivedFrom":subQ5}),1.0]])]});}
            var Q94;
            {var subQ5=sQuery(id+"F0.wireOp",EDGE,"E347.MirrorCS");Q94=makeQuery(id+"F0.imprint","IMPRINT",FACE,{"disambiguationData":[TD([[makeQuery(id+"F0.imprint","IMPRINT",EDGE,{"derivedFrom":subQ5}),-1.0]])]});}
            var Q95;
            {var subQ0=sQuery(id+"F0.wireOp",EDGE,"E401.MirrorCS");Q95=makeQuery(id+"F0.imprint","IMPRINT",FACE,{"disambiguationData":[TD([[makeQuery(id+"F0.imprint","IMPRINT",EDGE,{"derivedFrom":subQ0}),-1.0]])]});}
            var Q96;
            {var subQ5=sQuery(id+"F0.wireOp",EDGE,"E157");Q96=makeQuery(id+"F0.imprint","IMPRINT",FACE,{"disambiguationData":[TD([[makeQuery(id+"F0.imprint","IMPRINT",EDGE,{"derivedFrom":subQ5}),1.0]])]});}
            var Q97;
            {var subQ5=sQuery(id+"F0.wireOp",EDGE,"E355.MirrorCS");Q97=makeQuery(id+"F0.imprint","IMPRINT",FACE,{"disambiguationData":[TD([[makeQuery(id+"F0.imprint","IMPRINT",EDGE,{"derivedFrom":subQ5}),-1.0]])]});}
            var Q98;
            Q98=makeQuery(id+"F0.imprint","IMPRINT",FACE,{"disambiguationData":[TD([[makeQuery(id+"F0.imprint","IMPRINT",EDGE,{"derivedFrom":sQuery(id+"F0.wireOp",EDGE,"E326.MirrorCS")}),-1.0]])]});
            var Q99;
            {var subQ1=sQuery(id+"F0.wireOp",EDGE,"E93");Q99=makeQuery(id+"F0.imprint","IMPRINT",FACE,{"disambiguationData":[TD([[makeQuery(id+"F0.imprint","IMPRINT",EDGE,{"derivedFrom":subQ1}),1.0]])]});}
            var Q100;
            {var subQ1=sQuery(id+"F0.wireOp",EDGE,"E125");Q100=makeQuery(id+"F0.imprint","IMPRINT",FACE,{"disambiguationData":[TD([[makeQuery(id+"F0.imprint","IMPRINT",EDGE,{"derivedFrom":subQ1}),1.0]])]});}
            var Q101;
            {var subQ5=sQuery(id+"F0.wireOp",EDGE,"E349.MirrorCS");Q101=makeQuery(id+"F0.imprint","IMPRINT",FACE,{"disambiguationData":[TD([[makeQuery(id+"F0.imprint","IMPRINT",EDGE,{"derivedFrom":subQ5}),-1.0]])]});}
            var Q102;
            Q102=makeQuery(id+"F0.imprint","IMPRINT",FACE,{"disambiguationData":[TD([[makeQuery(id+"F0.imprint","IMPRINT",EDGE,{"derivedFrom":sQuery(id+"F0.wireOp",EDGE,"E298.MirrorCS")}),-1.0]])]});
            var Q103;
            {var subQ5=sQuery(id+"F0.wireOp",EDGE,"E456.MirrorCS");Q103=makeQuery(id+"F0.imprint","IMPRINT",FACE,{"disambiguationData":[TD([[makeQuery(id+"F0.imprint","IMPRINT",EDGE,{"derivedFrom":subQ5}),-1.0]])]});}
            var Q104;
            {var subQ5=sQuery(id+"F0.wireOp",EDGE,"E445.MirrorCS");Q104=makeQuery(id+"F0.imprint","IMPRINT",FACE,{"disambiguationData":[TD([[makeQuery(id+"F0.imprint","IMPRINT",EDGE,{"derivedFrom":subQ5}),-1.0]])]});}
            var Q105;
            {var subQ5=sQuery(id+"F0.wireOp",EDGE,"E446.MirrorCS");Q105=makeQuery(id+"F0.imprint","IMPRINT",FACE,{"disambiguationData":[TD([[makeQuery(id+"F0.imprint","IMPRINT",EDGE,{"derivedFrom":subQ5}),-1.0]])]});}
            var Q106;
            {var subQ5=sQuery(id+"F0.wireOp",EDGE,"E84");Q106=makeQuery(id+"F0.imprint","IMPRINT",FACE,{"disambiguationData":[TD([[makeQuery(id+"F0.imprint","IMPRINT",EDGE,{"derivedFrom":subQ5}),1.0]])]});}
            var Q107;
            {var subQ5=sQuery(id+"F0.wireOp",EDGE,"E132");Q107=makeQuery(id+"F0.imprint","IMPRINT",FACE,{"disambiguationData":[TD([[makeQuery(id+"F0.imprint","IMPRINT",EDGE,{"derivedFrom":subQ5}),1.0]])]});}
            var Q108;
            {var subQ5=sQuery(id+"F0.wireOp",EDGE,"E438.MirrorCS");Q108=makeQuery(id+"F0.imprint","IMPRINT",FACE,{"disambiguationData":[TD([[makeQuery(id+"F0.imprint","IMPRINT",EDGE,{"derivedFrom":subQ5}),-1.0]])]});}
            var Q109;
            {var subQ5=sQuery(id+"F0.wireOp",EDGE,"E269");Q109=makeQuery(id+"F0.imprint","IMPRINT",FACE,{"disambiguationData":[TD([[makeQuery(id+"F0.imprint","IMPRINT",EDGE,{"derivedFrom":subQ5}),1.0]])]});}
            var Q110;
            Q110=makeQuery(id+"F0.imprint","IMPRINT",FACE,{"disambiguationData":[TD([[makeQuery(id+"F0.imprint","IMPRINT",EDGE,{"derivedFrom":sQuery(id+"F0.wireOp",EDGE,"E286.MirrorCS")}),-1.0]])]});
            var Q111;
            Q111=makeQuery(id+"F0.imprint","IMPRINT",FACE,{"disambiguationData":[TD([[makeQuery(id+"F0.imprint","IMPRINT",EDGE,{"derivedFrom":sQuery(id+"F0.wireOp",EDGE,"E297.MirrorCS")}),-1.0]])]});
            var Q112;
            {var subQ5=sQuery(id+"F0.wireOp",EDGE,"E345.MirrorCS");Q112=makeQuery(id+"F0.imprint","IMPRINT",FACE,{"disambiguationData":[TD([[makeQuery(id+"F0.imprint","IMPRINT",EDGE,{"derivedFrom":subQ5}),-1.0]])]});}
            var Q113;
            {var subQ5=sQuery(id+"F0.wireOp",EDGE,"E441.MirrorCS");Q113=makeQuery(id+"F0.imprint","IMPRINT",FACE,{"disambiguationData":[TD([[makeQuery(id+"F0.imprint","IMPRINT",EDGE,{"derivedFrom":subQ5}),-1.0]])]});}
            var Q114;
            Q114=makeQuery(id+"F0.imprint","IMPRINT",FACE,{"disambiguationData":[TD([[makeQuery(id+"F0.imprint","IMPRINT",EDGE,{"derivedFrom":sQuery(id+"F0.wireOp",EDGE,"E510.MirrorCS")}),-1.0]])]});
            var Q115;
            {var subQ5=sQuery(id+"F0.wireOp",EDGE,"E116");Q115=makeQuery(id+"F0.imprint","IMPRINT",FACE,{"disambiguationData":[TD([[makeQuery(id+"F0.imprint","IMPRINT",EDGE,{"derivedFrom":subQ5}),1.0]])]});}
            var Q116;
            {var subQ5=sQuery(id+"F0.wireOp",EDGE,"E503.MirrorCS");Q116=makeQuery(id+"F0.imprint","IMPRINT",FACE,{"disambiguationData":[TD([[makeQuery(id+"F0.imprint","IMPRINT",EDGE,{"derivedFrom":subQ5}),-1.0]])]});}
            var Q117;
            {var subQ5=sQuery(id+"F0.wireOp",EDGE,"E213");Q117=makeQuery(id+"F0.imprint","IMPRINT",FACE,{"disambiguationData":[TD([[makeQuery(id+"F0.imprint","IMPRINT",EDGE,{"derivedFrom":subQ5}),1.0]])]});}
            var Q118;
            {var subQ5=sQuery(id+"F0.wireOp",EDGE,"E92");Q118=makeQuery(id+"F0.imprint","IMPRINT",FACE,{"disambiguationData":[TD([[makeQuery(id+"F0.imprint","IMPRINT",EDGE,{"derivedFrom":subQ5}),1.0]])]});}
            var Q119;
            {var subQ5=sQuery(id+"F0.wireOp",EDGE,"E52");Q119=makeQuery(id+"F0.imprint","IMPRINT",FACE,{"disambiguationData":[TD([[makeQuery(id+"F0.imprint","IMPRINT",EDGE,{"derivedFrom":subQ5}),1.0]])]});}
            var Q120;
            {var subQ5=sQuery(id+"F0.wireOp",EDGE,"E348.MirrorCS");Q120=makeQuery(id+"F0.imprint","IMPRINT",FACE,{"disambiguationData":[TD([[makeQuery(id+"F0.imprint","IMPRINT",EDGE,{"derivedFrom":subQ5}),-1.0]])]});}
            var Q121;
            {var subQ5=sQuery(id+"F0.wireOp",EDGE,"E68");Q121=makeQuery(id+"F0.imprint","IMPRINT",FACE,{"disambiguationData":[TD([[makeQuery(id+"F0.imprint","IMPRINT",EDGE,{"derivedFrom":subQ5}),1.0]])]});}
            var Q122;
            {var subQ5=sQuery(id+"F0.wireOp",EDGE,"E502.MirrorCS");Q122=makeQuery(id+"F0.imprint","IMPRINT",FACE,{"disambiguationData":[TD([[makeQuery(id+"F0.imprint","IMPRINT",EDGE,{"derivedFrom":subQ5}),-1.0]])]});}
            var Q123;
            {var subQ5=sQuery(id+"F0.wireOp",EDGE,"E505.MirrorCS");Q123=makeQuery(id+"F0.imprint","IMPRINT",FACE,{"disambiguationData":[TD([[makeQuery(id+"F0.imprint","IMPRINT",EDGE,{"derivedFrom":subQ5}),-1.0]])]});}
            var Q124;
            {var subQ5=sQuery(id+"F0.wireOp",EDGE,"E28");Q124=makeQuery(id+"F0.imprint","IMPRINT",FACE,{"disambiguationData":[TD([[makeQuery(id+"F0.imprint","IMPRINT",EDGE,{"derivedFrom":subQ5}),1.0]])]});}
            var Q125;
            {var subQ5=sQuery(id+"F0.wireOp",EDGE,"E205");Q125=makeQuery(id+"F0.imprint","IMPRINT",FACE,{"disambiguationData":[TD([[makeQuery(id+"F0.imprint","IMPRINT",EDGE,{"derivedFrom":subQ5}),1.0]])]});}
            var Q126;
            {var subQ5=sQuery(id+"F0.wireOp",EDGE,"E4");Q126=makeQuery(id+"F0.imprint","IMPRINT",FACE,{"disambiguationData":[TD([[makeQuery(id+"F0.imprint","IMPRINT",EDGE,{"derivedFrom":subQ5}),1.0]])]});}
            var Q127;
            {var subQ5=sQuery(id+"F0.wireOp",EDGE,"E229");Q127=makeQuery(id+"F0.imprint","IMPRINT",FACE,{"disambiguationData":[TD([[makeQuery(id+"F0.imprint","IMPRINT",EDGE,{"derivedFrom":subQ5}),1.0]])]});}
            var Q128;
            {var subQ5=sQuery(id+"F0.wireOp",EDGE,"E245");Q128=makeQuery(id+"F0.imprint","IMPRINT",FACE,{"disambiguationData":[TD([[makeQuery(id+"F0.imprint","IMPRINT",EDGE,{"derivedFrom":subQ5}),1.0]])]});}
            var Q129;
            {var subQ5=sQuery(id+"F0.wireOp",EDGE,"E439.MirrorCS");Q129=makeQuery(id+"F0.imprint","IMPRINT",FACE,{"disambiguationData":[TD([[makeQuery(id+"F0.imprint","IMPRINT",EDGE,{"derivedFrom":subQ5}),-1.0]])]});}
            var Q130;
            {var subQ5=sQuery(id+"F0.wireOp",EDGE,"E541.MirrorCS");Q130=makeQuery(id+"F0.imprint","IMPRINT",FACE,{"disambiguationData":[TD([[makeQuery(id+"F0.imprint","IMPRINT",EDGE,{"derivedFrom":subQ5}),-1.0]])]});}
            var Q131;
            {var subQ5=sQuery(id+"F0.wireOp",EDGE,"E504.MirrorCS");Q131=makeQuery(id+"F0.imprint","IMPRINT",FACE,{"disambiguationData":[TD([[makeQuery(id+"F0.imprint","IMPRINT",EDGE,{"derivedFrom":subQ5}),-1.0]])]});}
            var Q132;
            {var subQ5=sQuery(id+"F0.wireOp",EDGE,"E335.MirrorCS");Q132=makeQuery(id+"F0.imprint","IMPRINT",FACE,{"disambiguationData":[TD([[makeQuery(id+"F0.imprint","IMPRINT",EDGE,{"derivedFrom":subQ5}),-1.0]])]});}
            var Q133;
            {var subQ5=sQuery(id+"F0.wireOp",EDGE,"E76");Q133=makeQuery(id+"F0.imprint","IMPRINT",FACE,{"disambiguationData":[TD([[makeQuery(id+"F0.imprint","IMPRINT",EDGE,{"derivedFrom":subQ5}),1.0]])]});}
            var Q134;
            {var subQ5=sQuery(id+"F0.wireOp",EDGE,"E437.MirrorCS");Q134=makeQuery(id+"F0.imprint","IMPRINT",FACE,{"disambiguationData":[TD([[makeQuery(id+"F0.imprint","IMPRINT",EDGE,{"derivedFrom":subQ5}),-1.0]])]});}
            var Q135;
            {var subQ5=sQuery(id+"F0.wireOp",EDGE,"E124");Q135=makeQuery(id+"F0.imprint","IMPRINT",FACE,{"disambiguationData":[TD([[makeQuery(id+"F0.imprint","IMPRINT",EDGE,{"derivedFrom":subQ5}),1.0]])]});}
            var Q136;
            {var subQ5=sQuery(id+"F0.wireOp",EDGE,"E253");Q136=makeQuery(id+"F0.imprint","IMPRINT",FACE,{"disambiguationData":[TD([[makeQuery(id+"F0.imprint","IMPRINT",EDGE,{"derivedFrom":subQ5}),1.0]])]});}
            var Q137;
            {var subQ1=sQuery(id+"F0.wireOp",EDGE,"E280");Q137=makeQuery(id+"F0.imprint","IMPRINT",FACE,{"disambiguationData":[TD([[makeQuery(id+"F0.imprint","IMPRINT",EDGE,{"derivedFrom":subQ1}),1.0]])]});}
            var Q138;
            {var subQ1=sQuery(id+"F0.wireOp",EDGE,"E280");Q138=makeQuery(id+"F0.imprint","IMPRINT",FACE,{"disambiguationData":[TD([[makeQuery(id+"F0.imprint","IMPRINT",EDGE,{"derivedFrom":subQ1}),-1.0]])]});}
            var Q139;
            {var subQ4=sQuery(id+"F0.wireOp",EDGE,"E278");Q139=makeQuery(id+"F0.imprint","IMPRINT",FACE,{"disambiguationData":[TD([[makeQuery(id+"F0.imprint","IMPRINT",EDGE,{"derivedFrom":subQ4}),1.0]])]});}
            var Q140;
            {var subQ0=sQuery(id+"F0.wireOp",EDGE,"E373.MirrorCS");var subQ1=sQuery(id+"F0.wireOp",EDGE,"E0");var subQ2=makeQuery(id+"F0.imprint","INTERSECT",VERTEX,{"derivedFrom":[subQ1,subQ0]});Q140=makeQuery(id+"F0.imprint","IMPRINT",FACE,{"disambiguationData":[TD([[makeQuery(id+"F0.imprint","IMPRINT",EDGE,{"disambiguationData":[TD([[subQ2,-1.0]])],"derivedFrom":subQ1}),1.0]])]});}
            var Q141;
            {var subQ5=sQuery(id+"F0.wireOp",EDGE,"E277");Q141=makeQuery(id+"F0.imprint","IMPRINT",FACE,{"disambiguationData":[TD([[makeQuery(id+"F0.imprint","IMPRINT",EDGE,{"derivedFrom":subQ5}),1.0]])]});}
            var Q142;
            {var subQ0=sQuery(id+"F0.wireOp",EDGE,"E358.MirrorCS");var subQ1=sQuery(id+"F0.wireOp",EDGE,"E0");var subQ2=makeQuery(id+"F0.imprint","INTERSECT",VERTEX,{"derivedFrom":[subQ1,subQ0]});Q142=makeQuery(id+"F0.imprint","IMPRINT",FACE,{"disambiguationData":[TD([[makeQuery(id+"F0.imprint","IMPRINT",EDGE,{"disambiguationData":[TD([[subQ2,1.0]])],"derivedFrom":subQ1}),1.0]])]});}
            var Q143;
            {var subQ0=sQuery(id+"F0.wireOp",EDGE,"E198");Q143=makeQuery(id+"F0.imprint","IMPRINT",FACE,{"disambiguationData":[TD([[makeQuery(id+"F0.imprint","IMPRINT",EDGE,{"derivedFrom":subQ0}),1.0]])]});}
            var Q144;
            {var subQ5=sQuery(id+"F0.wireOp",EDGE,"E197");Q144=makeQuery(id+"F0.imprint","IMPRINT",FACE,{"disambiguationData":[TD([[makeQuery(id+"F0.imprint","IMPRINT",EDGE,{"derivedFrom":subQ5}),1.0]])]});}
            extrude(context, id + "F2", {"entities" : qUnion([Q0, Q1, Q2, Q3, Q4, Q5, Q6, Q7, Q8, Q9, Q10, Q11, Q12, Q13, Q14, Q15, Q16, Q17, Q18, Q19, Q20, Q21, Q22, Q23, Q24, Q25, Q26, Q27, Q28, Q29, Q30, Q31, Q32, Q33, Q34, Q35, Q36, Q37, Q38, Q39, Q40, Q41, Q42, Q43, Q44, Q45, Q46, Q47, Q48, Q49, Q50, Q51, Q52, Q53, Q54, Q55, Q56, Q57, Q58, Q59, Q60, Q61, Q62, Q63, Q64, Q65, Q66, Q67, Q68, Q69, Q70, Q71, Q72, Q73, Q74, Q75, Q76, Q77, Q78, Q79, Q80, Q81, Q82, Q83, Q84, Q85, Q86, Q87, Q88, Q89, Q90, Q91, Q92, Q93, Q94, Q95, Q96, Q97, Q98, Q99, Q100, Q101, Q102, Q103, Q104, Q105, Q106, Q107, Q108, Q109, Q110, Q111, Q112, Q113, Q114, Q115, Q116, Q117, Q118, Q119, Q120, Q121, Q122, Q123, Q124, Q125, Q126, Q127, Q128, Q129, Q130, Q131, Q132, Q133, Q134, Q135, Q136, Q137, Q138, Q139, Q140, Q141, Q142, Q143, Q144]), "depth" : 12.7 * mm});
        }
    });
